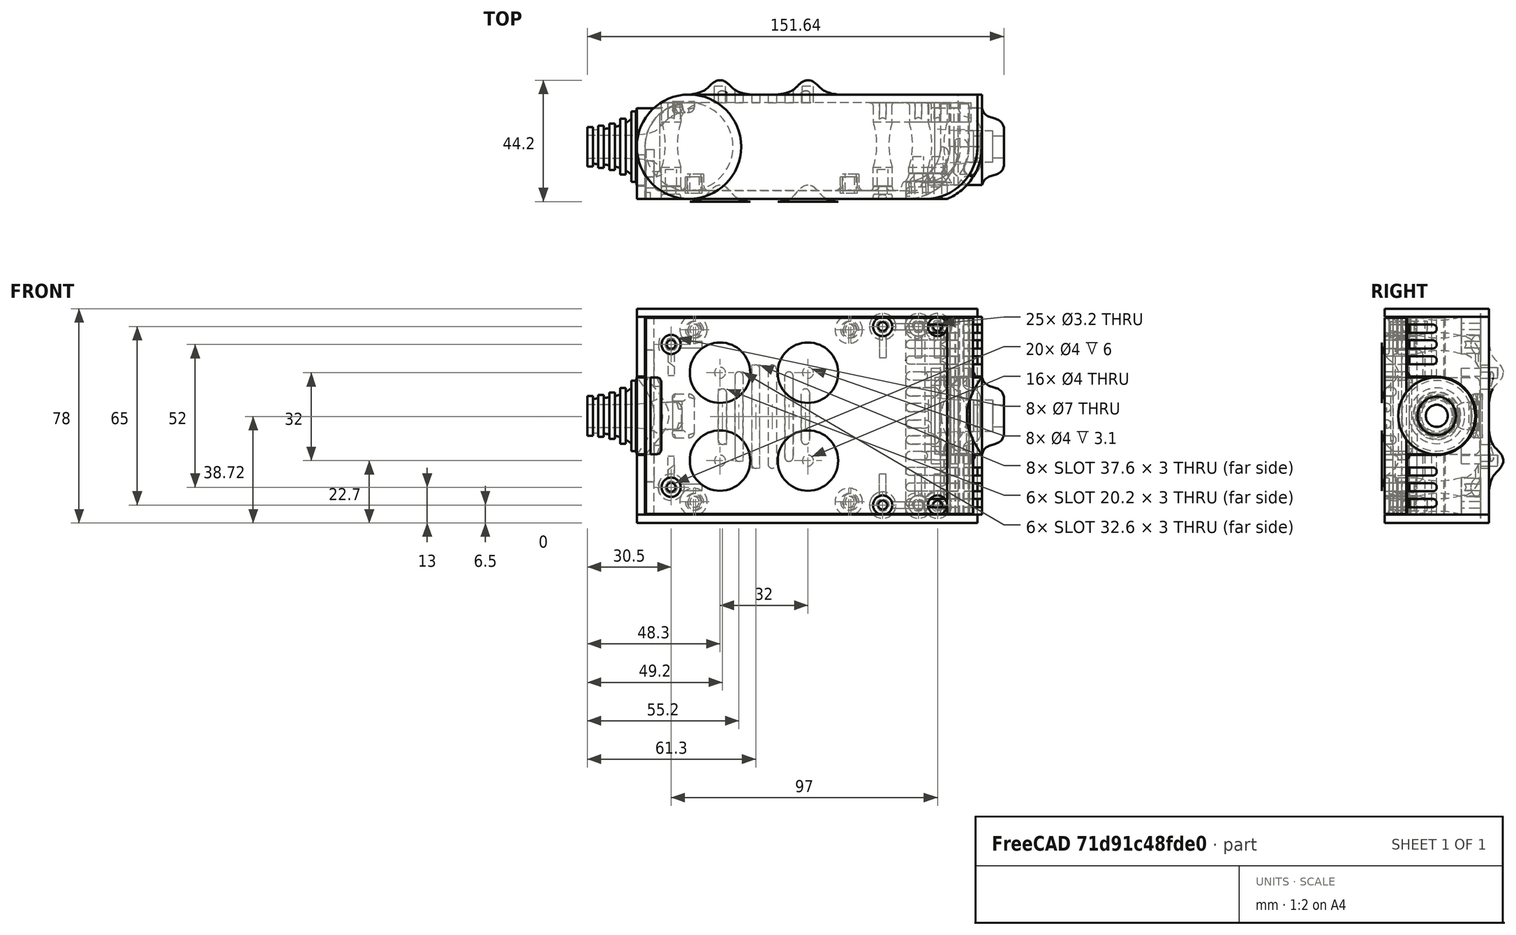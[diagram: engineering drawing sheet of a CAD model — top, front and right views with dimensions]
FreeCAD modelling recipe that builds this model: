
FCSTD DOCUMENT  (FreeCAD 0.19R0.19.2)
Label: enclosure_164
License: All rights reserved
LicenseURL: http://en.wikipedia.org/wiki/All_rights_reserved
objects: Part::Feature×140, Part::Revolution×140, Part::MultiFuse×123, Sketcher::SketchObject×69, Part::Extrusion×54, Part::Cut×53, Part::Cylinder×52, Part::Fillet×50, Part::Box×33, App::MeasureDistance×4
note: 714 computed .brp shape members not serialized (recipe doc carries the construction recipe); baked Part::Feature solids carry a one-line shape summary decoded from their .brp

FEATURE [Sketcher::SketchObject] Sketch  label="topSketch"
  FullyConstrained = true
  sketch-geometry (20):
    g0: LineSegment StartX=5.21097e-06 StartY=3 StartZ=0 EndX=5.21097e-06 EndY=19 EndZ=0
    g1: ArcOfCircle CenterX=19 CenterY=19 CenterZ=0 NormalX=0 NormalY=0 NormalZ=1 AngleXU=0 Radius=19 StartAngle=1.5708 EndAngle=3.14159
    g2: ArcOfCircle CenterX=19 CenterY=19 CenterZ=0 NormalX=0 NormalY=0 NormalZ=1 AngleXU=0 Radius=16 StartAngle=1.5708 EndAngle=3.14159
    g3: LineSegment StartX=114 StartY=35 StartZ=0 EndX=19 EndY=35 EndZ=0
    g4: LineSegment StartX=5.21097e-06 StartY=3 StartZ=0 EndX=5.21097e-06 EndY=0 EndZ=0
    g5: LineSegment StartX=3 StartY=0 StartZ=0 EndX=5.21097e-06 EndY=0 EndZ=0
    g6: LineSegment StartX=3 StartY=19 StartZ=0 EndX=3 EndY=0 EndZ=0
    g7: LineSegment StartX=19 StartY=38 StartZ=0 EndX=124 EndY=38 EndZ=0
    g8: Circle CenterX=119 CenterY=35 CenterZ=0 NormalX=0 NormalY=0 NormalZ=1 AngleXU=0 Radius=1
    g9: Circle CenterX=121 CenterY=35 CenterZ=0 NormalX=0 NormalY=0 NormalZ=1 AngleXU=0 Radius=1
    g10: Circle CenterX=121 CenterY=33 CenterZ=0 NormalX=0 NormalY=0 NormalZ=1 AngleXU=0 Radius=1
    g11: BSplineCurve PolesCount=3 KnotsCount=2 Degree=2 IsPeriodic=0
    g12: GeomPoint X=119 Y=35 Z=0
    g13: GeomPoint X=121 Y=33 Z=0
    g14: LineSegment StartX=119 StartY=35 StartZ=0 EndX=114 EndY=35 EndZ=0
    g15: ArcOfCircle CenterX=105 CenterY=19 CenterZ=0 NormalX=0 NormalY=0 NormalZ=1 AngleXU=0 Radius=19 StartAngle=5.7297 EndAngle=6.28319
    g16: ArcOfCircle CenterX=105 CenterY=19 CenterZ=0 NormalX=0 NormalY=0 NormalZ=1 AngleXU=0 Radius=16 StartAngle=5.60905 EndAngle=6.28319
    g17: LineSegment StartX=121 StartY=33 StartZ=0 EndX=121 EndY=19 EndZ=0
    g18: LineSegment StartX=124 StartY=38 StartZ=0 EndX=124 EndY=19 EndZ=0
    g19: LineSegment StartX=117.5 StartY=9.01251 StartZ=0 EndX=121.163 EndY=9.0125 EndZ=0
  constraints (46):
    c: Vertical(g0)
    c: Block(g0)
    c: Coincident(g1,g0)
    c: Block(g1)
    c: Coincident(g2,g1)
    c: Block(g2)
    c: Coincident(g3,g2)
    c: Horizontal(g3)
    c: Tangent(g3,g2)
    c: Coincident(g4,g0)
    c: Distance(g4) = 3
    c: Vertical(g4)
    c: Coincident(g5,g4)
    c: Horizontal(g5)
    c: Coincident(g6,g2)
    c: Coincident(g6,g5)
    c: Vertical(g6)
    c: Horizontal(g7)
    c: Distance(g7) = 105
    c: Coincident(g7,g1)
    c: Block(g3)
    c: Weight(g8) = 1
    c: Equal(g8,g9)
    c: Equal(g8,g10)
    c: InternalAlignment(g8,g11)
    c: InternalAlignment(g9,g11)
    c: InternalAlignment(g10,g11)
    c: InternalAlignment(g12,g11)
    c: InternalAlignment(g13,g11)
    c: Block(g11)
    c: Coincident(g14,g11)
    c: Coincident(g14,g3)
    c: Horizontal(g14)
    c: Block(g15)
    c: Coincident(g16,g15)
    c: Block(g16)
    c: Coincident(g17,g11)
    c: Coincident(g17,g16)
    c: Vertical(g17)
    c: Distance(g17) = 14
    c: Coincident(g18,g7)
    c: Coincident(g18,g15)
    c: Vertical(g18)
    c: Distance(g18) = 19
    c: Coincident(g19,g16)
    c: Coincident(g19,g15)
FEATURE [Sketcher::SketchObject] Sketch001  label="bottomSketch"
  FullyConstrained = true
  sketch-geometry (32):
    g0: LineSegment StartX=3.3 StartY=-6.03275e-07 StartZ=0 EndX=98 EndY=-6.03275e-07 EndZ=0
    g1: ArcOfCircle CenterX=98 CenterY=19 CenterZ=0 NormalX=0 NormalY=0 NormalZ=1 AngleXU=0 Radius=19 StartAngle=4.71239 EndAngle=5.71103
    g2: LineSegment StartX=6.3 StartY=8 StartZ=0 EndX=3.3 EndY=8 EndZ=0
    g3: LineSegment StartX=3.3 StartY=8 StartZ=0 EndX=3.3 EndY=-6.03275e-07 EndZ=0
    g4: ArcOfCircle CenterX=8.3 CenterY=5 CenterZ=0 NormalX=0 NormalY=0 NormalZ=1 AngleXU=0 Radius=2 StartAngle=3.14159 EndAngle=4.71239
    g5: LineSegment StartX=6.3 StartY=8 StartZ=0 EndX=6.3 EndY=5 EndZ=0
    g6: ArcOfCircle CenterX=98 CenterY=19 CenterZ=0 NormalX=0 NormalY=0 NormalZ=1 AngleXU=0 Radius=12.7 StartAngle=4.71239 EndAngle=6.28319
    g7: LineSegment StartX=94.7 StartY=3 StartZ=0 EndX=8.3 EndY=3 EndZ=0
    g8-g12: Circle x5 (B-spline internal-alignment scaffolding for g13; pole/knot coordinates omitted)
    g13: BSplineCurve PolesCount=5 KnotsCount=3 Degree=3 IsPeriodic=0
    g14: GeomPoint X=98 Y=6.3 Z=0
    g15: GeomPoint X=96.3938 Y=4.71946 Z=0
    g16: GeomPoint X=94.7 Y=3 Z=0
    g17-g23: Circle x7 (B-spline internal-alignment scaffolding for g24; pole/knot coordinates omitted)
    g24: BSplineCurve PolesCount=7 KnotsCount=5 Degree=3 IsPeriodic=0
    g25-g29: GeomPoint x5 (B-spline internal-alignment scaffolding for g24; pole/knot coordinates omitted)
    g30: ArcOfCircle CenterX=98 CenterY=19 CenterZ=0 NormalX=0 NormalY=0 NormalZ=1 AngleXU=0 Radius=15.7 StartAngle=5.81226 EndAngle=6.28319
    g31: LineSegment StartX=110.7 StartY=19 StartZ=0 EndX=113.7 EndY=19 EndZ=0
  constraints (41):
    c: Horizontal(g0)
    c: Coincident(g1,g0)
    c: Block(g1)
    c: Horizontal(g2)
    c: Distance(g2) = 3
    c: Coincident(g3,g2)
    c: Vertical(g3)
    c: Coincident(g3,g0)
    c: Block(g4)
    c: Block(g2)
    c: Coincident(g5,g2)
    c: Coincident(g5,g4)
    c: Vertical(g5)
    c: Coincident(g6,g1)
    c: Block(g6)
    c: Coincident(g7,g4)
    c: Horizontal(g7)
    c: Block(g0)
    c: Block(g7)
    c: Block(g3)
    c: Coincident(g13,g6)
    c: Weight(g8) = 1
    c: Equal(g8, g9-g12) x4
    c: Coincident(g13,g7)
    c: InternalAlignment(g8-g12 -> g13) x5
    c: InternalAlignment(g14,g13)
    c: InternalAlignment(g15,g13)
    c: InternalAlignment(g16,g13)
    c: Block(g13)
    c: Weight(g17) = 1
    c: Equal(g17, g18-g23) x6
    c: Coincident(g24,g1)
    c: InternalAlignment(g17-g23 -> g24) x7
    c: InternalAlignment(g25-g29 -> g24) x5
    c: Block(g24)
    c: Coincident(g30,g24)
    c: Coincident(g31,g6)
    c: Coincident(g31,g30)
    c: Horizontal(g31)
    c: Block(g31)
    c: Block(g30)
FEATURE [Part::Extrusion] Extrude  label="top"
  Base = -> Sketch
  Dir = (0,0,1)
  DirMode = 2
  FaceMakerClass = Part::FaceMakerBullseye
  LengthFwd = 72
  LengthRev = 0
  Solid = true
  Symmetric = false
FEATURE [Part::Extrusion] Extrude001  label="bottom"
  Base = -> Sketch001
  Dir = (0,0,1)
  DirMode = 2
  FaceMakerClass = Part::FaceMakerBullseye
  LengthFwd = 71.4
  LengthRev = 0
  Placement = pos=(0,0,0.3) rot=(0,0,1;0rad)
  Solid = true
  Symmetric = false
FEATURE [Sketcher::SketchObject] Sketch002  label="topSketch001"
  FullyConstrained = true
  sketch-geometry (6):
    g0: ArcOfCircle CenterX=19 CenterY=19 CenterZ=0 NormalX=0 NormalY=0 NormalZ=1 AngleXU=0 Radius=19 StartAngle=1.5708 EndAngle=3.14159
    g1: LineSegment StartX=5.22862e-06 StartY=19 StartZ=0 EndX=5.22862e-06 EndY=1.19904e-11 EndZ=0
    g2: LineSegment StartX=19 StartY=38 StartZ=0 EndX=124 EndY=38 EndZ=0
    g3: LineSegment StartX=5.22862e-06 StartY=1.19904e-11 StartZ=0 EndX=105 EndY=1.19904e-11 EndZ=0
    g4: ArcOfCircle CenterX=105 CenterY=19 CenterZ=0 NormalX=0 NormalY=0 NormalZ=1 AngleXU=0 Radius=19 StartAngle=4.71239 EndAngle=6.28319
    g5: LineSegment StartX=124 StartY=38 StartZ=0 EndX=124 EndY=19 EndZ=0
  constraints (16):
    c: Block(g0)
    c: Coincident(g1,g0)
    c: Vertical(g1)
    c: Horizontal(g2)
    c: Distance(g2) = 105
    c: Coincident(g2,g0)
    c: Distance(g1) = 19
    c: Coincident(g3,g1)
    c: Horizontal(g3)
    c: Distance(g3) = 105
    c: Block(g4)
    c: Coincident(g4,g3)
    c: Coincident(g5,g2)
    c: Coincident(g5,g4)
    c: Vertical(g5)
    c: Distance(g5) = 19
FEATURE [Part::Extrusion] Extrude002  label="sideA"
  Base = -> Sketch002
  Dir = (0,0,1)
  DirMode = 2
  FaceMakerClass = Part::FaceMakerBullseye
  LengthFwd = 3
  LengthRev = 0
  Placement = pos=(0,0,-3) rot=(0,0,1;0rad)
  Solid = true
  Symmetric = false
FEATURE [Sketcher::SketchObject] Sketch003  label="topSketch002"
  FullyConstrained = true
  sketch-geometry (6):
    g0: LineSegment StartX=19 StartY=38 StartZ=0 EndX=117 EndY=38 EndZ=0
    g1: ArcOfCircle CenterX=19 CenterY=19 CenterZ=0 NormalX=0 NormalY=0 NormalZ=1 AngleXU=0 Radius=19 StartAngle=1.5708 EndAngle=3.14159
    g2: LineSegment StartX=117 StartY=38 StartZ=0 EndX=117 EndY=19 EndZ=0
    g3: LineSegment StartX=98 StartY=1.0161e-12 StartZ=0 EndX=5.22862e-06 EndY=1.0161e-12 EndZ=0
    g4: LineSegment StartX=5.22862e-06 StartY=19 StartZ=0 EndX=5.22862e-06 EndY=1.0161e-12 EndZ=0
    g5: ArcOfCircle CenterX=98 CenterY=19 CenterZ=0 NormalX=0 NormalY=0 NormalZ=1 AngleXU=0 Radius=19 StartAngle=4.71239 EndAngle=6.28319
  constraints (16):
    c: Horizontal(g0)
    c: Distance(g0) = 98
    c: Coincident(g1,g0)
    c: Block(g1)
    c: Coincident(g2,g0)
    c: Vertical(g2)
    c: Distance(g2) = 19
    c: Horizontal(g3)
    c: Coincident(g4,g1)
    c: Vertical(g4)
    c: Coincident(g3,g4)
    c: Block(g3)
    c: Coincident(g5,g2)
    c: Coincident(g5,g3)
    c: Block(g0)
    c: Block(g5)
FEATURE [Sketcher::SketchObject] Sketch004
  FullyConstrained = true
  MapMode = 3
  Placement = pos=(0,0,0) rot=(1,0,0;1.5708rad)
  Support = -> [Extrude]
  sketch-geometry (8):
    g0: Circle CenterX=80.351 CenterY=-67.6202 CenterZ=0 NormalX=0 NormalY=0 NormalZ=1 AngleXU=0 Radius=2
    g1: Circle CenterX=80.351 CenterY=-67.6202 CenterZ=0 NormalX=0 NormalY=0 NormalZ=1 AngleXU=0 Radius=3
    g2: Circle CenterX=80.351 CenterY=-4.92017 CenterZ=0 NormalX=0 NormalY=0 NormalZ=1 AngleXU=0 Radius=2
    g3: Circle CenterX=80.351 CenterY=-4.92017 CenterZ=0 NormalX=0 NormalY=0 NormalZ=1 AngleXU=0 Radius=3
    g4: Circle CenterX=23.851 CenterY=-4.92017 CenterZ=0 NormalX=0 NormalY=0 NormalZ=1 AngleXU=0 Radius=2
    g5: Circle CenterX=23.851 CenterY=-4.92017 CenterZ=0 NormalX=0 NormalY=0 NormalZ=1 AngleXU=0 Radius=3
    g6: Circle CenterX=23.851 CenterY=-67.6202 CenterZ=0 NormalX=0 NormalY=0 NormalZ=1 AngleXU=0 Radius=2
    g7: Circle CenterX=23.851 CenterY=-67.6202 CenterZ=0 NormalX=0 NormalY=0 NormalZ=1 AngleXU=0 Radius=3
  constraints (8):
    c: Block(g3)
    c: Block(g2)
    c: Block(g1)
    c: Block(g0)
    c: Block(g6)
    c: Block(g7)
    c: Block(g4)
    c: Block(g5)
FEATURE [Part::Extrusion] Extrude004
  Base = -> Sketch004
  Dir = (0,-1,2e-16)
  DirMode = 2
  FaceMakerClass = Part::FaceMakerBullseye
  LengthFwd = 6
  LengthRev = 0
  Placement = pos=(0,9,0) rot=(0,0,1;0rad)
  Solid = true
  Symmetric = false
FEATURE [Sketcher::SketchObject] Sketch005
  FullyConstrained = true
  MapMode = 3
  Placement = pos=(0,0,0) rot=(1,0,0;1.5708rad)
  Support = -> [Extrude]
  sketch-geometry (8):
    g0: Circle CenterX=80.351 CenterY=-67.6202 CenterZ=0 NormalX=0 NormalY=0 NormalZ=1 AngleXU=0 Radius=3
    g1: Circle CenterX=80.351 CenterY=-4.92017 CenterZ=0 NormalX=0 NormalY=0 NormalZ=1 AngleXU=0 Radius=3
    g2: Circle CenterX=23.851 CenterY=-4.92017 CenterZ=0 NormalX=0 NormalY=0 NormalZ=1 AngleXU=0 Radius=3
    g3: Circle CenterX=23.851 CenterY=-67.6202 CenterZ=0 NormalX=0 NormalY=0 NormalZ=1 AngleXU=0 Radius=3
    g4: Circle CenterX=23.851 CenterY=-67.6202 CenterZ=0 NormalX=0 NormalY=0 NormalZ=1 AngleXU=0 Radius=5
    g5: Circle CenterX=80.351 CenterY=-67.6202 CenterZ=0 NormalX=0 NormalY=0 NormalZ=1 AngleXU=0 Radius=5
    g6: Circle CenterX=23.851 CenterY=-4.92017 CenterZ=0 NormalX=0 NormalY=0 NormalZ=1 AngleXU=0 Radius=5
    g7: Circle CenterX=80.351 CenterY=-4.92017 CenterZ=0 NormalX=0 NormalY=0 NormalZ=1 AngleXU=0 Radius=5
  constraints (8):
    c: Block(g1)
    c: Block(g0)
    c: Block(g3)
    c: Block(g2)
    c: Block(g5)
    c: Block(g4)
    c: Block(g6)
    c: Block(g7)
FEATURE [Part::Extrusion] Extrude005
  Base = -> Sketch005
  Dir = (0,-1,2e-16)
  DirMode = 2
  FaceMakerClass = Part::FaceMakerBullseye
  LengthFwd = 2
  LengthRev = 0
  Solid = true
  Symmetric = false
FEATURE [Sketcher::SketchObject] Sketch006
  FullyConstrained = true
  MapMode = 3
  Placement = pos=(0,0,0) rot=(1,0,0;1.5708rad)
  sketch-geometry (8):
    g0: Circle CenterX=80.351 CenterY=-67.6202 CenterZ=0 NormalX=0 NormalY=0 NormalZ=1 AngleXU=0 Radius=3
    g1: Circle CenterX=80.351 CenterY=-4.92017 CenterZ=0 NormalX=0 NormalY=0 NormalZ=1 AngleXU=0 Radius=3
    g2: Circle CenterX=23.851 CenterY=-4.92017 CenterZ=0 NormalX=0 NormalY=0 NormalZ=1 AngleXU=0 Radius=3
    g3: Circle CenterX=23.851 CenterY=-67.6202 CenterZ=0 NormalX=0 NormalY=0 NormalZ=1 AngleXU=0 Radius=3
    g4: Circle CenterX=23.851 CenterY=-67.6202 CenterZ=0 NormalX=0 NormalY=0 NormalZ=1 AngleXU=0 Radius=5
    g5: Circle CenterX=80.351 CenterY=-67.6202 CenterZ=0 NormalX=0 NormalY=0 NormalZ=1 AngleXU=0 Radius=5
    g6: Circle CenterX=23.851 CenterY=-4.92017 CenterZ=0 NormalX=0 NormalY=0 NormalZ=1 AngleXU=0 Radius=5
    g7: Circle CenterX=80.351 CenterY=-4.92017 CenterZ=0 NormalX=0 NormalY=0 NormalZ=1 AngleXU=0 Radius=5
  constraints (8):
    c: Block(g1)
    c: Block(g0)
    c: Block(g3)
    c: Block(g2)
    c: Block(g5)
    c: Block(g4)
    c: Block(g6)
    c: Block(g7)
FEATURE [Part::Extrusion] Extrude007
  Base = -> Sketch006
  Dir = (0,-1,2e-16)
  DirMode = 2
  FaceMakerClass = Part::FaceMakerBullseye
  LengthFwd = 2
  LengthRev = 0
  Solid = true
  Symmetric = false
FEATURE [Part::Fillet] Fillet
  Base = -> Extrude007
  Edges = 4 edges r=1.99: [Edge6,Edge12,Edge18,Edge24]
FEATURE [Part::Cut] Cut
  Base = -> Extrude005
  Placement = pos=(0,5,0) rot=(0,0,1;0rad)
  Tool = -> Fillet
FEATURE [Part::MultiFuse] Fusion  label="pCBScrews"
  Placement = pos=(-2.5,0,72.3) rot=(0,0,1;0rad)
  Shapes = -> [Extrude004,Cut]
FEATURE [App::MeasureDistance] Distance  label="Distance: 0.69 mm"
  Distance = 0.685967
  P1 = (24.0138,2.9647,0.3)
  P2 = (23.8901,3,-0.373787)
FEATURE [App::MeasureDistance] Distance001  label="Distance: 0.53 mm"
  Distance = 0.533607
  P1 = (80.2939,3,72.2334)
  P2 = (80.281,2.99661,71.7)
FEATURE [Part::Fillet] Fillet001
  Base = -> Extrude001
  Edges = 1 edges r=2.4: [Edge17]
FEATURE [Part::Fillet] Fillet002  label="bottom001"
  Base = -> Fillet001
  Edges = 1 edges r=2.4: [Edge36]
FEATURE [Part::Fillet] Fillet003  label="top001"
  Base = -> Extrude
  Edges = 1 edges r=2: [Edge1]
FEATURE [Sketcher::SketchObject] Sketch007
  FullyConstrained = true
  sketch-geometry (16):
    g0: LineSegment StartX=4 StartY=0 StartZ=0 EndX=4 EndY=2.4 EndZ=0
    g1: LineSegment StartX=4 StartY=2.4 StartZ=0 EndX=7 EndY=2.4 EndZ=0
    g2: LineSegment StartX=4 StartY=0 StartZ=0 EndX=5.7 EndY=0 EndZ=0
    g3: LineSegment StartX=5.7 StartY=0 StartZ=0 EndX=5.7 EndY=-5.6 EndZ=0
    g4-g8: Circle x5 (B-spline internal-alignment scaffolding for g9; pole/knot coordinates omitted)
    g9: BSplineCurve PolesCount=5 KnotsCount=3 Degree=3 IsPeriodic=0
    g10: GeomPoint X=7 Y=2.4 Z=0
    g11: GeomPoint X=10.4582 Y=-1.55472 Z=0
    g12: GeomPoint X=14 Y=-5.6 Z=0
    g13: LineSegment StartX=14 StartY=-5.6 StartZ=0 EndX=14 EndY=-14.1 EndZ=0
    g14: LineSegment StartX=14 StartY=-14.1 StartZ=0 EndX=6.5 EndY=-14.1 EndZ=0
    g15: LineSegment StartX=5.7 StartY=-5.6 StartZ=0 EndX=6.5 EndY=-14.1 EndZ=0
  constraints (28):
    c: Distance(g0) = 2.4
    c: Vertical(g0)
    c: Block(g0)
    c: Coincident(g1,g0)
    c: Horizontal(g1)
    c: Distance(g1) = 3
    c: Coincident(g2,g0)
    c: Horizontal(g2)
    c: Distance(g2) = 1.7
    c: Coincident(g3,g2)
    c: Vertical(g3)
    c: Distance(g3) = 5.6
    c: Coincident(g9,g1)
    c: Weight(g4) = 1
    c: Equal(g4, g5-g8) x4
    c: InternalAlignment(g4-g8 -> g9) x5
    c: InternalAlignment(g10,g9)
    c: InternalAlignment(g11,g9)
    c: InternalAlignment(g12,g9)
    c: Block(g9)
    c: Coincident(g13,g9)
    c: Vertical(g13)
    c: Distance(g13) = 8.5
    c: Coincident(g14,g13)
    c: Horizontal(g14)
    c: Distance(g14) = 7.5
    c: Coincident(g15,g3)
    c: Coincident(g15,g14)
FEATURE [Part::Feature] Face
  shape: bbox 10 x 16.5 x 2e-07 mm, 1 faces, 0 solids (baked)
FEATURE [Part::Revolution] Revolve  label="plugHousing"
  Angle = 360
  Axis = (0,1,0)
  Base = (0,0,0)
  FaceMakerClass = Part::FaceMakerBullseye
  Placement = pos=(0,0,36.15) rot=(0,0,1;0rad)
  Solid = false
  Source = -> Face
  Symmetric = false
FEATURE [Part::Feature] Face001
  shape: bbox 10 x 16.5 x 2e-07 mm, 1 faces, 0 solids (baked)
FEATURE [Part::Revolution] Revolve001  label="plugHousing001"
  Angle = 360
  Axis = (0,1,0)
  Base = (0,0,0)
  FaceMakerClass = Part::FaceMakerBullseye
  Placement = pos=(0,0,36.15) rot=(0,0,1;0rad)
  Solid = false
  Source = -> Face001
  Symmetric = false
FEATURE [Part::MultiFuse] Fusion001  label="plugHousing002"
  Placement = pos=(0,0,0) rot=(0,0,1;1.5708rad)
  Shapes = -> [Revolve001,Revolve]
FEATURE [Part::Feature] Face002
  shape: bbox 10 x 16.5 x 2e-07 mm, 1 faces, 0 solids (baked)
FEATURE [Part::Revolution] Revolve003  label="plugHousing005"
  Angle = 360
  Axis = (0,1,0)
  Base = (0,0,0)
  FaceMakerClass = Part::FaceMakerBullseye
  Placement = pos=(0,0,36.15) rot=(0,0,1;0rad)
  Solid = false
  Source = -> Face002
  Symmetric = false
FEATURE [Part::Feature] Face003
  shape: bbox 10 x 16.5 x 2e-07 mm, 1 faces, 0 solids (baked)
FEATURE [Part::Revolution] Revolve002  label="plugHousing003"
  Angle = 360
  Axis = (0,1,0)
  Base = (0,0,0)
  FaceMakerClass = Part::FaceMakerBullseye
  Placement = pos=(0,0,36.15) rot=(0,0,1;0rad)
  Solid = false
  Source = -> Face003
  Symmetric = false
FEATURE [Part::MultiFuse] Fusion002  label="plugHousing004"
  Placement = pos=(0,0,0) rot=(0,0,1;1.5708rad)
  Shapes = -> [Revolve002,Revolve003]
FEATURE [Part::MultiFuse] Fusion003  label="plugHousing006"
  Placement = pos=(0,19,0) rot=(0,0,1;3.14159rad)
  Shapes = -> [Fusion002,Fusion001]
FEATURE [Part::Feature] Face004
  shape: bbox 10 x 16.5 x 2e-07 mm, 1 faces, 0 solids (baked)
FEATURE [Part::Revolution] Revolve006  label="plugHousing010"
  Angle = 360
  Axis = (0,1,0)
  Base = (0,0,0)
  FaceMakerClass = Part::FaceMakerBullseye
  Placement = pos=(0,0,36.15) rot=(0,0,1;0rad)
  Solid = false
  Source = -> Face004
  Symmetric = false
FEATURE [Part::Feature] Face005
  shape: bbox 10 x 16.5 x 2e-07 mm, 1 faces, 0 solids (baked)
FEATURE [Part::Revolution] Revolve007  label="plugHousing011"
  Angle = 360
  Axis = (0,1,0)
  Base = (0,0,0)
  FaceMakerClass = Part::FaceMakerBullseye
  Placement = pos=(0,0,36.15) rot=(0,0,1;0rad)
  Solid = false
  Source = -> Face005
  Symmetric = false
FEATURE [Part::Feature] Face006
  shape: bbox 10 x 16.5 x 2e-07 mm, 1 faces, 0 solids (baked)
FEATURE [Part::Revolution] Revolve004  label="plugHousing007"
  Angle = 360
  Axis = (0,1,0)
  Base = (0,0,0)
  FaceMakerClass = Part::FaceMakerBullseye
  Placement = pos=(0,0,36.15) rot=(0,0,1;0rad)
  Solid = false
  Source = -> Face006
  Symmetric = false
FEATURE [Part::MultiFuse] Fusion004  label="plugHousing009"
  Placement = pos=(0,0,0) rot=(0,0,1;1.5708rad)
  Shapes = -> [Revolve004,Revolve007]
FEATURE [Part::Feature] Face007
  shape: bbox 10 x 16.5 x 2e-07 mm, 1 faces, 0 solids (baked)
FEATURE [Part::Revolution] Revolve005  label="plugHousing008"
  Angle = 360
  Axis = (0,1,0)
  Base = (0,0,0)
  FaceMakerClass = Part::FaceMakerBullseye
  Placement = pos=(0,0,36.15) rot=(0,0,1;0rad)
  Solid = false
  Source = -> Face007
  Symmetric = false
FEATURE [Part::MultiFuse] Fusion005  label="plugHousing012"
  Placement = pos=(0,0,0) rot=(0,0,1;1.5708rad)
  Shapes = -> [Revolve006,Revolve005]
FEATURE [Part::MultiFuse] Fusion006  label="plugHousing013"
  Placement = pos=(0,19,0) rot=(0,0,1;3.14159rad)
  Shapes = -> [Fusion005,Fusion004]
FEATURE [Part::MultiFuse] Fusion007  label="plugHousing014"
  Placement = pos=(122.621,0,-0.15) rot=(0,0,1;0rad)
  Shapes = -> [Fusion003,Fusion006]
FEATURE [Part::Cylinder] Cylinder002
  Angle = 360
  AttacherType = Attacher::AttachEngine3D
  Height = 20
  Placement = pos=(0,0,36.15) rot=(0,0,1;0rad)
  Radius = 4
FEATURE [Part::Cylinder] Cylinder003
  Angle = 360
  AttacherType = Attacher::AttachEngine3D
  Height = 10
  Placement = pos=(0,0,36.15) rot=(0,0,1;0rad)
  Radius = 4
FEATURE [Part::MultiFuse] Fusion009  label="removeToCreateHoleForPlugHousing"
  Placement = pos=(70,19,36.15) rot=(0,1,0;1.5708rad)
  Shapes = -> [Cylinder002,Cylinder003]
FEATURE [Part::Cylinder] Cylinder004
  Angle = 360
  AttacherType = Attacher::AttachEngine3D
  Height = 20
  Placement = pos=(0,0,36.15) rot=(0,0,1;0rad)
  Radius = 4
FEATURE [Part::Cylinder] Cylinder005
  Angle = 360
  AttacherType = Attacher::AttachEngine3D
  Height = 10
  Placement = pos=(0,0,36.15) rot=(0,0,1;0rad)
  Radius = 4
FEATURE [Part::MultiFuse] Fusion010  label="removeToCreateHoleForPlugHousing001"
  Placement = pos=(70,19,36.15) rot=(0,1,0;1.5708rad)
  Shapes = -> [Cylinder004,Cylinder005]
FEATURE [Part::Cut] Cut001
  Base = -> Fillet003
  Tool = -> Fusion010
FEATURE [Part::Cut] Cut002  label="Bottom"
  Base = -> Fillet002
  Tool = -> Fusion009
FEATURE [Part::Feature] Face008
  shape: bbox 10 x 16.5 x 2e-07 mm, 1 faces, 0 solids (baked)
FEATURE [Part::Revolution] Revolve011  label="plugHousing021"
  Angle = 360
  Axis = (0,1,0)
  Base = (0,0,0)
  FaceMakerClass = Part::FaceMakerBullseye
  Placement = pos=(0,0,36.15) rot=(0,0,1;0rad)
  Solid = false
  Source = -> Face008
  Symmetric = false
FEATURE [Part::Feature] Face009
  shape: bbox 10 x 16.5 x 2e-07 mm, 1 faces, 0 solids (baked)
FEATURE [Part::Revolution] Revolve012  label="plugHousing022"
  Angle = 360
  Axis = (0,1,0)
  Base = (0,0,0)
  FaceMakerClass = Part::FaceMakerBullseye
  Placement = pos=(0,0,36.15) rot=(0,0,1;0rad)
  Solid = false
  Source = -> Face009
  Symmetric = false
FEATURE [Part::Feature] Face010 .. Face013  x4 (patterned run collapsed; names and placements below)
  shape: bbox 10 x 16.5 x 2e-07 mm, 1 faces, 0 solids (baked)
FEATURE [Part::Revolution] Revolve015  label="plugHousing027"
  Angle = 360
  Axis = (0,1,0)
  Base = (0,0,0)
  FaceMakerClass = Part::FaceMakerBullseye
  Placement = pos=(0,0,36.15) rot=(0,0,1;0rad)
  Solid = false
  Source = -> Face013
  Symmetric = false
FEATURE [Part::Feature] Face014
  shape: bbox 10 x 16.5 x 2e-07 mm, 1 faces, 0 solids (baked)
FEATURE [Part::Feature] Face015
  shape: bbox 10 x 16.5 x 2e-07 mm, 1 faces, 0 solids (baked)
FEATURE [Part::Feature] Face016
  shape: bbox 10 x 16.5 x 2e-07 mm, 1 faces, 0 solids (baked)
FEATURE [Part::Revolution] Revolve019  label="plugHousing033"
  Angle = 360
  Axis = (0,1,0)
  Base = (0,0,0)
  FaceMakerClass = Part::FaceMakerBullseye
  Placement = pos=(0,0,36.15) rot=(0,0,1;0rad)
  Solid = false
  Source = -> Face016
  Symmetric = false
FEATURE [Part::Feature] Face017
  shape: bbox 10 x 16.5 x 2e-07 mm, 1 faces, 0 solids (baked)
FEATURE [Part::Revolution] Revolve020  label="plugHousing034"
  Angle = 360
  Axis = (0,1,0)
  Base = (0,0,0)
  FaceMakerClass = Part::FaceMakerBullseye
  Placement = pos=(0,0,36.15) rot=(0,0,1;0rad)
  Solid = false
  Source = -> Face017
  Symmetric = false
FEATURE [Part::Feature] Face018
  shape: bbox 10 x 16.5 x 2e-07 mm, 1 faces, 0 solids (baked)
FEATURE [Part::Revolution] Revolve016  label="plugHousing030"
  Angle = 360
  Axis = (0,1,0)
  Base = (0,0,0)
  FaceMakerClass = Part::FaceMakerBullseye
  Placement = pos=(0,0,36.15) rot=(0,0,1;0rad)
  Solid = false
  Source = -> Face018
  Symmetric = false
FEATURE [Part::MultiFuse] Fusion020  label="plugHousing038"
  Placement = pos=(0,0,0) rot=(0,0,1;1.5708rad)
  Shapes = -> [Revolve016,Revolve020]
FEATURE [Part::Feature] Face019
  shape: bbox 10 x 16.5 x 2e-07 mm, 1 faces, 0 solids (baked)
FEATURE [Part::Feature] Face020
  shape: bbox 10 x 16.5 x 2e-07 mm, 1 faces, 0 solids (baked)
FEATURE [Part::Revolution] Revolve017  label="plugHousing031"
  Angle = 360
  Axis = (0,1,0)
  Base = (0,0,0)
  FaceMakerClass = Part::FaceMakerBullseye
  Placement = pos=(0,0,36.15) rot=(0,0,1;0rad)
  Solid = false
  Source = -> Face020
  Symmetric = false
FEATURE [Part::MultiFuse] Fusion021  label="plugHousing039"
  Placement = pos=(0,0,0) rot=(0,0,1;1.5708rad)
  Shapes = -> [Revolve019,Revolve017]
FEATURE [Part::MultiFuse] Fusion023  label="plugHousing041"
  Placement = pos=(0,19,0) rot=(0,0,1;3.14159rad)
  Shapes = -> [Fusion021,Fusion020]
FEATURE [Part::Revolution] Revolve022  label="plugHousing043"
  Angle = 360
  Axis = (0,1,0)
  Base = (0,0,0)
  FaceMakerClass = Part::FaceMakerBullseye
  Placement = pos=(0,0,36.15) rot=(0,0,1;0rad)
  Solid = false
  Source = -> Face019
  Symmetric = false
FEATURE [Part::Feature] Face021
  shape: bbox 10 x 16.5 x 2e-07 mm, 1 faces, 0 solids (baked)
FEATURE [Part::Revolution] Revolve023  label="plugHousing044"
  Angle = 360
  Axis = (0,1,0)
  Base = (0,0,0)
  FaceMakerClass = Part::FaceMakerBullseye
  Placement = pos=(0,0,36.15) rot=(0,0,1;0rad)
  Solid = false
  Source = -> Face021
  Symmetric = false
FEATURE [Part::Feature] Face022
  shape: bbox 10 x 16.5 x 2e-07 mm, 1 faces, 0 solids (baked)
FEATURE [Part::Revolution] Revolve018  label="plugHousing032"
  Angle = 360
  Axis = (0,1,0)
  Base = (0,0,0)
  FaceMakerClass = Part::FaceMakerBullseye
  Placement = pos=(0,0,36.15) rot=(0,0,1;0rad)
  Solid = false
  Source = -> Face022
  Symmetric = false
FEATURE [Part::MultiFuse] Fusion022  label="plugHousing040"
  Placement = pos=(0,0,0) rot=(0,0,1;1.5708rad)
  Shapes = -> [Revolve018,Revolve023]
FEATURE [Part::Feature] Face023
  shape: bbox 10 x 16.5 x 2e-07 mm, 1 faces, 0 solids (baked)
FEATURE [Part::Revolution] Revolve021  label="plugHousing035"
  Angle = 360
  Axis = (0,1,0)
  Base = (0,0,0)
  FaceMakerClass = Part::FaceMakerBullseye
  Placement = pos=(0,0,36.15) rot=(0,0,1;0rad)
  Solid = false
  Source = -> Face023
  Symmetric = false
FEATURE [Part::MultiFuse] Fusion018  label="plugHousing036"
  Placement = pos=(0,0,0) rot=(0,0,1;1.5708rad)
  Shapes = -> [Revolve022,Revolve021]
FEATURE [Part::MultiFuse] Fusion019  label="plugHousing037"
  Placement = pos=(0,19,0) rot=(0,0,1;3.14159rad)
  Shapes = -> [Fusion018,Fusion022]
FEATURE [Part::MultiFuse] Fusion024  label="plugHousing042"
  Placement = pos=(122.621,0,-0.15) rot=(0,0,1;0rad)
  Shapes = -> [Fusion023,Fusion019]
FEATURE [Part::Cylinder] Cylinder006
  Angle = 360
  AttacherType = Attacher::AttachEngine3D
  Height = 20
  Placement = pos=(0,0,36.15) rot=(0,0,1;0rad)
  Radius = 14.3
FEATURE [Part::Cylinder] Cylinder007
  Angle = 360
  AttacherType = Attacher::AttachEngine3D
  Height = 10
  Placement = pos=(0,0,36.15) rot=(0,0,1;0rad)
  Radius = 4
FEATURE [Part::MultiFuse] Fusion026  label="removeToCreteHoleForPlugHousing"
  Placement = pos=(70,19,36) rot=(0,1,0;1.5708rad)
  Shapes = -> [Cylinder006,Cylinder007]
FEATURE [Part::Box] Box001  label="Cube001"
  AttacherType = Attacher::AttachEngine3D
  Height = 28
  Length = 3
  Placement = pos=(110.7,19,22) rot=(0,0,1;0rad)
  Width = 15.7
FEATURE [Part::Cut] Cut003  label="top002"
  Base = -> Cut001
  Tool = -> Fusion007
FEATURE [Part::Revolution] Revolve008  label="plugHousing015"
  Angle = 360
  Axis = (0,1,0)
  Base = (0,0,0)
  FaceMakerClass = Part::FaceMakerBullseye
  Placement = pos=(0,0,36.15) rot=(0,0,1;0rad)
  Solid = false
  Source = -> Face010
  Symmetric = false
FEATURE [Part::MultiFuse] Fusion013  label="plugHousing020"
  Placement = pos=(0,0,0) rot=(0,0,1;1.5708rad)
  Shapes = -> [Revolve008,Revolve012]
FEATURE [Part::Cut] Cut004  label="top003"
  Base = -> Cut003
  Placement = pos=(1,0,0) rot=(0,0,1;0rad)
  Tool = -> Fusion026
FEATURE [Part::Cylinder] Cylinder008
  Angle = 360
  AttacherType = Attacher::AttachEngine3D
  Height = 20
  Placement = pos=(0,0,36.15) rot=(0,0,1;0rad)
  Radius = 10.3
FEATURE [Part::Cylinder] Cylinder009
  Angle = 360
  AttacherType = Attacher::AttachEngine3D
  Height = 10
  Placement = pos=(0,0,36.15) rot=(0,0,1;0rad)
  Radius = 4
FEATURE [Part::MultiFuse] Fusion027  label="removeToCreteHoleForPlugHousing001"
  Placement = pos=(70,19,36) rot=(0,1,0;1.5708rad)
  Shapes = -> [Cylinder008,Cylinder009]
FEATURE [Part::Cut] Cut005  label="plugHousingTab"
  Base = -> Box001
  Tool = -> Fusion027
FEATURE [Part::MultiFuse] Fusion028  label="plugHousing045"
  Shapes = -> [Fusion024,Cut005]
FEATURE [Part::Box] Box002  label="Cube002"
  AttacherType = Attacher::AttachEngine3D
  Height = 28.8
  Length = 3
  Placement = pos=(107.3,28,21.6) rot=(0,0,1;0rad)
  Width = 7
FEATURE [Part::Box] Box003  label="Cube003"
  AttacherType = Attacher::AttachEngine3D
  Height = 3
  Length = 6.4
  Placement = pos=(107.3,28,18.6) rot=(0,0,1;0rad)
  Width = 7
FEATURE [Part::Box] Box004  label="Cube004"
  AttacherType = Attacher::AttachEngine3D
  Height = 3
  Length = 6.4
  Placement = pos=(107.3,28,50.4) rot=(0,0,1;0rad)
  Width = 7
FEATURE [Part::MultiFuse] Fusion029  label="plugHousingBracketHolder"
  Shapes = -> [Box004,Box002,Box003]
FEATURE [Part::Cylinder] Cylinder010
  Angle = 360
  AttacherType = Attacher::AttachEngine3D
  Height = 20
  Placement = pos=(0,0,36.15) rot=(0,0,1;0rad)
  Radius = 14.3
FEATURE [Part::Cylinder] Cylinder011
  Angle = 360
  AttacherType = Attacher::AttachEngine3D
  Height = 10
  Placement = pos=(0,0,36.15) rot=(0,0,1;0rad)
  Radius = 4
FEATURE [Part::MultiFuse] Fusion030  label="removeToCreteHoleForPlugHousing002"
  Placement = pos=(70,19,36) rot=(0,1,0;1.5708rad)
  Shapes = -> [Cylinder010,Cylinder011]
FEATURE [Part::Cut] Cut006  label="plugHousingBracketHolder001"
  Base = -> Fusion029
  Tool = -> Fusion030
FEATURE [Part::Cylinder] Cylinder012
  Angle = 360
  AttacherType = Attacher::AttachEngine3D
  Height = 20
  Placement = pos=(0,0,36.15) rot=(0,0,1;0rad)
  Radius = 7
FEATURE [Part::Cylinder] Cylinder013
  Angle = 360
  AttacherType = Attacher::AttachEngine3D
  Height = 10
  Placement = pos=(0,0,36.15) rot=(0,0,1;0rad)
  Radius = 4
FEATURE [Part::MultiFuse] Fusion032  label="removeToCreteHoleForPlugHousing003"
  Placement = pos=(70,19,36) rot=(0,1,0;1.5708rad)
  Shapes = -> [Cylinder012,Cylinder013]
FEATURE [Part::Cut] Cut007  label="bottom002"
  Base = -> Cut002
  Tool = -> Fusion032
FEATURE [Sketcher::SketchObject] Sketch008
  FullyConstrained = true
  sketch-geometry (54):
    g0: LineSegment StartX=-4.2 StartY=0 StartZ=0 EndX=-6.2 EndY=0 EndZ=0
    g1: LineSegment StartX=-14 StartY=-18 StartZ=0 EndX=-14 EndY=-26.5 EndZ=0
    g2: LineSegment StartX=-4.2 StartY=0 StartZ=0 EndX=-4.2 EndY=-13.4877 EndZ=0
    g3: Circle CenterX=-4.2 CenterY=-13.4877 CenterZ=0 NormalX=0 NormalY=0 NormalZ=1 AngleXU=0 Radius=1
    g4: Circle CenterX=-4.2 CenterY=-26.5 CenterZ=0 NormalX=0 NormalY=0 NormalZ=1 AngleXU=0 Radius=1
    g5: Circle CenterX=-8.2 CenterY=-26.5 CenterZ=0 NormalX=0 NormalY=0 NormalZ=1 AngleXU=0 Radius=1
    g6: BSplineCurve PolesCount=3 KnotsCount=2 Degree=2 IsPeriodic=0
    g7: GeomPoint X=-4.2 Y=-13.4877 Z=0
    g8: GeomPoint X=-8.2 Y=-26.5 Z=0
    g9: LineSegment StartX=-14 StartY=-26.5 StartZ=0 EndX=-8.2 EndY=-26.5 EndZ=0
    g10: LineSegment StartX=-10.15 StartY=-12 StartZ=0 EndX=-10.15 EndY=-14 EndZ=0
    g11: LineSegment StartX=-12.8401 StartY=-16 StartZ=0 EndX=-10.1571 EndY=-16 EndZ=0
    g12: LineSegment StartX=-10.15 StartY=-14 StartZ=0 EndX=-8.70761 EndY=-14 EndZ=0
    g13: LineSegment StartX=-12.8401 StartY=-16 StartZ=0 EndX=-12.8401 EndY=-17.6958 EndZ=0
    g14: LineSegment StartX=-10.15 StartY=-12 StartZ=0 EndX=-7.79258 EndY=-12 EndZ=0
    g15: Circle CenterX=-6.2215 CenterY=-2 CenterZ=0 NormalX=0 NormalY=0 NormalZ=1 AngleXU=0 Radius=1
    g16: Circle CenterX=-6.22762 CenterY=-2.58724 CenterZ=0 NormalX=0 NormalY=0 NormalZ=1 AngleXU=0 Radius=1
    g17: Circle CenterX=-6.32538 CenterY=-4 CenterZ=0 NormalX=0 NormalY=0 NormalZ=1 AngleXU=0 Radius=1
    g18: BSplineCurve PolesCount=3 KnotsCount=2 Degree=2 IsPeriodic=0
    g19: GeomPoint X=-6.2215 Y=-2 Z=0
    g20: GeomPoint X=-6.32538 Y=-4 Z=0
    g21: Circle CenterX=-6.48644 CenterY=-5.99526 CenterZ=0 NormalX=0 NormalY=0 NormalZ=1 AngleXU=0 Radius=1
    g22: Circle CenterX=-6.58486 CenterY=-6.99526 CenterZ=0 NormalX=0 NormalY=0 NormalZ=1 AngleXU=0 Radius=1
    g23: Circle CenterX=-6.77343 CenterY=-8 CenterZ=0 NormalX=0 NormalY=0 NormalZ=1 AngleXU=0 Radius=1
    g24: BSplineCurve PolesCount=3 KnotsCount=2 Degree=2 IsPeriodic=0
    g25: GeomPoint X=-6.48644 Y=-5.99526 Z=0
    g26: GeomPoint X=-6.77343 Y=-8 Z=0
    g27: Circle CenterX=-7.19003 CenterY=-10 CenterZ=0 NormalX=0 NormalY=0 NormalZ=1 AngleXU=0 Radius=1
    g28: Circle CenterX=-7.44407 CenterY=-11.0915 CenterZ=0 NormalX=0 NormalY=0 NormalZ=1 AngleXU=0 Radius=1
    g29: Circle CenterX=-7.79258 CenterY=-12 CenterZ=0 NormalX=0 NormalY=0 NormalZ=1 AngleXU=0 Radius=1
    g30: BSplineCurve PolesCount=3 KnotsCount=2 Degree=2 IsPeriodic=0
    g31: GeomPoint X=-7.19003 Y=-10 Z=0
    g32: GeomPoint X=-7.79258 Y=-12 Z=0
    g33: Circle CenterX=-8.70761 CenterY=-14 CenterZ=0 NormalX=0 NormalY=0 NormalZ=1 AngleXU=0 Radius=1
    g34: Circle CenterX=-9.33087 CenterY=-15.1837 CenterZ=0 NormalX=0 NormalY=0 NormalZ=1 AngleXU=0 Radius=1
    g35: Circle CenterX=-10.1571 CenterY=-16 CenterZ=0 NormalX=0 NormalY=0 NormalZ=1 AngleXU=0 Radius=1
    g36: BSplineCurve PolesCount=3 KnotsCount=2 Degree=2 IsPeriodic=0
    g37: GeomPoint X=-8.70761 Y=-14 Z=0
    g38: GeomPoint X=-10.1571 Y=-16 Z=0
    g39: Circle CenterX=-12.8401 CenterY=-17.6958 CenterZ=0 NormalX=0 NormalY=0 NormalZ=1 AngleXU=0 Radius=1
    g40: Circle CenterX=-13.3521 CenterY=-17.9027 CenterZ=0 NormalX=0 NormalY=0 NormalZ=1 AngleXU=0 Radius=1
    g41: Circle CenterX=-14 CenterY=-18 CenterZ=0 NormalX=0 NormalY=0 NormalZ=1 AngleXU=0 Radius=1
    g42: BSplineCurve PolesCount=3 KnotsCount=2 Degree=2 IsPeriodic=0
    g43: GeomPoint X=-12.8401 Y=-17.6958 Z=0
    g44: GeomPoint X=-14 Y=-18 Z=0
    g45: LineSegment StartX=-6.2 StartY=0 StartZ=0 EndX=-7.2 EndY=0 EndZ=0
    g46: LineSegment StartX=-7.2 StartY=0 StartZ=0 EndX=-7.2 EndY=-2 EndZ=0
    g47: LineSegment StartX=-7.2 StartY=-2 StartZ=0 EndX=-6.2215 EndY=-2 EndZ=0
    g48: LineSegment StartX=-6.32538 StartY=-4 StartZ=0 EndX=-7.65538 EndY=-4 EndZ=0
    g49: LineSegment StartX=-7.65538 StartY=-4 StartZ=0 EndX=-7.65538 EndY=-5.99526 EndZ=0
    g50: LineSegment StartX=-7.65538 StartY=-5.99526 StartZ=0 EndX=-6.48644 EndY=-5.99526 EndZ=0
    g51: LineSegment StartX=-6.77343 StartY=-8 StartZ=0 EndX=-8.43343 EndY=-8 EndZ=0
    g52: LineSegment StartX=-8.43343 StartY=-8 StartZ=0 EndX=-8.43343 EndY=-10 EndZ=0
    g53: LineSegment StartX=-8.43343 StartY=-10 StartZ=0 EndX=-7.19003 EndY=-10 EndZ=0
  constraints (112):
    c: Horizontal(g0)
    c: Distance(g0) = 2
    c: Block(g0)
    c: Vertical(g1)
    c: Coincident(g2,g0)
    c: Vertical(g2)
    c: Block(g2)
    c: Coincident(g6,g2)
    c: Weight(g3) = 1
    c: Equal(g3,g4)
    c: Equal(g3,g5)
    c: InternalAlignment(g3,g6)
    c: InternalAlignment(g4,g6)
    c: InternalAlignment(g5,g6)
    c: InternalAlignment(g7,g6)
    c: InternalAlignment(g8,g6)
    c: Block(g6)
    c: Coincident(g9,g1)
    c: Coincident(g9,g6)
    c: Horizontal(g9)
    c: Vertical(g10)
    c: Block(g10)
    c: Horizontal(g11)
    c: Block(g11)
    c: Coincident(g12,g10)
    c: Horizontal(g12)
    c: Block(g12)
    c: Coincident(g13,g11)
    c: Vertical(g13)
    c: Block(g13)
    c: Coincident(g14,g10)
    c: Horizontal(g14)
    c: Block(g14)
    c: Block(g9)
    c: Block(g1)
    c: Weight(g15) = 1
    c: Equal(g15,g16)
    c: Equal(g15,g17)
    c: InternalAlignment(g15,g18)
    c: InternalAlignment(g16,g18)
    c: InternalAlignment(g17,g18)
    c: InternalAlignment(g19,g18)
    c: InternalAlignment(g20,g18)
    c: Weight(g21) = 1
    c: Equal(g21,g22)
    c: Equal(g21,g23)
    c: InternalAlignment(g21,g24)
    c: InternalAlignment(g22,g24)
    c: InternalAlignment(g23,g24)
    c: InternalAlignment(g25,g24)
    c: InternalAlignment(g26,g24)
    c: Weight(g27) = 1
    c: Equal(g27,g28)
    c: Equal(g27,g29)
    c: Coincident(g30,g14)
    c: InternalAlignment(g27,g30)
    c: InternalAlignment(g28,g30)
    c: InternalAlignment(g29,g30)
    c: InternalAlignment(g31,g30)
    c: InternalAlignment(g32,g30)
    c: Coincident(g36,g12)
    c: Weight(g33) = 1
    c: Equal(g33,g34)
    c: Equal(g33,g35)
    c: Coincident(g36,g11)
    c: InternalAlignment(g33,g36)
    c: InternalAlignment(g34,g36)
    c: InternalAlignment(g35,g36)
    c: InternalAlignment(g37,g36)
    c: InternalAlignment(g38,g36)
    c: Coincident(g42,g13)
    c: Weight(g39) = 1
    c: Equal(g39,g40)
    c: Equal(g39,g41)
    c: Coincident(g42,g1)
    c: InternalAlignment(g39,g42)
    c: InternalAlignment(g40,g42)
    c: InternalAlignment(g41,g42)
    c: InternalAlignment(g43,g42)
    c: InternalAlignment(g44,g42)
    c: Block(g18)
    c: Block(g24)
    c: Block(g30)
    c: Block(g36)
    c: Block(g42)
    c: Horizontal(g45)
    c: Coincident(g45,g0)
    c: Vertical(g46)
    c: Coincident(g46,g45)
    c: Coincident(g47,g46)
    c: Coincident(g47,g18)
    c: Horizontal(g47)
    c: Block(g46)
    c: Coincident(g48,g18)
    c: Horizontal(g48)
    c: Distance(g48) = 1.33
    c: Vertical(g49)
    c: Coincident(g49,g48)
    c: Coincident(g50,g49)
    c: Coincident(g50,g24)
    c: Horizontal(g50)
    c: Tangent(g50,g22)
    c: Horizontal(g51)
    c: Coincident(g51,g24)
    c: Block(g51)
    c: Vertical(g52)
    c: Block(g52)
    c: Coincident(g52,g51)
    c: Coincident(g53,g52)
    c: Coincident(g53,g30)
    c: Horizontal(g53)
    c: Distance(g1) = 8.5
FEATURE [Part::Feature] Face024
  shape: bbox 9.8 x 26.5 x 2e-07 mm, 1 faces, 0 solids (baked)
FEATURE [Part::Revolution] Revolve024
  Angle = 360
  Axis = (0,1,0)
  Base = (0,0,0)
  FaceMakerClass = Part::FaceMakerBullseye
  Placement = pos=(0,0,0) rot=(0,0,1;1.5708rad)
  Solid = false
  Source = -> Face024
  Symmetric = false
FEATURE [Part::Feature] Face025
  shape: bbox 9.8 x 26.5 x 2e-07 mm, 1 faces, 0 solids (baked)
FEATURE [Part::Revolution] Revolve025
  Angle = 360
  Axis = (0,1,0)
  Base = (0,0,0)
  FaceMakerClass = Part::FaceMakerBullseye
  Placement = pos=(0,0,0) rot=(0,0,1;1.5708rad)
  Solid = false
  Source = -> Face025
  Symmetric = false
FEATURE [Part::MultiFuse] Fusion033
  Placement = pos=(-18,19,36) rot=(0,0,1;0rad)
  Shapes = -> [Revolve025,Revolve024]
FEATURE [Part::Cylinder] Cylinder014
  Angle = 360
  AttacherType = Attacher::AttachEngine3D
  Height = 20
  Placement = pos=(0,0,36.15) rot=(0,0,1;0rad)
  Radius = 14.3
FEATURE [Part::Cylinder] Cylinder015
  Angle = 360
  AttacherType = Attacher::AttachEngine3D
  Height = 10
  Placement = pos=(0,0,36.15) rot=(0,0,1;0rad)
  Radius = 4
FEATURE [Part::MultiFuse] Fusion034  label="removeToCreteHoleForPlugHousing004"
  Placement = pos=(-42,19,36) rot=(0,1,0;1.5708rad)
  Shapes = -> [Cylinder014,Cylinder015]
FEATURE [Part::Cut] Cut008  label="top004"
  Base = -> Cut004
  Placement = pos=(-1,0,0) rot=(0,0,1;0rad)
  Tool = -> Fusion034
FEATURE [Part::Box] Box005  label="Cube005"
  AttacherType = Attacher::AttachEngine3D
  Height = 28
  Length = 3
  Placement = pos=(110.7,19,22) rot=(0,0,1;0rad)
  Width = 15.7
FEATURE [Part::Cylinder] Cylinder016
  Angle = 360
  AttacherType = Attacher::AttachEngine3D
  Height = 10
  Placement = pos=(0,0,36.15) rot=(0,0,1;0rad)
  Radius = 4
FEATURE [Part::Cylinder] Cylinder017
  Angle = 360
  AttacherType = Attacher::AttachEngine3D
  Height = 20
  Placement = pos=(0,0,36.15) rot=(0,0,1;0rad)
  Radius = 10.3
FEATURE [Part::MultiFuse] Fusion035  label="removeToCreteHoleForPlugHousing005"
  Placement = pos=(70,19,36) rot=(0,1,0;1.5708rad)
  Shapes = -> [Cylinder017,Cylinder016]
FEATURE [Part::Cut] Cut009  label="plugHousingTab001"
  Base = -> Box005
  Placement = pos=(-107.4,-14,0) rot=(0,0,1;0rad)
  Tool = -> Fusion035
FEATURE [Part::Box] Box006  label="Cube006"
  AttacherType = Attacher::AttachEngine3D
  Height = 28
  Length = 3
  Placement = pos=(110.7,19,22) rot=(0,0,1;0rad)
  Width = 15.7
FEATURE [Part::Cylinder] Cylinder018
  Angle = 360
  AttacherType = Attacher::AttachEngine3D
  Height = 10
  Placement = pos=(0,0,36.15) rot=(0,0,1;0rad)
  Radius = 4
FEATURE [Part::Cylinder] Cylinder019
  Angle = 360
  AttacherType = Attacher::AttachEngine3D
  Height = 20
  Placement = pos=(0,0,36.15) rot=(0,0,1;0rad)
  Radius = 10.3
FEATURE [Part::MultiFuse] Fusion036  label="removeToCreteHoleForPlugHousing006"
  Placement = pos=(70,19,36) rot=(0,1,0;1.5708rad)
  Shapes = -> [Cylinder019,Cylinder018]
FEATURE [Part::Cut] Cut010  label="plugHousingTab002"
  Base = -> Box006
  Placement = pos=(-107.4,-14,0) rot=(0,0,1;0rad)
  Tool = -> Fusion036
FEATURE [Part::MultiFuse] Fusion037
  Placement = pos=(9.6,23,0) rot=(0,0,1;3.14159rad)
  Shapes = -> [Cut009,Cut010]
FEATURE [Part::Box] Box  label="Cube"
  AttacherType = Attacher::AttachEngine3D
  Height = 10
  Length = 3
  Placement = pos=(3.3,4,12) rot=(0,0,1;0rad)
  Width = 10
FEATURE [Part::Fillet] Fillet004
  Base = -> Fusion028
  Edges = 1 edges r=2: [Edge25]
FEATURE [Part::Fillet] Fillet005  label="plugHousing046"
  Base = -> Fillet004
  Edges = 1 edges r=2: [Edge8]
FEATURE [Part::Fillet] Fillet006
  Base = -> Box
  Edges = 1 edges r=2: [Edge11]
FEATURE [Part::Box] Box007  label="Cube007"
  AttacherType = Attacher::AttachEngine3D
  Height = 10
  Length = 3
  Placement = pos=(3.3,4,50) rot=(0,0,1;0rad)
  Width = 10
FEATURE [Part::Fillet] Fillet007
  Base = -> Box007
  Edges = 1 edges r=2: [Edge12]
FEATURE [Part::Box] Box008  label="Cube008"
  AttacherType = Attacher::AttachEngine3D
  Height = 28
  Length = 4
  Placement = pos=(5,0,22) rot=(0,0,1;0rad)
  Width = 10
FEATURE [Part::Fillet] Fillet008
  Base = -> Box008
  Edges = 1 edges r=1: [Edge7]
FEATURE [Part::Fillet] Fillet009
  Base = -> Fillet008
  Edges = 1 edges r=2: [Edge5]
FEATURE [Part::Fillet] Fillet010
  Base = -> Fillet009
  Edges = 1 edges r=2: [Edge2]
FEATURE [Sketcher::SketchObject] Sketch009  label="topSketch003"
  FullyConstrained = true
  sketch-geometry (4):
    g0: LineSegment StartX=16.8446 StartY=31.512 StartZ=0 EndX=16.3251 EndY=34.4666 EndZ=0
    g1: ArcOfCircle CenterX=19 CenterY=19.2524 CenterZ=0 NormalX=0 NormalY=0 NormalZ=1 AngleXU=0 Radius=15.4476 StartAngle=1.74483 EndAngle=2.72717
    g2: ArcOfCircle CenterX=19 CenterY=19.2524 CenterZ=0 NormalX=0 NormalY=0 NormalZ=1 AngleXU=0 Radius=12.4476 StartAngle=1.74483 EndAngle=2.73189
    g3: LineSegment StartX=4.86004 StartY=25.4725 StartZ=0 EndX=7.58253 EndY=24.2107 EndZ=0
  constraints (7):
    c: Block(g0)
    c: Coincident(g1,g0)
    c: Coincident(g2,g0)
    c: Coincident(g3,g1)
    c: Coincident(g3,g2)
    c: Block(g1)
    c: Block(g2)
FEATURE [Part::Extrusion] Extrude008
  Base = -> Sketch009
  Dir = (0,0,1)
  DirMode = 2
  FaceMakerClass = Part::FaceMakerBullseye
  LengthFwd = 10
  LengthRev = 0
  Placement = pos=(0,0,31) rot=(0,0,1;0rad)
  Solid = true
  Symmetric = false
FEATURE [Part::Cylinder] Cylinder020
  Angle = 360
  AttacherType = Attacher::AttachEngine3D
  Height = 20
  Placement = pos=(0,0,36.15) rot=(0,0,1;0rad)
  Radius = 8.2
FEATURE [Part::Cylinder] Cylinder021
  Angle = 360
  AttacherType = Attacher::AttachEngine3D
  Height = 10
  Placement = pos=(0,0,36.15) rot=(0,0,1;0rad)
  Radius = 4
FEATURE [Part::MultiFuse] Fusion038  label="removeToCreteHoleForPlugHousing007"
  Placement = pos=(-42,19,36) rot=(0,1,0;1.5708rad)
  Shapes = -> [Cylinder020,Cylinder021]
FEATURE [Part::Cut] Cut011
  Base = -> Extrude008
  Tool = -> Fusion038
FEATURE [Part::Fillet] Fillet011
  Base = -> Cut011
  Edges = 1 edges r=2: [Edge1]
FEATURE [Part::Fillet] Fillet012
  Base = -> Fillet011
  Edges = 1 edges r=2.5: [Edge1]
FEATURE [Part::Fillet] Fillet013
  Base = -> Fillet012
  Edges = 1 edges r=2.5: [Edge2]
FEATURE [Part::Box] Box010  label="Cube010"
  AttacherType = Attacher::AttachEngine3D
  Height = 16
  Length = 8
  Placement = pos=(12.7,31.52,28) rot=(0,0,1;0rad)
  Width = 4
FEATURE [Sketcher::SketchObject] Sketch010  label="topSketch004"
  FullyConstrained = true
  sketch-geometry (4):
    g0: LineSegment StartX=16.8446 StartY=31.512 StartZ=0 EndX=16.3251 EndY=34.4666 EndZ=0
    g1: ArcOfCircle CenterX=19 CenterY=19.2524 CenterZ=0 NormalX=0 NormalY=0 NormalZ=1 AngleXU=0 Radius=15.4476 StartAngle=1.74483 EndAngle=2.72717
    g2: ArcOfCircle CenterX=19 CenterY=19.2524 CenterZ=0 NormalX=0 NormalY=0 NormalZ=1 AngleXU=0 Radius=12.4476 StartAngle=1.74483 EndAngle=2.73189
    g3: LineSegment StartX=4.86004 StartY=25.4725 StartZ=0 EndX=7.58253 EndY=24.2107 EndZ=0
  constraints (7):
    c: Block(g0)
    c: Coincident(g1,g0)
    c: Coincident(g2,g0)
    c: Coincident(g3,g1)
    c: Coincident(g3,g2)
    c: Block(g1)
    c: Block(g2)
FEATURE [Part::Cylinder] Cylinder022
  Angle = 360
  AttacherType = Attacher::AttachEngine3D
  Height = 10
  Placement = pos=(0,0,36.15) rot=(0,0,1;0rad)
  Radius = 4
FEATURE [Sketcher::SketchObject] Sketch011  label="topSketch005"
  FullyConstrained = true
  sketch-geometry (4):
    g0: LineSegment StartX=16.8446 StartY=31.512 StartZ=0 EndX=16.3251 EndY=34.4666 EndZ=0
    g1: ArcOfCircle CenterX=19 CenterY=19.2524 CenterZ=0 NormalX=0 NormalY=0 NormalZ=1 AngleXU=0 Radius=15.4476 StartAngle=1.74483 EndAngle=2.72717
    g2: ArcOfCircle CenterX=19 CenterY=19.2524 CenterZ=0 NormalX=0 NormalY=0 NormalZ=1 AngleXU=0 Radius=12.4476 StartAngle=1.74483 EndAngle=2.73189
    g3: LineSegment StartX=4.86004 StartY=25.4725 StartZ=0 EndX=7.58253 EndY=24.2107 EndZ=0
  constraints (7):
    c: Block(g0)
    c: Coincident(g1,g0)
    c: Coincident(g2,g0)
    c: Coincident(g3,g1)
    c: Coincident(g3,g2)
    c: Block(g1)
    c: Block(g2)
FEATURE [Part::Extrusion] Extrude010
  Base = -> Sketch011
  Dir = (0,0,1)
  DirMode = 2
  FaceMakerClass = Part::FaceMakerBullseye
  LengthFwd = 10.6
  LengthRev = 0
  Placement = pos=(0,0,31) rot=(0,0,1;0rad)
  Solid = true
  Symmetric = false
FEATURE [Part::Cylinder] Cylinder023
  Angle = 360
  AttacherType = Attacher::AttachEngine3D
  Height = 20
  Placement = pos=(0,0,36.15) rot=(0,0,1;0rad)
  Radius = 8.2
FEATURE [Part::MultiFuse] Fusion039  label="removeToCreteHoleForPlugHousing008"
  Placement = pos=(-42,19,36) rot=(0,1,0;1.5708rad)
  Shapes = -> [Cylinder023,Cylinder022]
FEATURE [Part::Cut] Cut012
  Base = -> Extrude010
  Placement = pos=(0,0,-0.3) rot=(0,0,1;0rad)
  Tool = -> Fusion039
FEATURE [Part::Cut] Cut013
  Base = -> Box010
  Tool = -> Cut012
FEATURE [Part::Fillet] Fillet014
  Base = -> Cut013
  Edges = 1 edges r=0.7: [Edge13]
FEATURE [Part::Fillet] Fillet015
  Base = -> Fillet014
  Edges = 1 edges r=0.7: [Edge13]
FEATURE [Part::Fillet] Fillet016
  Base = -> Fillet015
  Edges = 1 edges r=0.7: [Edge16]
FEATURE [Part::Fillet] Fillet017
  Base = -> Fillet016
  Edges = 1 edges r=0.7: [Edge11]
FEATURE [Part::Fillet] Fillet018
  Base = -> Fillet017
  Edges = 1 edges r=0.7: [Edge10]
FEATURE [Part::Fillet] Fillet019
  Base = -> Fillet018
  Edges = 1 edges r=1.2: [Edge5]
FEATURE [Part::Fillet] Fillet020
  Base = -> Fillet019
  Edges = 1 edges r=1.2: [Edge12]
FEATURE [Part::Fillet] Fillet021
  Base = -> Fillet020
  Edges = 1 edges r=2: [Edge1]
  Placement = pos=(0.3,0,0) rot=(0,0,1;0rad)
FEATURE [Part::MultiFuse] Fusion040  label="top005"
  Shapes = -> [Cut008,Fillet021]
FEATURE [Part::MultiFuse] Fusion041  label="wireHolder"
  Shapes = -> [Fusion033,Fillet013]
FEATURE [Part::MultiFuse] Fusion042
  Shapes = -> [Fillet007,Fusion041]
FEATURE [Part::MultiFuse] Fusion043  label="wireHolder001"
  Shapes = -> [Fusion042,Fillet010]
FEATURE [Part::MultiFuse] Fusion044  label="wireHolder002"
  Shapes = -> [Fillet006,Fusion037,Fusion043]
FEATURE [Part::Feature] Face026
  shape: bbox 11 x 6 x 2e-07 mm, 1 faces, 0 solids (baked)
FEATURE [Part::Revolution] Revolve026
  Angle = 360
  Axis = (0,1,0)
  Base = (0,0,0)
  FaceMakerClass = Part::FaceMakerBullseye
  Placement = pos=(30.3,-1,19.7) rot=(0,0,1;0rad)
  Solid = false
  Source = -> Face026
  Symmetric = false
FEATURE [Sketcher::SketchObject] Sketch013  label="topSketch006"
  FullyConstrained = true
  sketch-geometry (13):
    g0: LineSegment StartX=117 StartY=19 StartZ=0 EndX=117 EndY=38 EndZ=0
    g1: ArcOfCircle CenterX=98 CenterY=19 CenterZ=0 NormalX=0 NormalY=0 NormalZ=1 AngleXU=0 Radius=19 StartAngle=5.7297 EndAngle=6.28319
    g2: LineSegment StartX=0 StartY=3 StartZ=0 EndX=0 EndY=19 EndZ=0
    g3: LineSegment StartX=19 StartY=38 StartZ=0 EndX=117 EndY=38 EndZ=0
    g4: ArcOfCircle CenterX=19 CenterY=19 CenterZ=0 NormalX=0 NormalY=0 NormalZ=1 AngleXU=0 Radius=19 StartAngle=1.5708 EndAngle=3.14159
    g5: ArcOfCircle CenterX=19 CenterY=19 CenterZ=0 NormalX=0 NormalY=0 NormalZ=1 AngleXU=0 Radius=16 StartAngle=1.5708 EndAngle=3.14159
    g6: ArcOfCircle CenterX=98 CenterY=19 CenterZ=0 NormalX=0 NormalY=0 NormalZ=1 AngleXU=0 Radius=16 StartAngle=5.60905 EndAngle=6.28319
    g7: LineSegment StartX=114 StartY=19 StartZ=0 EndX=114 EndY=35 EndZ=0
    g8: LineSegment StartX=110.5 StartY=9.01251 StartZ=0 EndX=114.163 EndY=9.01251 EndZ=0
    g9: LineSegment StartX=114 StartY=35 StartZ=0 EndX=19 EndY=35 EndZ=0
    g10: LineSegment StartX=0 StartY=3 StartZ=0 EndX=0 EndY=0 EndZ=0
    g11: LineSegment StartX=3 StartY=0 StartZ=0 EndX=0 EndY=0 EndZ=0
    g12: LineSegment StartX=3 StartY=19 StartZ=0 EndX=3 EndY=0 EndZ=0
  constraints (33):
    c: Vertical(g0)
    c: Distance(g0) = 19
    c: Block(g0)
    c: Coincident(g1,g0)
    c: Block(g1)
    c: Vertical(g2)
    c: Block(g2)
    c: Coincident(g3,g0)
    c: Horizontal(g3)
    c: Distance(g3) = 98
    c: Coincident(g4,g3)
    c: Coincident(g4,g2)
    c: Block(g4)
    c: Coincident(g5,g4)
    c: Coincident(g6,g1)
    c: Block(g6)
    c: Block(g5)
    c: Coincident(g7,g6)
    c: Vertical(g7)
    c: Coincident(g8,g6)
    c: Coincident(g8,g1)
    c: Coincident(g9,g7)
    c: Coincident(g9,g5)
    c: Horizontal(g9)
    c: Tangent(g9,g5)
    c: Coincident(g10,g2)
    c: Distance(g10) = 3
    c: Vertical(g10)
    c: Coincident(g11,g10)
    c: Horizontal(g11)
    c: Coincident(g12,g5)
    c: Coincident(g12,g11)
    c: Vertical(g12)
FEATURE [Part::Extrusion] Extrude011  label="top006"
  Base = -> Sketch013
  Dir = (0,0,1)
  DirMode = 2
  FaceMakerClass = Part::FaceMakerBullseye
  LengthFwd = 72
  LengthRev = 0
  Solid = true
  Symmetric = false
FEATURE [Sketcher::SketchObject] Sketch014
  FullyConstrained = true
  MapMode = 3
  Placement = pos=(0,0,0) rot=(1,0,0;1.5708rad)
  Support = -> [Extrude011]
  sketch-geometry (8):
    g0: Circle CenterX=80.351 CenterY=-67.6202 CenterZ=0 NormalX=0 NormalY=0 NormalZ=1 AngleXU=0 Radius=2
    g1: Circle CenterX=80.351 CenterY=-67.6202 CenterZ=0 NormalX=0 NormalY=0 NormalZ=1 AngleXU=0 Radius=3
    g2: Circle CenterX=80.351 CenterY=-4.92017 CenterZ=0 NormalX=0 NormalY=0 NormalZ=1 AngleXU=0 Radius=2
    g3: Circle CenterX=80.351 CenterY=-4.92017 CenterZ=0 NormalX=0 NormalY=0 NormalZ=1 AngleXU=0 Radius=3
    g4: Circle CenterX=23.851 CenterY=-4.92017 CenterZ=0 NormalX=0 NormalY=0 NormalZ=1 AngleXU=0 Radius=2
    g5: Circle CenterX=23.851 CenterY=-4.92017 CenterZ=0 NormalX=0 NormalY=0 NormalZ=1 AngleXU=0 Radius=3
    g6: Circle CenterX=23.851 CenterY=-67.6202 CenterZ=0 NormalX=0 NormalY=0 NormalZ=1 AngleXU=0 Radius=2
    g7: Circle CenterX=23.851 CenterY=-67.6202 CenterZ=0 NormalX=0 NormalY=0 NormalZ=1 AngleXU=0 Radius=3
  constraints (8):
    c: Block(g3)
    c: Block(g2)
    c: Block(g1)
    c: Block(g0)
    c: Block(g6)
    c: Block(g7)
    c: Block(g4)
    c: Block(g5)
FEATURE [Part::Feature] Face027
  shape: bbox 11 x 6 x 2e-07 mm, 1 faces, 0 solids (baked)
FEATURE [Part::Revolution] Revolve027
  Angle = 360
  Axis = (0,1,0)
  Base = (0,0,0)
  FaceMakerClass = Part::FaceMakerBullseye
  Placement = pos=(30.3,-1,51.7) rot=(0,0,1;0rad)
  Solid = false
  Source = -> Face027
  Symmetric = false
FEATURE [Part::Feature] Face028
  shape: bbox 11 x 6 x 2e-07 mm, 1 faces, 0 solids (baked)
FEATURE [Part::Revolution] Revolve028
  Angle = 360
  Axis = (0,1,0)
  Base = (0,0,0)
  FaceMakerClass = Part::FaceMakerBullseye
  Placement = pos=(62.3,-1,19.7) rot=(0,0,1;0rad)
  Solid = false
  Source = -> Face028
  Symmetric = false
FEATURE [Part::Feature] Face029
  shape: bbox 11 x 6 x 2e-07 mm, 1 faces, 0 solids (baked)
FEATURE [Part::Revolution] Revolve029
  Angle = 360
  Axis = (0,1,0)
  Base = (0,0,0)
  FaceMakerClass = Part::FaceMakerBullseye
  Placement = pos=(62.3,-1,51.7) rot=(0,0,1;0rad)
  Solid = false
  Source = -> Face029
  Symmetric = false
FEATURE [Part::Feature] Wire
  shape: bbox 11 x 5.2 x 2e-07 mm, 0 faces, 0 solids (baked)
FEATURE [Part::Revolution] Revolve030
  Angle = 360
  Axis = (0,1,0)
  Base = (0,0,0)
  FaceMakerClass = Part::FaceMakerBullseye
  Placement = pos=(30.3,38,19.7) rot=(0,0,1;0rad)
  Solid = true
  Source = -> Wire
  Symmetric = false
FEATURE [Part::Feature] Wire001
  shape: bbox 11 x 5.2 x 2e-07 mm, 0 faces, 0 solids (baked)
FEATURE [Part::Revolution] Revolve031
  Angle = 360
  Axis = (0,1,0)
  Base = (0,0,0)
  FaceMakerClass = Part::FaceMakerBullseye
  Placement = pos=(30.3,38,51.7) rot=(0,0,1;0rad)
  Solid = true
  Source = -> Wire001
  Symmetric = false
FEATURE [Part::Feature] Wire002
  shape: bbox 11 x 5.2 x 2e-07 mm, 0 faces, 0 solids (baked)
FEATURE [Part::Revolution] Revolve032
  Angle = 360
  Axis = (0,1,0)
  Base = (0,0,0)
  FaceMakerClass = Part::FaceMakerBullseye
  Placement = pos=(62.3,38,51.7) rot=(0,0,1;0rad)
  Solid = true
  Source = -> Wire002
  Symmetric = false
FEATURE [Part::Feature] Wire003
  shape: bbox 11 x 5.2 x 2e-07 mm, 0 faces, 0 solids (baked)
FEATURE [Part::Revolution] Revolve033
  Angle = 360
  Axis = (0,1,0)
  Base = (0,0,0)
  FaceMakerClass = Part::FaceMakerBullseye
  Placement = pos=(62.3,38,19.7) rot=(0,0,1;0rad)
  Solid = true
  Source = -> Wire003
  Symmetric = false
FEATURE [Part::MultiFuse] Fusion045  label="altRandScrewHousing"
  Shapes = -> [Revolve029,Revolve027,Revolve028,Revolve026]
FEATURE [Part::MultiFuse] Fusion046  label="fanScrewHousing"
  Shapes = -> [Revolve033,Revolve032,Revolve031,Revolve030]
FEATURE [Sketcher::SketchObject] Sketch015
  FullyConstrained = true
  sketch-geometry (17):
    g0: Circle CenterX=-3.5 CenterY=23.5 CenterZ=0 NormalX=0 NormalY=0 NormalZ=1 AngleXU=0 Radius=1
    g1: Circle CenterX=-1 CenterY=15.25 CenterZ=0 NormalX=0 NormalY=0 NormalZ=1 AngleXU=0 Radius=1
    g2: Circle CenterX=-3.5 CenterY=7 CenterZ=0 NormalX=0 NormalY=0 NormalZ=1 AngleXU=0 Radius=1
    g3: BSplineCurve PolesCount=3 KnotsCount=2 Degree=2 IsPeriodic=0
    g4: GeomPoint X=-3.5 Y=23.5 Z=0
    g5: GeomPoint X=-3.5 Y=7 Z=0
    g6: Circle CenterX=-4.8 CenterY=30.5 CenterZ=0 NormalX=0 NormalY=0 NormalZ=1 AngleXU=0 Radius=1
    g7: Circle CenterX=-3.5 CenterY=30.5 CenterZ=0 NormalX=0 NormalY=0 NormalZ=1 AngleXU=0 Radius=1
    g8: Circle CenterX=-3.5 CenterY=29.2 CenterZ=0 NormalX=0 NormalY=0 NormalZ=1 AngleXU=0 Radius=1
    g9: BSplineCurve PolesCount=3 KnotsCount=2 Degree=2 IsPeriodic=0
    g10: GeomPoint X=-4.8 Y=30.5 Z=0
    g11: GeomPoint X=-3.5 Y=29.2 Z=0
    g12: LineSegment StartX=-3.5 StartY=29.2 StartZ=0 EndX=-3.5 EndY=23.5 EndZ=0
    g13: LineSegment StartX=-4.8 StartY=30.5 StartZ=0 EndX=0 EndY=30.5 EndZ=0
    g14: LineSegment StartX=-3.5 StartY=0.3 StartZ=0 EndX=0 EndY=0.3 EndZ=0
    g15: LineSegment StartX=-3.5 StartY=0.3 StartZ=0 EndX=-3.5 EndY=7 EndZ=0
    g16: LineSegment StartX=0 StartY=0.3 StartZ=0 EndX=0 EndY=30.5 EndZ=0
  constraints (33):
    c: Weight(g0) = 1
    c: Equal(g0,g1)
    c: Equal(g0,g2)
    c: InternalAlignment(g0,g3)
    c: InternalAlignment(g1,g3)
    c: InternalAlignment(g2,g3)
    c: InternalAlignment(g4,g3)
    c: InternalAlignment(g5,g3)
    c: Block(g3)
    c: Weight(g6) = 1
    c: Equal(g6,g7)
    c: Equal(g6,g8)
    c: InternalAlignment(g6,g9)
    c: InternalAlignment(g7,g9)
    c: InternalAlignment(g8,g9)
    c: InternalAlignment(g10,g9)
    c: InternalAlignment(g11,g9)
    c: Block(g9)
    c: Coincident(g12,g9)
    c: Coincident(g12,g3)
    c: Vertical(g12)
    c: Coincident(g13,g9)
    c: Horizontal(g13)
    c: Distance(g13) = 4.8
    c: Horizontal(g14)
    c: Block(g14)
    c: Coincident(g15,g14)
    c: Coincident(g15,g3)
    c: Vertical(g15)
    c: Coincident(g16,g14)
    c: Coincident(g16,g13)
    c: Vertical(g16)
    c: Tangent(g16,g1)
FEATURE [Sketcher::SketchObject] Sketch016
  FullyConstrained = true
  sketch-geometry (16):
    g0: Circle CenterX=-3.5 CenterY=23.5 CenterZ=0 NormalX=0 NormalY=0 NormalZ=1 AngleXU=0 Radius=1
    g1: Circle CenterX=-1 CenterY=15.25 CenterZ=0 NormalX=0 NormalY=0 NormalZ=1 AngleXU=0 Radius=1
    g2: Circle CenterX=-3.5 CenterY=7 CenterZ=0 NormalX=0 NormalY=0 NormalZ=1 AngleXU=0 Radius=1
    g3: BSplineCurve PolesCount=3 KnotsCount=2 Degree=2 IsPeriodic=0
    g4: GeomPoint X=-3.5 Y=23.5 Z=0
    g5: GeomPoint X=-3.5 Y=7 Z=0
    g6: LineSegment StartX=-3.5 StartY=28.2 StartZ=0 EndX=-3.5 EndY=23.5 EndZ=0
    g7: LineSegment StartX=0 StartY=29.5 StartZ=0 EndX=0 EndY=30 EndZ=0
    g8: LineSegment StartX=-3.5 StartY=28.2 StartZ=0 EndX=-3.5 EndY=30 EndZ=0
    g9: LineSegment StartX=0 StartY=30 StartZ=0 EndX=0 EndY=30.5 EndZ=0
    g10: LineSegment StartX=0 StartY=30.5 StartZ=0 EndX=-3.5 EndY=30.5 EndZ=0
    g11: LineSegment StartX=-3.5 StartY=30.5 StartZ=0 EndX=-3.5 EndY=30 EndZ=0
    g12: LineSegment StartX=0 StartY=29.5 StartZ=0 EndX=0 EndY=5 EndZ=0
    g13: LineSegment StartX=-3.5 StartY=0.3 StartZ=0 EndX=-3.5 EndY=7 EndZ=0
    g14: LineSegment StartX=-3.5 StartY=0.3 StartZ=0 EndX=0 EndY=0.3 EndZ=0
    g15: LineSegment StartX=0 StartY=5 StartZ=0 EndX=0 EndY=0.3 EndZ=0
  constraints (39):
    c: Weight(g0) = 1
    c: Equal(g0,g1)
    c: Equal(g0,g2)
    c: InternalAlignment(g0,g3)
    c: InternalAlignment(g1,g3)
    c: InternalAlignment(g2,g3)
    c: InternalAlignment(g4,g3)
    c: InternalAlignment(g5,g3)
    c: Block(g3)
    c: Coincident(g6,g3)
    c: Vertical(g6)
    c: Vertical(g7)
    c: Distance(g7) = 0.5
    c: Coincident(g8,g6)
    c: Vertical(g8)
    c: Block(g6)
    c: Block(g7)
    c: Vertical(g9)
    c: Equal(g7,g9) = 0.5
    c: Block(g9)
    c: Coincident(g9,g7)
    c: Horizontal(g10)
    c: Coincident(g10,g9)
    c: Coincident(g11,g10)
    c: Coincident(g11,g8)
    c: Vertical(g11)
    c: Block(g11)
    c: Coincident(g12,g7)
    c: Vertical(g12)
    c: Coincident(g13,g3)
    c: Vertical(g13)
    c: Distance(g13) = 6.7
    c: Coincident(g14,g13)
    c: Horizontal(g14)
    c: Block(g14)
    c: Coincident(g15,g12)
    c: Coincident(g15,g14)
    c: Vertical(g15)
    c: Block(g15)
FEATURE [Sketcher::SketchObject] Sketch017
  FullyConstrained = true
  sketch-geometry (11):
    g0: LineSegment StartX=-3.5 StartY=1e-16 StartZ=0 EndX=-1.6 EndY=1e-16 EndZ=0
    g1: LineSegment StartX=-1.6 StartY=1e-16 StartZ=0 EndX=-1.6 EndY=1.5 EndZ=0
    g2: LineSegment StartX=-3.5 StartY=1.5 StartZ=0 EndX=-1.6 EndY=1.5 EndZ=0
    g3: LineSegment StartX=-3.5 StartY=1e-16 StartZ=0 EndX=-4.8 EndY=1e-16 EndZ=0
    g4: Circle CenterX=-3.5 CenterY=1.3 CenterZ=0 NormalX=0 NormalY=0 NormalZ=1 AngleXU=0 Radius=1
    g5: Circle CenterX=-3.5 CenterY=1e-16 CenterZ=0 NormalX=0 NormalY=0 NormalZ=1 AngleXU=0 Radius=1
    g6: Circle CenterX=-4.8 CenterY=1e-16 CenterZ=0 NormalX=0 NormalY=0 NormalZ=1 AngleXU=0 Radius=1
    g7: BSplineCurve PolesCount=3 KnotsCount=2 Degree=2 IsPeriodic=0
    g8: GeomPoint X=-3.5 Y=1.3 Z=0
    g9: GeomPoint X=-4.8 Y=1e-16 Z=0
    g10: LineSegment StartX=-3.5 StartY=1.3 StartZ=0 EndX=-3.5 EndY=1.5 EndZ=0
  constraints (24):
    c: Horizontal(g0)
    c: Distance(g0) = 1.9
    c: Block(g0)
    c: Coincident(g1,g0)
    c: Vertical(g1)
    c: Coincident(g2,g1)
    c: Horizontal(g2)
    c: Coincident(g3,g0)
    c: Horizontal(g3)
    c: Distance(g3) = 1.3
    c: Weight(g4) = 1
    c: Equal(g4,g5)
    c: Coincident(g5,g0)
    c: Equal(g4,g6)
    c: Coincident(g7,g3)
    c: InternalAlignment(g4,g7)
    c: InternalAlignment(g5,g7)
    c: InternalAlignment(g6,g7)
    c: InternalAlignment(g8,g7)
    c: InternalAlignment(g9,g7)
    c: Coincident(g10,g7)
    c: Coincident(g10,g2)
    c: Vertical(g10)
    c: Block(g10)
FEATURE [Part::Feature] Face035
  shape: bbox 3.2 x 1.5 x 2e-07 mm, 1 faces, 0 solids (baked)
FEATURE [Part::Revolution] Revolve039  label="backCaseScrewRetainer"
  Angle = 360
  Axis = (0,1,0)
  Base = (0,0,0)
  FaceMakerClass = Part::FaceMakerBullseye
  Placement = pos=(12.5,3,62) rot=(0,0,1;0rad)
  Solid = false
  Source = -> Face035
  Symmetric = false
FEATURE [Part::Feature] Face036
  shape: bbox 3.2 x 1.5 x 2e-07 mm, 1 faces, 0 solids (baked)
FEATURE [Part::Feature] Face039
  shape: bbox 4.8 x 30.2 x 2e-07 mm, 1 faces, 0 solids (baked)
FEATURE [Part::Revolution] Revolve043  label="frontCaseScrewPost002"
  Angle = 360
  Axis = (0,1,0)
  Base = (0,0,0)
  FaceMakerClass = Part::FaceMakerBullseye
  Placement = pos=(89.5,4.5,3.5) rot=(0,0,1;0rad)
  Solid = false
  Source = -> Face039
  Symmetric = false
FEATURE [Part::Feature] Face042
  shape: bbox 4.8 x 30.2 x 2e-07 mm, 1 faces, 0 solids (baked)
FEATURE [Part::Revolution] Revolve046  label="frontCaseScrewPost003"
  Angle = 360
  Axis = (0,1,0)
  Base = (0,0,0)
  FaceMakerClass = Part::FaceMakerBullseye
  Placement = pos=(89.5,4.5,68.5) rot=(0,0,1;0rad)
  Solid = false
  Source = -> Face042
  Symmetric = false
FEATURE [Part::Feature] Face043
  shape: bbox 3.2 x 1.5 x 2e-07 mm, 1 faces, 0 solids (baked)
FEATURE [Part::Revolution] Revolve047  label="frontCaseScrewRetainer002"
  Angle = 360
  Axis = (0,1,0)
  Base = (0,0,0)
  FaceMakerClass = Part::FaceMakerBullseye
  Placement = pos=(89.5,3,68.5) rot=(0,0,1;0rad)
  Solid = false
  Source = -> Face043
  Symmetric = false
FEATURE [Part::Feature] Face044
  shape: bbox 3.2 x 1.5 x 2e-07 mm, 1 faces, 0 solids (baked)
FEATURE [Part::Revolution] Revolve048  label="frontCaseScrewRetainer003"
  Angle = 360
  Axis = (0,1,0)
  Base = (0,0,0)
  FaceMakerClass = Part::FaceMakerBullseye
  Placement = pos=(89.5,3,3.5) rot=(0,0,1;0rad)
  Solid = false
  Source = -> Face044
  Symmetric = false
FEATURE [App::MeasureDistance] Distance002  label="Distance: 1.67 mm"
  Distance = 1.66921
  P1 = (99.2361,4.7524,71.7)
  P2 = (99.2347,6.42161,71.7)
FEATURE [Sketcher::SketchObject] Sketch018
  FullyConstrained = true
  sketch-geometry (7):
    g0: LineSegment StartX=0 StartY=0 StartZ=0 EndX=0 EndY=6 EndZ=0
    g1: Circle CenterX=0 CenterY=0 CenterZ=0 NormalX=0 NormalY=0 NormalZ=1 AngleXU=0 Radius=1
    g2: Circle CenterX=8 CenterY=6 CenterZ=0 NormalX=0 NormalY=0 NormalZ=1 AngleXU=0 Radius=1
    g3: BSplineCurve PolesCount=3 KnotsCount=2 Degree=2 IsPeriodic=0
    g4: GeomPoint X=0 Y=0 Z=0
    g5: GeomPoint X=8 Y=6 Z=0
    g6: LineSegment StartX=0 StartY=6 StartZ=0 EndX=8 EndY=6 EndZ=0
  constraints (14):
    c: Coincident(g0,g-1)
    c: Distance(g0) = 6
    c: Vertical(g0)
    c: Coincident(g3,g0)
    c: Weight(g1) = 1
    c: Equal(g1,g2)
    c: InternalAlignment(g1,g3)
    c: InternalAlignment(g2,g3)
    c: InternalAlignment(g4,g3)
    c: InternalAlignment(g5,g3)
    c: Block(g3)
    c: Coincident(g6,g0)
    c: Coincident(g6,g3)
    c: Horizontal(g6)
FEATURE [Part::Extrusion] Extrude012  label="caseScrewPillarBracket"
  Base = -> Sketch018
  Dir = (0,0,1)
  DirMode = 2
  FaceMakerClass = Part::FaceMakerBullseye
  LengthFwd = 2.4
  LengthRev = 0
  Placement = pos=(15.76,29,8.8) rot=(0,1,0;0rad)
  Solid = true
  Symmetric = false
FEATURE [Sketcher::SketchObject] Sketch019
  FullyConstrained = true
  sketch-geometry (7):
    g0: LineSegment StartX=0 StartY=0 StartZ=0 EndX=0 EndY=6 EndZ=0
    g1: Circle CenterX=0 CenterY=0 CenterZ=0 NormalX=0 NormalY=0 NormalZ=1 AngleXU=0 Radius=1
    g2: Circle CenterX=8 CenterY=6 CenterZ=0 NormalX=0 NormalY=0 NormalZ=1 AngleXU=0 Radius=1
    g3: BSplineCurve PolesCount=3 KnotsCount=2 Degree=2 IsPeriodic=0
    g4: GeomPoint X=0 Y=0 Z=0
    g5: GeomPoint X=8 Y=6 Z=0
    g6: LineSegment StartX=0 StartY=6 StartZ=0 EndX=8 EndY=6 EndZ=0
  constraints (14):
    c: Coincident(g0,g-1)
    c: Distance(g0) = 6
    c: Vertical(g0)
    c: Coincident(g3,g0)
    c: Weight(g1) = 1
    c: Equal(g1,g2)
    c: InternalAlignment(g1,g3)
    c: InternalAlignment(g2,g3)
    c: InternalAlignment(g4,g3)
    c: InternalAlignment(g5,g3)
    c: Block(g3)
    c: Coincident(g6,g0)
    c: Coincident(g6,g3)
    c: Horizontal(g6)
FEATURE [Part::Extrusion] Extrude013  label="caseScrewPillarBracket001"
  Base = -> Sketch019
  Dir = (0,0,1)
  DirMode = 2
  FaceMakerClass = Part::FaceMakerBullseye
  LengthFwd = 2.4
  LengthRev = 0
  Placement = pos=(15.76,29,60.8) rot=(0,0,1;0rad)
  Solid = true
  Symmetric = false
FEATURE [Sketcher::SketchObject] Sketch020
  FullyConstrained = true
  sketch-geometry (7):
    g0: LineSegment StartX=0 StartY=0 StartZ=0 EndX=0 EndY=6 EndZ=0
    g1: Circle CenterX=0 CenterY=0 CenterZ=0 NormalX=0 NormalY=0 NormalZ=1 AngleXU=0 Radius=1
    g2: Circle CenterX=8 CenterY=6 CenterZ=0 NormalX=0 NormalY=0 NormalZ=1 AngleXU=0 Radius=1
    g3: BSplineCurve PolesCount=3 KnotsCount=2 Degree=2 IsPeriodic=0
    g4: GeomPoint X=0 Y=0 Z=0
    g5: GeomPoint X=8 Y=6 Z=0
    g6: LineSegment StartX=0 StartY=6 StartZ=0 EndX=8 EndY=6 EndZ=0
  constraints (14):
    c: Coincident(g0,g-1)
    c: Distance(g0) = 6
    c: Vertical(g0)
    c: Coincident(g3,g0)
    c: Weight(g1) = 1
    c: Equal(g1,g2)
    c: InternalAlignment(g1,g3)
    c: InternalAlignment(g2,g3)
    c: InternalAlignment(g4,g3)
    c: InternalAlignment(g5,g3)
    c: Block(g3)
    c: Coincident(g6,g0)
    c: Coincident(g6,g3)
    c: Horizontal(g6)
FEATURE [Part::Extrusion] Extrude014  label="caseScrewPillarBracket002"
  Base = -> Sketch020
  Dir = (0,0,1)
  DirMode = 2
  FaceMakerClass = Part::FaceMakerBullseye
  LengthFwd = 2.4
  LengthRev = 0
  Placement = pos=(13.7,29,13.26) rot=(0,-1,0;1.5708rad)
  Solid = true
  Symmetric = false
FEATURE [Sketcher::SketchObject] Sketch021
  FullyConstrained = true
  sketch-geometry (7):
    g0: LineSegment StartX=0 StartY=0 StartZ=0 EndX=0 EndY=6 EndZ=0
    g1: Circle CenterX=0 CenterY=0 CenterZ=0 NormalX=0 NormalY=0 NormalZ=1 AngleXU=0 Radius=1
    g2: Circle CenterX=8 CenterY=6 CenterZ=0 NormalX=0 NormalY=0 NormalZ=1 AngleXU=0 Radius=1
    g3: BSplineCurve PolesCount=3 KnotsCount=2 Degree=2 IsPeriodic=0
    g4: GeomPoint X=0 Y=0 Z=0
    g5: GeomPoint X=8 Y=6 Z=0
    g6: LineSegment StartX=0 StartY=6 StartZ=0 EndX=8 EndY=6 EndZ=0
  constraints (14):
    c: Coincident(g0,g-1)
    c: Distance(g0) = 6
    c: Vertical(g0)
    c: Coincident(g3,g0)
    c: Weight(g1) = 1
    c: Equal(g1,g2)
    c: InternalAlignment(g1,g3)
    c: InternalAlignment(g2,g3)
    c: InternalAlignment(g4,g3)
    c: InternalAlignment(g5,g3)
    c: Block(g3)
    c: Coincident(g6,g0)
    c: Coincident(g6,g3)
    c: Horizontal(g6)
FEATURE [Part::Extrusion] Extrude015  label="caseScrewPillarBracket003"
  Base = -> Sketch021
  Dir = (0,0,1)
  DirMode = 2
  FaceMakerClass = Part::FaceMakerBullseye
  LengthFwd = 2.4
  LengthRev = 0
  Placement = pos=(11.3,29,58.74) rot=(0,1,0;1.5708rad)
  Solid = true
  Symmetric = false
FEATURE [Sketcher::SketchObject] Sketch022
  FullyConstrained = true
  sketch-geometry (7):
    g0: LineSegment StartX=0 StartY=0 StartZ=0 EndX=0 EndY=6 EndZ=0
    g1: Circle CenterX=0 CenterY=0 CenterZ=0 NormalX=0 NormalY=0 NormalZ=1 AngleXU=0 Radius=1
    g2: Circle CenterX=8 CenterY=6 CenterZ=0 NormalX=0 NormalY=0 NormalZ=1 AngleXU=0 Radius=1
    g3: BSplineCurve PolesCount=3 KnotsCount=2 Degree=2 IsPeriodic=0
    g4: GeomPoint X=0 Y=0 Z=0
    g5: GeomPoint X=8 Y=6 Z=0
    g6: LineSegment StartX=0 StartY=6 StartZ=0 EndX=8 EndY=6 EndZ=0
  constraints (14):
    c: Coincident(g0,g-1)
    c: Distance(g0) = 6
    c: Vertical(g0)
    c: Coincident(g3,g0)
    c: Weight(g1) = 1
    c: Equal(g1,g2)
    c: InternalAlignment(g1,g3)
    c: InternalAlignment(g2,g3)
    c: InternalAlignment(g4,g3)
    c: InternalAlignment(g5,g3)
    c: Block(g3)
    c: Coincident(g6,g0)
    c: Coincident(g6,g3)
    c: Horizontal(g6)
FEATURE [Part::Extrusion] Extrude016  label="caseScrewPillarBracket004"
  Base = -> Sketch022
  Dir = (0,0,1)
  DirMode = 2
  FaceMakerClass = Part::FaceMakerBullseye
  LengthFwd = 2.4
  LengthRev = 0
  Placement = pos=(88.3,29,65.23) rot=(0,1,0;1.5708rad)
  Solid = true
  Symmetric = false
FEATURE [Sketcher::SketchObject] Sketch023
  FullyConstrained = true
  sketch-geometry (7):
    g0: LineSegment StartX=0 StartY=0 StartZ=0 EndX=0 EndY=6 EndZ=0
    g1: Circle CenterX=0 CenterY=0 CenterZ=0 NormalX=0 NormalY=0 NormalZ=1 AngleXU=0 Radius=1
    g2: Circle CenterX=8 CenterY=6 CenterZ=0 NormalX=0 NormalY=0 NormalZ=1 AngleXU=0 Radius=1
    g3: BSplineCurve PolesCount=3 KnotsCount=2 Degree=2 IsPeriodic=0
    g4: GeomPoint X=0 Y=0 Z=0
    g5: GeomPoint X=8 Y=6 Z=0
    g6: LineSegment StartX=0 StartY=6 StartZ=0 EndX=8 EndY=6 EndZ=0
  constraints (14):
    c: Coincident(g0,g-1)
    c: Distance(g0) = 6
    c: Vertical(g0)
    c: Coincident(g3,g0)
    c: Weight(g1) = 1
    c: Equal(g1,g2)
    c: InternalAlignment(g1,g3)
    c: InternalAlignment(g2,g3)
    c: InternalAlignment(g4,g3)
    c: InternalAlignment(g5,g3)
    c: Block(g3)
    c: Coincident(g6,g0)
    c: Coincident(g6,g3)
    c: Horizontal(g6)
FEATURE [Part::Extrusion] Extrude017  label="caseScrewPillarBracket005"
  Base = -> Sketch023
  Dir = (0,0,1)
  DirMode = 2
  FaceMakerClass = Part::FaceMakerBullseye
  LengthFwd = 2.4
  LengthRev = 0
  Placement = pos=(90.7,29,6.77) rot=(0,-1,0;1.5708rad)
  Solid = true
  Symmetric = false
FEATURE [Sketcher::SketchObject] Sketch024
  FullyConstrained = true
  sketch-geometry (7):
    g0: LineSegment StartX=0 StartY=0 StartZ=0 EndX=0 EndY=6 EndZ=0
    g1: Circle CenterX=0 CenterY=0 CenterZ=0 NormalX=0 NormalY=0 NormalZ=1 AngleXU=0 Radius=1
    g2: Circle CenterX=8 CenterY=6 CenterZ=0 NormalX=0 NormalY=0 NormalZ=1 AngleXU=0 Radius=1
    g3: BSplineCurve PolesCount=3 KnotsCount=2 Degree=2 IsPeriodic=0
    g4: GeomPoint X=0 Y=0 Z=0
    g5: GeomPoint X=8 Y=6 Z=0
    g6: LineSegment StartX=0 StartY=6 StartZ=0 EndX=8 EndY=6 EndZ=0
  constraints (14):
    c: Coincident(g0,g-1)
    c: Distance(g0) = 6
    c: Vertical(g0)
    c: Coincident(g3,g0)
    c: Weight(g1) = 1
    c: Equal(g1,g2)
    c: InternalAlignment(g1,g3)
    c: InternalAlignment(g2,g3)
    c: InternalAlignment(g4,g3)
    c: InternalAlignment(g5,g3)
    c: Block(g3)
    c: Coincident(g6,g0)
    c: Coincident(g6,g3)
    c: Horizontal(g6)
FEATURE [Part::Extrusion] Extrude018  label="caseScrewPillarBracket006"
  Base = -> Sketch024
  Dir = (0,0,1)
  DirMode = 2
  FaceMakerClass = Part::FaceMakerBullseye
  LengthFwd = 2.4
  LengthRev = 0
  Placement = pos=(103.7,29,6.77) rot=(0,-1,0;1.5708rad)
  Solid = true
  Symmetric = false
FEATURE [Sketcher::SketchObject] Sketch025
  FullyConstrained = true
  sketch-geometry (7):
    g0: LineSegment StartX=0 StartY=0 StartZ=0 EndX=0 EndY=6 EndZ=0
    g1: Circle CenterX=0 CenterY=0 CenterZ=0 NormalX=0 NormalY=0 NormalZ=1 AngleXU=0 Radius=1
    g2: Circle CenterX=8 CenterY=6 CenterZ=0 NormalX=0 NormalY=0 NormalZ=1 AngleXU=0 Radius=1
    g3: BSplineCurve PolesCount=3 KnotsCount=2 Degree=2 IsPeriodic=0
    g4: GeomPoint X=0 Y=0 Z=0
    g5: GeomPoint X=8 Y=6 Z=0
    g6: LineSegment StartX=0 StartY=6 StartZ=0 EndX=8 EndY=6 EndZ=0
  constraints (14):
    c: Coincident(g0,g-1)
    c: Distance(g0) = 6
    c: Vertical(g0)
    c: Coincident(g3,g0)
    c: Weight(g1) = 1
    c: Equal(g1,g2)
    c: InternalAlignment(g1,g3)
    c: InternalAlignment(g2,g3)
    c: InternalAlignment(g4,g3)
    c: InternalAlignment(g5,g3)
    c: Block(g3)
    c: Coincident(g6,g0)
    c: Coincident(g6,g3)
    c: Horizontal(g6)
FEATURE [Part::Extrusion] Extrude019  label="caseScrewPillarBracket007"
  Base = -> Sketch025
  Dir = (0,0,1)
  DirMode = 2
  FaceMakerClass = Part::FaceMakerBullseye
  LengthFwd = 2.4
  LengthRev = 0
  Placement = pos=(101.3,29,65.23) rot=(0,1,0;1.5708rad)
  Solid = true
  Symmetric = false
FEATURE [Part::Box] Box011  label="frontCaseScrewPillarBracket"
  AttacherType = Attacher::AttachEngine3D
  Height = 2.4
  Length = 16
  Placement = pos=(87,28,2.3) rot=(0,0,1;0rad)
  Width = 7
FEATURE [Part::Box] Box012  label="frontCaseScrewPillarBracket001"
  AttacherType = Attacher::AttachEngine3D
  Height = 2.4
  Length = 16
  Placement = pos=(87,28,67.3) rot=(0,0,1;0rad)
  Width = 7
FEATURE [Sketcher::SketchObject] Sketch026
  FullyConstrained = true
  sketch-geometry (17):
    g0: Circle CenterX=-3.5 CenterY=23.5 CenterZ=0 NormalX=0 NormalY=0 NormalZ=1 AngleXU=0 Radius=1
    g1: Circle CenterX=-1 CenterY=15.25 CenterZ=0 NormalX=0 NormalY=0 NormalZ=1 AngleXU=0 Radius=1
    g2: Circle CenterX=-3.5 CenterY=7 CenterZ=0 NormalX=0 NormalY=0 NormalZ=1 AngleXU=0 Radius=1
    g3: BSplineCurve PolesCount=3 KnotsCount=2 Degree=2 IsPeriodic=0
    g4: GeomPoint X=-3.5 Y=23.5 Z=0
    g5: GeomPoint X=-3.5 Y=7 Z=0
    g6: Circle CenterX=-4.8 CenterY=30.5 CenterZ=0 NormalX=0 NormalY=0 NormalZ=1 AngleXU=0 Radius=1
    g7: Circle CenterX=-3.5 CenterY=30.5 CenterZ=0 NormalX=0 NormalY=0 NormalZ=1 AngleXU=0 Radius=1
    g8: Circle CenterX=-3.5 CenterY=29.2 CenterZ=0 NormalX=0 NormalY=0 NormalZ=1 AngleXU=0 Radius=1
    g9: BSplineCurve PolesCount=3 KnotsCount=2 Degree=2 IsPeriodic=0
    g10: GeomPoint X=-4.8 Y=30.5 Z=0
    g11: GeomPoint X=-3.5 Y=29.2 Z=0
    g12: LineSegment StartX=-3.5 StartY=29.2 StartZ=0 EndX=-3.5 EndY=23.5 EndZ=0
    g13: LineSegment StartX=-4.8 StartY=30.5 StartZ=0 EndX=0 EndY=30.5 EndZ=0
    g14: LineSegment StartX=-3.5 StartY=5 StartZ=0 EndX=-3.5 EndY=7 EndZ=0
    g15: LineSegment StartX=0 StartY=5 StartZ=0 EndX=0 EndY=30.5 EndZ=0
    g16: LineSegment StartX=-3.5 StartY=5 StartZ=0 EndX=0 EndY=5 EndZ=0
  constraints (33):
    c: Weight(g0) = 1
    c: Equal(g0,g1)
    c: Equal(g0,g2)
    c: InternalAlignment(g0,g3)
    c: InternalAlignment(g1,g3)
    c: InternalAlignment(g2,g3)
    c: InternalAlignment(g4,g3)
    c: InternalAlignment(g5,g3)
    c: Block(g3)
    c: Weight(g6) = 1
    c: Equal(g6,g7)
    c: Equal(g6,g8)
    c: InternalAlignment(g6,g9)
    c: InternalAlignment(g7,g9)
    c: InternalAlignment(g8,g9)
    c: InternalAlignment(g10,g9)
    c: InternalAlignment(g11,g9)
    c: Block(g9)
    c: Coincident(g12,g9)
    c: Coincident(g12,g3)
    c: Vertical(g12)
    c: Coincident(g13,g9)
    c: Horizontal(g13)
    c: Distance(g13) = 4.8
    c: Coincident(g14,g3)
    c: Vertical(g14)
    c: Coincident(g15,g13)
    c: Vertical(g15)
    c: Tangent(g15,g1)
    c: Distance(g14) = 2
    c: Coincident(g16,g14)
    c: Horizontal(g16)
    c: Coincident(g15,g16)
FEATURE [Part::Feature] Face050
  shape: bbox 4.8 x 25.5 x 2e-07 mm, 1 faces, 0 solids (baked)
FEATURE [Part::Revolution] Revolve054  label="moreFrontCaseScrewPost001"
  Angle = 360
  Axis = (0,1,0)
  Base = (0,0,0)
  FaceMakerClass = Part::FaceMakerBullseye
  Placement = pos=(102.5,4.5,3.5) rot=(0,0,1;0rad)
  Solid = false
  Source = -> Face050
  Symmetric = false
FEATURE [Part::Feature] Face051
  shape: bbox 4.8 x 25.5 x 2e-07 mm, 1 faces, 0 solids (baked)
FEATURE [Part::Revolution] Revolve055  label="moreFrontCaseScrewPost002"
  Angle = 360
  Axis = (0,1,0)
  Base = (0,0,0)
  FaceMakerClass = Part::FaceMakerBullseye
  Placement = pos=(102.5,4.5,68.5) rot=(0,0,1;0rad)
  Solid = false
  Source = -> Face051
  Symmetric = false
FEATURE [Sketcher::SketchObject] Sketch027
  FullyConstrained = true
  sketch-geometry (10):
    g0: LineSegment StartX=-1.6 StartY=4.7 StartZ=0 EndX=-1.6 EndY=1.7 EndZ=0
    g1: LineSegment StartX=-3.5 StartY=4.7 StartZ=0 EndX=-1.6 EndY=4.7 EndZ=0
    g2: LineSegment StartX=-1.6 StartY=1.7 StartZ=0 EndX=-1.6 EndY=1.5 EndZ=0
    g3: LineSegment StartX=-1.6 StartY=1.5 StartZ=0 EndX=-5.2 EndY=1.5 EndZ=0
    g4: Circle CenterX=-3.5 CenterY=4.7 CenterZ=0 NormalX=0 NormalY=0 NormalZ=1 AngleXU=0 Radius=1
    g5: Circle CenterX=-3.59627 CenterY=2.99743 CenterZ=0 NormalX=0 NormalY=0 NormalZ=1 AngleXU=0 Radius=1
    g6: Circle CenterX=-5.2 CenterY=1.5 CenterZ=0 NormalX=0 NormalY=0 NormalZ=1 AngleXU=0 Radius=1
    g7: BSplineCurve PolesCount=3 KnotsCount=2 Degree=2 IsPeriodic=0
    g8: GeomPoint X=-3.5 Y=4.7 Z=0
    g9: GeomPoint X=-5.2 Y=1.5 Z=0
  constraints (23):
    c: Vertical(g0)
    c: Distance(g0) = 3
    c: Coincident(g1,g0)
    c: Horizontal(g1)
    c: Block(g0)
    c: Block(g1)
    c: Coincident(g2,g0)
    c: Vertical(g2)
    c: Distance(g2) = 0.2
    c: Coincident(g3,g2)
    c: Horizontal(g3)
    c: Block(g3)
    c: Coincident(g7,g1)
    c: Weight(g4) = 1
    c: Equal(g4,g5)
    c: Equal(g4,g6)
    c: Coincident(g7,g3)
    c: InternalAlignment(g4,g7)
    c: InternalAlignment(g5,g7)
    c: InternalAlignment(g6,g7)
    c: InternalAlignment(g8,g7)
    c: InternalAlignment(g9,g7)
    c: Block(g7)
FEATURE [Sketcher::SketchObject] Sketch028
  FullyConstrained = true
  sketch-geometry (18):
    g0: LineSegment StartX=0 StartY=3e-16 StartZ=0 EndX=0 EndY=1.7 EndZ=0
    g1: LineSegment StartX=-3.5 StartY=0 StartZ=0 EndX=-3.5 EndY=0.9 EndZ=0
    g2: Circle CenterX=-2.7 CenterY=1.7 CenterZ=0 NormalX=0 NormalY=0 NormalZ=1 AngleXU=0 Radius=1
    g3: Circle CenterX=-3.5 CenterY=1.7 CenterZ=0 NormalX=0 NormalY=0 NormalZ=1 AngleXU=0 Radius=1
    g4: Circle CenterX=-3.5 CenterY=0.9 CenterZ=0 NormalX=0 NormalY=0 NormalZ=1 AngleXU=0 Radius=1
    g5: BSplineCurve PolesCount=3 KnotsCount=2 Degree=2 IsPeriodic=0
    g6: GeomPoint X=-2.7 Y=1.7 Z=0
    g7: GeomPoint X=-3.5 Y=0.9 Z=0
    g8: LineSegment StartX=-3.5 StartY=0 StartZ=0 EndX=-3.5 EndY=-7 EndZ=0
    g9: LineSegment StartX=0 StartY=3e-16 StartZ=0 EndX=0 EndY=-7 EndZ=0
    g10: LineSegment StartX=-3.5 StartY=-7 StartZ=0 EndX=0 EndY=-7 EndZ=0
    g11: LineSegment StartX=-2.7 StartY=1.7 StartZ=0 EndX=-1.6 EndY=1.7 EndZ=0
    g12: LineSegment StartX=0 StartY=1.7 StartZ=0 EndX=0 EndY=4.5 EndZ=0
    g13: LineSegment StartX=0 StartY=4.5 StartZ=0 EndX=0 EndY=10.8 EndZ=0
    g14: LineSegment StartX=0 StartY=10.8 StartZ=0 EndX=-2 EndY=10.8 EndZ=0
    g15: LineSegment StartX=-1.6 StartY=4.7 StartZ=0 EndX=-1.6 EndY=1.7 EndZ=0
    g16: LineSegment StartX=-1.6 StartY=4.7 StartZ=0 EndX=-2 EndY=4.7 EndZ=0
    g17: LineSegment StartX=-2 StartY=4.7 StartZ=0 EndX=-2 EndY=10.8 EndZ=0
  constraints (44):
    c: Vertical(g0)
    c: Vertical(g1)
    c: Distance(g1) = 0.9
    c: Block(g0)
    c: Distance(g0) = 1.7
    c: Weight(g2) = 1
    c: Equal(g2,g3)
    c: Equal(g2,g4)
    c: Coincident(g5,g1)
    c: InternalAlignment(g2,g5)
    c: InternalAlignment(g3,g5)
    c: InternalAlignment(g4,g5)
    c: InternalAlignment(g6,g5)
    c: InternalAlignment(g7,g5)
    c: Block(g5)
    c: Coincident(g8,g1)
    c: Vertical(g8)
    c: Distance(g8) = 7
    c: Vertical(g9)
    c: Equal(g8,g9) = 7
    c: Coincident(g9,g0)
    c: Coincident(g10,g8)
    c: Coincident(g10,g9)
    c: Horizontal(g10)
    c: Coincident(g11,g5)
    c: Horizontal(g11)
    c: Coincident(g12,g0)
    c: Vertical(g12)
    c: Distance(g12) = 2.8
    c: Coincident(g13,g12)
    c: Vertical(g13)
    c: Distance(g13) = 6.3
    c: Coincident(g14,g13)
    c: Horizontal(g14)
    c: Distance(g14) = 2
    c: Vertical(g15)
    c: Distance(g15) = 3
    c: Block(g11)
    c: Coincident(g15,g11)
    c: Coincident(g16,g15)
    c: Horizontal(g16)
    c: Coincident(g17,g16)
    c: Coincident(g17,g14)
    c: Vertical(g17)
FEATURE [Part::Revolution] Revolve040  label="backCaseScrewRetainer001"
  Angle = 360
  Axis = (0,1,0)
  Base = (0,0,0)
  FaceMakerClass = Part::FaceMakerBullseye
  Placement = pos=(12.5,3,10) rot=(0,0,1;0rad)
  Solid = false
  Source = -> Face036
  Symmetric = false
FEATURE [Part::Feature] Face055
  shape: bbox 3.5 x 30.2 x 2e-07 mm, 1 faces, 0 solids (baked)
FEATURE [Part::Revolution] Revolve059  label="backCaseScrewPost"
  Angle = 360
  Axis = (0,1,0)
  Base = (0,0,0)
  FaceMakerClass = Part::FaceMakerBullseye
  Placement = pos=(12.5,4.5,10) rot=(0,0,1;0rad)
  Solid = false
  Source = -> Face055
  Symmetric = false
FEATURE [Part::Feature] Face056
  shape: bbox 3.5 x 30.2 x 2e-07 mm, 1 faces, 0 solids (baked)
FEATURE [Part::Revolution] Revolve060  label="backCaseScrewPost001"
  Angle = 360
  Axis = (0,1,0)
  Base = (0,0,0)
  FaceMakerClass = Part::FaceMakerBullseye
  Placement = pos=(12.5,4.5,62) rot=(0,0,1;0rad)
  Solid = false
  Source = -> Face056
  Symmetric = false
FEATURE [Part::Feature] Face057
  shape: bbox 3.5 x 17.8 x 2e-07 mm, 1 faces, 0 solids (baked)
FEATURE [Part::Revolution] Revolve061  label="removeToCreateScrewAndThreadedInsertHole"
  Angle = 360
  Axis = (0,1,0)
  Base = (0,0,0)
  FaceMakerClass = Part::FaceMakerBullseye
  Placement = pos=(12.5,0,10) rot=(0,0,1;0rad)
  Solid = false
  Source = -> Face057
  Symmetric = false
FEATURE [Part::Feature] Face058
  shape: bbox 3.5 x 17.8 x 2e-07 mm, 1 faces, 0 solids (baked)
FEATURE [Part::Revolution] Revolve062  label="removeToCreateScrewAndThreadedInsertHole001"
  Angle = 360
  Axis = (0,1,0)
  Base = (0,0,0)
  FaceMakerClass = Part::FaceMakerBullseye
  Placement = pos=(12.5,0,62) rot=(0,0,1;0rad)
  Solid = false
  Source = -> Face058
  Symmetric = false
FEATURE [Part::Feature] Face059
  shape: bbox 3.5 x 17.8 x 2e-07 mm, 1 faces, 0 solids (baked)
FEATURE [Part::Revolution] Revolve063  label="removeToCreateScrewAndThreadedInsertHole002"
  Angle = 360
  Axis = (0,1,0)
  Base = (0,0,0)
  FaceMakerClass = Part::FaceMakerBullseye
  Placement = pos=(89.5,0,68.5) rot=(0,0,1;0rad)
  Solid = false
  Source = -> Face059
  Symmetric = false
FEATURE [Part::Feature] Face060
  shape: bbox 3.5 x 17.8 x 2e-07 mm, 1 faces, 0 solids (baked)
FEATURE [Part::Revolution] Revolve064  label="removeToCreateScrewAndThreadedInsertHole003"
  Angle = 360
  Axis = (0,1,0)
  Base = (0,0,0)
  FaceMakerClass = Part::FaceMakerBullseye
  Placement = pos=(89.5,0,3.5) rot=(0,0,1;0rad)
  Solid = false
  Source = -> Face060
  Symmetric = false
FEATURE [Part::Feature] Face061
  shape: bbox 3.5 x 17.8 x 2e-07 mm, 1 faces, 0 solids (baked)
FEATURE [Part::Revolution] Revolve065  label="removeToCreateScrewAndThreadedInsertHole004"
  Angle = 360
  Axis = (0,1,0)
  Base = (0,0,0)
  FaceMakerClass = Part::FaceMakerBullseye
  Placement = pos=(102.5,4.7,3.5) rot=(0,0,1;0rad)
  Solid = false
  Source = -> Face061
  Symmetric = false
FEATURE [Part::Feature] Face062
  shape: bbox 3.5 x 17.8 x 2e-07 mm, 1 faces, 0 solids (baked)
FEATURE [Part::Revolution] Revolve066  label="removeToCreateScrewAndThreadedInsertHole005"
  Angle = 360
  Axis = (0,1,0)
  Base = (0,0,0)
  FaceMakerClass = Part::FaceMakerBullseye
  Placement = pos=(102.5,4.7,68.5) rot=(0,0,1;0rad)
  Solid = false
  Source = -> Face062
  Symmetric = false
FEATURE [Part::MultiFuse] Fusion047  label="makeHoles"
  Shapes = -> [Revolve066,Revolve065,Revolve064,Revolve063,Revolve062,Revolve061]
FEATURE [Part::Feature] Face063
  shape: bbox 3.6 x 3.2 x 2e-07 mm, 1 faces, 0 solids (baked)
FEATURE [Part::Revolution] Revolve067  label="moreFrontCaseScrewRetainer002"
  Angle = 360
  Axis = (0,1,0)
  Base = (0,0,0)
  FaceMakerClass = Part::FaceMakerBullseye
  Placement = pos=(102.5,4.5,68.5) rot=(0,0,1;0rad)
  Solid = false
  Source = -> Face063
  Symmetric = false
FEATURE [Part::Feature] Face064
  shape: bbox 3.6 x 3.2 x 2e-07 mm, 1 faces, 0 solids (baked)
FEATURE [Part::Revolution] Revolve068  label="moreFrontCaseScrewRetainer003"
  Angle = 360
  Axis = (0,1,0)
  Base = (0,0,0)
  FaceMakerClass = Part::FaceMakerBullseye
  Placement = pos=(102.5,4.5,3.5) rot=(0,0,1;0rad)
  Solid = false
  Source = -> Face064
  Symmetric = false
FEATURE [Part::Feature] Face065
  shape: bbox 3.5 x 17.8 x 2e-07 mm, 1 faces, 0 solids (baked)
FEATURE [Part::Revolution] Revolve069  label="removeToCreateScrewAndThreadedInsertHole006"
  Angle = 360
  Axis = (0,1,0)
  Base = (0,0,0)
  FaceMakerClass = Part::FaceMakerBullseye
  Placement = pos=(12.5,0,10) rot=(0,0,1;0rad)
  Solid = false
  Source = -> Face065
  Symmetric = false
FEATURE [Part::Feature] Face066
  shape: bbox 3.5 x 17.8 x 2e-07 mm, 1 faces, 0 solids (baked)
FEATURE [Part::Revolution] Revolve070  label="removeToCreateScrewAndThreadedInsertHole007"
  Angle = 360
  Axis = (0,1,0)
  Base = (0,0,0)
  FaceMakerClass = Part::FaceMakerBullseye
  Placement = pos=(12.5,0,62) rot=(0,0,1;0rad)
  Solid = false
  Source = -> Face066
  Symmetric = false
FEATURE [Part::Feature] Face067
  shape: bbox 3.5 x 17.8 x 2e-07 mm, 1 faces, 0 solids (baked)
FEATURE [Part::Revolution] Revolve071  label="removeToCreateScrewAndThreadedInsertHole008"
  Angle = 360
  Axis = (0,1,0)
  Base = (0,0,0)
  FaceMakerClass = Part::FaceMakerBullseye
  Placement = pos=(89.5,0,68.5) rot=(0,0,1;0rad)
  Solid = false
  Source = -> Face067
  Symmetric = false
FEATURE [Part::Feature] Face068
  shape: bbox 3.5 x 17.8 x 2e-07 mm, 1 faces, 0 solids (baked)
FEATURE [Part::Revolution] Revolve072  label="removeToCreateScrewAndThreadedInsertHole009"
  Angle = 360
  Axis = (0,1,0)
  Base = (0,0,0)
  FaceMakerClass = Part::FaceMakerBullseye
  Placement = pos=(89.5,0,3.5) rot=(0,0,1;0rad)
  Solid = false
  Source = -> Face068
  Symmetric = false
FEATURE [Part::Feature] Face069
  shape: bbox 3.5 x 17.8 x 2e-07 mm, 1 faces, 0 solids (baked)
FEATURE [Part::Feature] Face070
  shape: bbox 3.5 x 17.8 x 2e-07 mm, 1 faces, 0 solids (baked)
FEATURE [Part::Revolution] Revolve073  label="removeToCreateScrewAndThreadedInsertHole010"
  Angle = 360
  Axis = (0,1,0)
  Base = (0,0,0)
  FaceMakerClass = Part::FaceMakerBullseye
  Placement = pos=(102.5,4.7,3.5) rot=(0,0,1;0rad)
  Solid = false
  Source = -> Face069
  Symmetric = false
FEATURE [Part::Revolution] Revolve074  label="removeToCreateScrewAndThreadedInsertHole011"
  Angle = 360
  Axis = (0,1,0)
  Base = (0,0,0)
  FaceMakerClass = Part::FaceMakerBullseye
  Placement = pos=(102.5,4.7,68.5) rot=(0,0,1;0rad)
  Solid = false
  Source = -> Face070
  Symmetric = false
FEATURE [Part::MultiFuse] Fusion048  label="makeHoles001"
  Shapes = -> [Revolve074,Revolve073,Revolve072,Revolve071,Revolve070,Revolve069]
FEATURE [Part::MultiFuse] Fusion049  label="caseScrewRetainers"
  Shapes = -> [Revolve067,Revolve068,Revolve048,Revolve047,Revolve039,Revolve040]
FEATURE [Part::Cut] Cut015  label="caseScrewRetainers001"
  Base = -> Fusion049
  Tool = -> Fusion048
FEATURE [Part::MultiFuse] Fusion050  label="casePillars"
  Shapes = -> [Revolve055,Revolve054,Revolve043,Revolve046,Revolve059,Revolve060]
FEATURE [Part::Feature] Face071 .. Face076  x6 (patterned run collapsed; names and placements below)
  shape: bbox 3.5 x 17.8 x 2e-07 mm, 1 faces, 0 solids (baked)
FEATURE [Part::Revolution] Revolve075  label="removeToCreateScrewAndThreadedInsertHole012"
  Angle = 360
  Axis = (0,1,0)
  Base = (0,0,0)
  FaceMakerClass = Part::FaceMakerBullseye
  Placement = pos=(12.5,0,10) rot=(0,0,1;0rad)
  Solid = false
  Source = -> Face071
  Symmetric = false
FEATURE [Part::Revolution] Revolve076  label="removeToCreateScrewAndThreadedInsertHole013"
  Angle = 360
  Axis = (0,1,0)
  Base = (0,0,0)
  FaceMakerClass = Part::FaceMakerBullseye
  Placement = pos=(12.5,0,62) rot=(0,0,1;0rad)
  Solid = false
  Source = -> Face072
  Symmetric = false
FEATURE [Part::Revolution] Revolve077  label="removeToCreateScrewAndThreadedInsertHole014"
  Angle = 360
  Axis = (0,1,0)
  Base = (0,0,0)
  FaceMakerClass = Part::FaceMakerBullseye
  Placement = pos=(89.5,0,68.5) rot=(0,0,1;0rad)
  Solid = false
  Source = -> Face073
  Symmetric = false
FEATURE [Part::Revolution] Revolve078  label="removeToCreateScrewAndThreadedInsertHole015"
  Angle = 360
  Axis = (0,1,0)
  Base = (0,0,0)
  FaceMakerClass = Part::FaceMakerBullseye
  Placement = pos=(89.5,0,3.5) rot=(0,0,1;0rad)
  Solid = false
  Source = -> Face074
  Symmetric = false
FEATURE [Part::Revolution] Revolve079  label="removeToCreateScrewAndThreadedInsertHole016"
  Angle = 360
  Axis = (0,1,0)
  Base = (0,0,0)
  FaceMakerClass = Part::FaceMakerBullseye
  Placement = pos=(102.5,4.7,3.5) rot=(0,0,1;0rad)
  Solid = false
  Source = -> Face075
  Symmetric = false
FEATURE [Part::Revolution] Revolve080  label="removeToCreateScrewAndThreadedInsertHole017"
  Angle = 360
  Axis = (0,1,0)
  Base = (0,0,0)
  FaceMakerClass = Part::FaceMakerBullseye
  Placement = pos=(102.5,4.7,68.5) rot=(0,0,1;0rad)
  Solid = false
  Source = -> Face076
  Symmetric = false
FEATURE [Part::MultiFuse] Fusion051  label="makeHoles002"
  Shapes = -> [Revolve080,Revolve079,Revolve078,Revolve077,Revolve076,Revolve075]
FEATURE [Part::Cut] Cut016  label="caesPillars"
  Base = -> Fusion050
  Tool = -> Fusion051
FEATURE [Part::Revolution] Revolve009  label="plugHousing016"
  Angle = 360
  Axis = (0,1,0)
  Base = (0,0,0)
  FaceMakerClass = Part::FaceMakerBullseye
  Placement = pos=(0,0,36.15) rot=(0,0,1;0rad)
  Solid = false
  Source = -> Face012
  Symmetric = false
FEATURE [Part::MultiFuse] Fusion014  label="plugHousing023"
  Placement = pos=(0,0,0) rot=(0,0,1;1.5708rad)
  Shapes = -> [Revolve011,Revolve009]
FEATURE [Part::Revolution] Revolve010  label="plugHousing017"
  Angle = 360
  Axis = (0,1,0)
  Base = (0,0,0)
  FaceMakerClass = Part::FaceMakerBullseye
  Placement = pos=(0,0,36.15) rot=(0,0,1;0rad)
  Solid = false
  Source = -> Face014
  Symmetric = false
FEATURE [Part::MultiFuse] Fusion015  label="plugHousing024"
  Placement = pos=(0,0,0) rot=(0,0,1;1.5708rad)
  Shapes = -> [Revolve010,Revolve015]
FEATURE [Part::Revolution] Revolve014  label="plugHousing026"
  Angle = 360
  Axis = (0,1,0)
  Base = (0,0,0)
  FaceMakerClass = Part::FaceMakerBullseye
  Placement = pos=(0,0,36.15) rot=(0,0,1;0rad)
  Solid = false
  Source = -> Face011
  Symmetric = false
FEATURE [Part::Revolution] Revolve013  label="plugHousing025"
  Angle = 360
  Axis = (0,1,0)
  Base = (0,0,0)
  FaceMakerClass = Part::FaceMakerBullseye
  Placement = pos=(0,0,36.15) rot=(0,0,1;0rad)
  Solid = false
  Source = -> Face015
  Symmetric = false
FEATURE [Part::MultiFuse] Fusion016  label="plugHousing028"
  Placement = pos=(0,19,0) rot=(0,0,1;3.14159rad)
  Shapes = -> [Fusion014,Fusion013]
FEATURE [Part::MultiFuse] Fusion011  label="plugHousing018"
  Placement = pos=(0,0,0) rot=(0,0,1;1.5708rad)
  Shapes = -> [Revolve014,Revolve013]
FEATURE [Part::MultiFuse] Fusion012  label="plugHousing019"
  Placement = pos=(0,19,0) rot=(0,0,1;3.14159rad)
  Shapes = -> [Fusion011,Fusion015]
FEATURE [Part::MultiFuse] Fusion017  label="plugHousing029"
  Placement = pos=(122.621,0,-0.15) rot=(0,0,1;0rad)
  Shapes = -> [Fusion016,Fusion012]
FEATURE [Part::MultiFuse] Fusion052  label="casePillarRetainers"
  Shapes = -> [Extrude012,Extrude013,Extrude014,Extrude015,Extrude016,Extrude017,Extrude018,Extrude019,Box011,Box012]
FEATURE [Part::Feature] Face077
  shape: bbox 3.5 x 17.8 x 2e-07 mm, 1 faces, 0 solids (baked)
FEATURE [Part::Revolution] Revolve081  label="removeToCreateScrewAndThreadedInsertHole018"
  Angle = 360
  Axis = (0,1,0)
  Base = (0,0,0)
  FaceMakerClass = Part::FaceMakerBullseye
  Placement = pos=(62.3,30.3,19.7) rot=(0,0,1;0rad)
  Solid = false
  Source = -> Face077
  Symmetric = false
FEATURE [Part::Feature] Face078
  shape: bbox 3.5 x 17.8 x 2e-07 mm, 1 faces, 0 solids (baked)
FEATURE [Part::Revolution] Revolve082  label="removeToCreateScrewAndThreadedInsertHole019"
  Angle = 360
  Axis = (0,1,0)
  Base = (0,0,0)
  FaceMakerClass = Part::FaceMakerBullseye
  Placement = pos=(62.3,30.3,51.7) rot=(0,0,1;0rad)
  Solid = false
  Source = -> Face078
  Symmetric = false
FEATURE [Part::Feature] Face079
  shape: bbox 3.5 x 17.8 x 2e-07 mm, 1 faces, 0 solids (baked)
FEATURE [Part::Revolution] Revolve083  label="removeToCreateScrewAndThreadedInsertHole020"
  Angle = 360
  Axis = (0,1,0)
  Base = (0,0,0)
  FaceMakerClass = Part::FaceMakerBullseye
  Placement = pos=(30.3,30.3,19.7) rot=(0,0,1;0rad)
  Solid = false
  Source = -> Face079
  Symmetric = false
FEATURE [Part::Feature] Face080
  shape: bbox 3.5 x 17.8 x 2e-07 mm, 1 faces, 0 solids (baked)
FEATURE [Part::Revolution] Revolve084  label="removeToCreateScrewAndThreadedInsertHole021"
  Angle = 360
  Axis = (0,1,0)
  Base = (0,0,0)
  FaceMakerClass = Part::FaceMakerBullseye
  Placement = pos=(30.3,30.3,51.7) rot=(0,0,1;0rad)
  Solid = false
  Source = -> Face080
  Symmetric = false
FEATURE [Part::MultiFuse] Fusion053  label="createThreadedInsertHolesForFan"
  Shapes = -> [Revolve081,Revolve082,Revolve083,Revolve084]
FEATURE [Part::Cut] Cut017  label="fanScrewHousing001"
  Base = -> Fusion046
  Tool = -> Fusion053
FEATURE [Part::Feature] Face081
  shape: bbox 3.5 x 17.8 x 2e-07 mm, 1 faces, 0 solids (baked)
FEATURE [Part::Revolution] Revolve085  label="removeToCreateScrewAndThreadedInsertHole022"
  Angle = 360
  Axis = (0,1,0)
  Base = (0,0,0)
  FaceMakerClass = Part::FaceMakerBullseye
  Placement = pos=(62.3,30.3,19.7) rot=(0,0,1;0rad)
  Solid = false
  Source = -> Face081
  Symmetric = false
FEATURE [Part::Feature] Face082
  shape: bbox 3.5 x 17.8 x 2e-07 mm, 1 faces, 0 solids (baked)
FEATURE [Part::Revolution] Revolve086  label="removeToCreateScrewAndThreadedInsertHole023"
  Angle = 360
  Axis = (0,1,0)
  Base = (0,0,0)
  FaceMakerClass = Part::FaceMakerBullseye
  Placement = pos=(62.3,30.3,51.7) rot=(0,0,1;0rad)
  Solid = false
  Source = -> Face082
  Symmetric = false
FEATURE [Part::Feature] Face083
  shape: bbox 3.5 x 17.8 x 2e-07 mm, 1 faces, 0 solids (baked)
FEATURE [Part::Revolution] Revolve087  label="removeToCreateScrewAndThreadedInsertHole024"
  Angle = 360
  Axis = (0,1,0)
  Base = (0,0,0)
  FaceMakerClass = Part::FaceMakerBullseye
  Placement = pos=(30.3,30.3,19.7) rot=(0,0,1;0rad)
  Solid = false
  Source = -> Face083
  Symmetric = false
FEATURE [Part::Feature] Face084
  shape: bbox 3.5 x 17.8 x 2e-07 mm, 1 faces, 0 solids (baked)
FEATURE [Part::Revolution] Revolve088  label="removeToCreateScrewAndThreadedInsertHole025"
  Angle = 360
  Axis = (0,1,0)
  Base = (0,0,0)
  FaceMakerClass = Part::FaceMakerBullseye
  Placement = pos=(30.3,30.3,51.7) rot=(0,0,1;0rad)
  Solid = false
  Source = -> Face084
  Symmetric = false
FEATURE [Part::MultiFuse] Fusion054  label="createThreadedInsertHolesForFan001"
  Shapes = -> [Revolve085,Revolve086,Revolve087,Revolve088]
FEATURE [Part::Cut] Cut018  label="top007"
  Base = -> Fusion040
  Tool = -> Fusion054
FEATURE [Sketcher::SketchObject] Sketch029
  FullyConstrained = false
  Placement = pos=(0,0,0) rot=(1,0,0;1.5708rad)
  sketch-geometry (24):
    g0: ArcOfCircle CenterX=-4 CenterY=-10.5 CenterZ=0 NormalX=0 NormalY=0 NormalZ=1 AngleXU=0 Radius=1.5 StartAngle=6e-16 EndAngle=3.14159
    g1: ArcOfCircle CenterX=-34.2 CenterY=-10.5 CenterZ=0 NormalX=0 NormalY=0 NormalZ=1 AngleXU=0 Radius=1.5 StartAngle=0 EndAngle=3.14159
    g2: ArcOfCircle CenterX=-34.2 CenterY=-27.7 CenterZ=0 NormalX=0 NormalY=0 NormalZ=1 AngleXU=0 Radius=1.5 StartAngle=3.14159 EndAngle=6.28319
    g3: ArcOfCircle CenterX=-4 CenterY=-27.7 CenterZ=0 NormalX=0 NormalY=0 NormalZ=1 AngleXU=0 Radius=1.5 StartAngle=3.1416 EndAngle=6.28319
    g4: ArcOfCircle CenterX=-10 CenterY=-4.3 CenterZ=0 NormalX=0 NormalY=0 NormalZ=1 AngleXU=0 Radius=1.5 StartAngle=2e-16 EndAngle=3.14159
    g5: ArcOfCircle CenterX=-16.1 CenterY=-1.8 CenterZ=0 NormalX=0 NormalY=0 NormalZ=1 AngleXU=0 Radius=1.5 StartAngle=5e-16 EndAngle=3.14159
    g6: ArcOfCircle CenterX=-22.1 CenterY=-1.8 CenterZ=0 NormalX=0 NormalY=0 NormalZ=1 AngleXU=0 Radius=1.5 StartAngle=5e-16 EndAngle=3.14159
    g7: ArcOfCircle CenterX=-28.2 CenterY=-4.3 CenterZ=0 NormalX=0 NormalY=0 NormalZ=1 AngleXU=0 Radius=1.5 StartAngle=2e-16 EndAngle=3.14159
    g8: ArcOfCircle CenterX=-10 CenterY=-33.9 CenterZ=0 NormalX=0 NormalY=0 NormalZ=1 AngleXU=0 Radius=1.5 StartAngle=3.14159 EndAngle=6.28319
    g9: ArcOfCircle CenterX=-16.1 CenterY=-36.4 CenterZ=0 NormalX=0 NormalY=0 NormalZ=1 AngleXU=0 Radius=1.5 StartAngle=3.14159 EndAngle=6.28319
    g10: ArcOfCircle CenterX=-22.1 CenterY=-36.4 CenterZ=0 NormalX=0 NormalY=0 NormalZ=1 AngleXU=0 Radius=1.5 StartAngle=3.14159 EndAngle=6.28319
    g11: ArcOfCircle CenterX=-28.2 CenterY=-33.9 CenterZ=0 NormalX=0 NormalY=0 NormalZ=1 AngleXU=0 Radius=1.5 StartAngle=3.14159 EndAngle=6.28319
    g12: LineSegment StartX=-35.7 StartY=-10.5 StartZ=0 EndX=-35.7 EndY=-27.7 EndZ=0
    g13: LineSegment StartX=-32.7 StartY=-10.5 StartZ=0 EndX=-32.7 EndY=-27.7 EndZ=0
    g14: LineSegment StartX=-29.7 StartY=-33.9 StartZ=0 EndX=-29.7 EndY=-4.3 EndZ=0
    g15: LineSegment StartX=-26.7 StartY=-33.9 StartZ=0 EndX=-26.7 EndY=-4.3 EndZ=0
    g16: LineSegment StartX=-2.5 StartY=-10.5 StartZ=0 EndX=-2.5 EndY=-27.7 EndZ=0
    g17: LineSegment StartX=-8.5 StartY=-4.3 StartZ=0 EndX=-8.5 EndY=-33.9 EndZ=0
    g18: LineSegment StartX=-5.5 StartY=-10.5 StartZ=0 EndX=-5.5 EndY=-27.7 EndZ=0
    g19: LineSegment StartX=-11.5 StartY=-4.3 StartZ=0 EndX=-11.5 EndY=-33.9 EndZ=0
    g20: LineSegment StartX=-14.6 StartY=-1.8 StartZ=0 EndX=-14.6 EndY=-36.4 EndZ=0
    g21: LineSegment StartX=-17.6 StartY=-1.8 StartZ=0 EndX=-17.6 EndY=-36.4 EndZ=0
    g22: LineSegment StartX=-20.6 StartY=-36.4 StartZ=0 EndX=-20.6 EndY=-1.8 EndZ=0
    g23: LineSegment StartX=-23.6 StartY=-1.8 StartZ=0 EndX=-23.6 EndY=-36.4 EndZ=0
  constraints (48):
    c: Block(g0)
    c: Block(g1)
    c: Block(g2)
    c: Block(g3)
    c: Block(g4)
    c: Block(g5)
    c: Block(g6)
    c: Block(g7)
    c: Block(g8)
    c: Block(g9)
    c: Block(g10)
    c: Block(g11)
    c: Coincident(g12,g1)
    c: Coincident(g12,g2)
    c: Vertical(g12)
    c: Coincident(g13,g1)
    c: Coincident(g13,g2)
    c: Vertical(g13)
    c: Coincident(g14,g11)
    c: Coincident(g14,g7)
    c: Vertical(g14)
    c: Coincident(g15,g11)
    c: Coincident(g15,g7)
    c: Vertical(g15)
    c: Coincident(g16,g0)
    c: Coincident(g16,g3)
    c: Vertical(g16)
    c: Coincident(g17,g4)
    c: Coincident(g17,g8)
    c: Vertical(g17)
    c: Coincident(g18,g0)
    c: Coincident(g18,g3)
    c: Vertical(g18)
    c: Coincident(g19,g4)
    c: Coincident(g19,g8)
    c: Vertical(g19)
    c: Coincident(g20,g5)
    c: Coincident(g20,g9)
    c: Vertical(g20)
    c: Coincident(g21,g5)
    c: Coincident(g21,g9)
    c: Vertical(g21)
    c: Coincident(g22,g10)
    c: Coincident(g22,g6)
    c: Vertical(g22)
    c: Coincident(g23,g6)
    c: Coincident(g23,g10)
    c: Vertical(g23)
FEATURE [Part::Extrusion] Extrude020  label="removeToCreateFanGrillHoles"
  Base = -> Sketch029
  Dir = (0,-1,6e-16)
  DirMode = 2
  FaceMakerClass = Part::FaceMakerBullseye
  LengthFwd = 10
  LengthRev = 0
  Placement = pos=(65.4,44,54.82) rot=(0,0,1;0rad)
  Solid = true
  Symmetric = false
FEATURE [Part::MultiFuse] Fusion055  label="top008"
  Shapes = -> [Cut017,Cut018]
FEATURE [Part::Cut] Cut019  label="top009"
  Base = -> Fusion055
  Tool = -> Extrude020
FEATURE [App::MeasureDistance] Distance003  label="Distance: 71.95 mm"
  Distance = 71.9513
  P1 = (117,38,72)
  P2 = (117,38,0.0487319)
FEATURE [Sketcher::SketchObject] Sketch030
  FullyConstrained = true
  Placement = pos=(117,19,0) rot=(0.57735,0.57735,0.57735;2.0944rad)
  sketch-geometry (48):
    g0: LineSegment StartX=-49.19 StartY=69.25 StartZ=0 EndX=-49.19 EndY=66.25 EndZ=0
    g1: LineSegment StartX=-49.19 StartY=63.5 StartZ=0 EndX=-49.19 EndY=60.5 EndZ=0
    g2: LineSegment StartX=-49.19 StartY=57.75 StartZ=0 EndX=-49.19 EndY=54.75 EndZ=0
    g3: LineSegment StartX=-49.19 StartY=52 StartZ=0 EndX=-49.19 EndY=49 EndZ=0
    g4: LineSegment StartX=-49.19 StartY=46.25 StartZ=0 EndX=-49.19 EndY=43.25 EndZ=0
    g5: LineSegment StartX=-49.19 StartY=40.5 StartZ=0 EndX=-49.19 EndY=37.5 EndZ=0
    g6: LineSegment StartX=-49.19 StartY=34.5 StartZ=0 EndX=-49.19 EndY=31.5 EndZ=0
    g7: LineSegment StartX=-49.19 StartY=28.75 StartZ=0 EndX=-49.19 EndY=25.75 EndZ=0
    g8: LineSegment StartX=-49.19 StartY=23 StartZ=0 EndX=-49.19 EndY=20 EndZ=0
    g9: LineSegment StartX=-49.19 StartY=17.25 StartZ=0 EndX=-49.19 EndY=14.25 EndZ=0
    g10: LineSegment StartX=-49.19 StartY=11.5 StartZ=0 EndX=-49.19 EndY=8.5 EndZ=0
    g11: LineSegment StartX=-49.19 StartY=5.75 StartZ=0 EndX=-49.19 EndY=2.75 EndZ=0
    g12: ArcOfCircle CenterX=-1.5 CenterY=67.75 CenterZ=0 NormalX=0 NormalY=0 NormalZ=1 AngleXU=0 Radius=1.5 StartAngle=4.71239 EndAngle=7.85398
    g13: ArcOfCircle CenterX=-1.5 CenterY=62 CenterZ=0 NormalX=0 NormalY=0 NormalZ=1 AngleXU=0 Radius=1.5 StartAngle=4.71239 EndAngle=7.85398
    g14: ArcOfCircle CenterX=-1.5 CenterY=56.25 CenterZ=0 NormalX=0 NormalY=0 NormalZ=1 AngleXU=0 Radius=1.5 StartAngle=4.71239 EndAngle=7.85398
    g15: ArcOfCircle CenterX=-11.49 CenterY=50.5 CenterZ=0 NormalX=0 NormalY=0 NormalZ=1 AngleXU=0 Radius=1.5 StartAngle=4.71239 EndAngle=7.85398
    g16: ArcOfCircle CenterX=-16.28 CenterY=44.75 CenterZ=0 NormalX=0 NormalY=0 NormalZ=1 AngleXU=0 Radius=1.5 StartAngle=4.71239 EndAngle=7.85398
    g17: ArcOfCircle CenterX=-18.2337 CenterY=39 CenterZ=0 NormalX=0 NormalY=0 NormalZ=1 AngleXU=0 Radius=1.5 StartAngle=4.71485 EndAngle=7.85398
    g18: ArcOfCircle CenterX=-16.2837 CenterY=27.25 CenterZ=0 NormalX=0 NormalY=0 NormalZ=1 AngleXU=0 Radius=1.5 StartAngle=4.71485 EndAngle=7.85398
    g19: ArcOfCircle CenterX=-18.2337 CenterY=33 CenterZ=0 NormalX=0 NormalY=0 NormalZ=1 AngleXU=0 Radius=1.5 StartAngle=4.71485 EndAngle=7.85398
    g20: ArcOfCircle CenterX=-11.49 CenterY=21.5 CenterZ=0 NormalX=0 NormalY=0 NormalZ=1 AngleXU=0 Radius=1.5 StartAngle=4.71239 EndAngle=7.85398
    g21: ArcOfCircle CenterX=-1.5 CenterY=4.25 CenterZ=0 NormalX=0 NormalY=0 NormalZ=1 AngleXU=0 Radius=1.5 StartAngle=4.71239 EndAngle=7.85398
    g22: ArcOfCircle CenterX=-1.5 CenterY=10 CenterZ=0 NormalX=0 NormalY=0 NormalZ=1 AngleXU=0 Radius=1.5 StartAngle=4.71239 EndAngle=7.85398
    g23: ArcOfCircle CenterX=-1.5 CenterY=15.75 CenterZ=0 NormalX=0 NormalY=0 NormalZ=1 AngleXU=0 Radius=1.5 StartAngle=4.71239 EndAngle=7.85398
    g24: LineSegment StartX=-49.19 StartY=69.25 StartZ=0 EndX=-1.5 EndY=69.25 EndZ=0
    g25: LineSegment StartX=-49.19 StartY=66.25 StartZ=0 EndX=-1.5 EndY=66.25 EndZ=0
    g26: LineSegment StartX=-49.19 StartY=63.5 StartZ=0 EndX=-1.5 EndY=63.5 EndZ=0
    g27: LineSegment StartX=-49.19 StartY=60.5 StartZ=0 EndX=-1.5 EndY=60.5 EndZ=0
    g28: LineSegment StartX=-49.19 StartY=57.75 StartZ=0 EndX=-1.5 EndY=57.75 EndZ=0
    g29: LineSegment StartX=-49.19 StartY=54.75 StartZ=0 EndX=-1.5 EndY=54.75 EndZ=0
    g30: LineSegment StartX=-49.19 StartY=52 StartZ=0 EndX=-11.49 EndY=52 EndZ=0
    g31: LineSegment StartX=-49.19 StartY=49 StartZ=0 EndX=-11.49 EndY=49 EndZ=0
    g32: LineSegment StartX=-49.19 StartY=46.25 StartZ=0 EndX=-16.28 EndY=46.25 EndZ=0
    g33: LineSegment StartX=-49.19 StartY=43.25 StartZ=0 EndX=-16.28 EndY=43.25 EndZ=0
    g34: LineSegment StartX=-49.19 StartY=40.5 StartZ=0 EndX=-18.2337 EndY=40.5 EndZ=0
    g35: LineSegment StartX=-49.19 StartY=37.5 StartZ=0 EndX=-18.23 EndY=37.5 EndZ=0
    g36: LineSegment StartX=-49.19 StartY=34.5 StartZ=0 EndX=-18.2337 EndY=34.5 EndZ=0
    g37: LineSegment StartX=-49.19 StartY=31.5 StartZ=0 EndX=-18.23 EndY=31.5 EndZ=0
    g38: LineSegment StartX=-49.19 StartY=28.75 StartZ=0 EndX=-16.2837 EndY=28.75 EndZ=0
    g39: LineSegment StartX=-49.19 StartY=25.75 StartZ=0 EndX=-16.28 EndY=25.75 EndZ=0
    g40: LineSegment StartX=-49.19 StartY=23 StartZ=0 EndX=-11.49 EndY=23 EndZ=0
    g41: LineSegment StartX=-49.19 StartY=20 StartZ=0 EndX=-11.49 EndY=20 EndZ=0
    g42: LineSegment StartX=-49.19 StartY=17.25 StartZ=0 EndX=-1.5 EndY=17.25 EndZ=0
    g43: LineSegment StartX=-49.19 StartY=14.25 StartZ=0 EndX=-1.5 EndY=14.25 EndZ=0
    g44: LineSegment StartX=-49.19 StartY=11.5 StartZ=0 EndX=-1.5 EndY=11.5 EndZ=0
    g45: LineSegment StartX=-49.19 StartY=8.5 StartZ=0 EndX=-1.5 EndY=8.5 EndZ=0
    g46: LineSegment StartX=-49.19 StartY=5.75 StartZ=0 EndX=-1.5 EndY=5.75 EndZ=0
    g47: LineSegment StartX=-49.19 StartY=2.75 StartZ=0 EndX=-1.5 EndY=2.75 EndZ=0
  constraints (120):
    c: Vertical(g0)
    c: Distance(g0) = 3
    c: Block(g0)
    c: Vertical(g1)
    c: Distance(g1) = 3
    c: Vertical(g2)
    c: Equal(g0,g2) = 3
    c: Block(g2)
    c: Vertical(g3)
    c: Equal(g1,g3) = 3
    c: Vertical(g4)
    c: Equal(g0,g4) = 3
    c: Block(g4)
    c: Vertical(g5)
    c: Equal(g1,g5) = 3
    c: Vertical(g6)
    c: Equal(g0,g6) = 3
    c: Block(g6)
    c: Vertical(g7)
    c: Equal(g1,g7) = 3
    c: Vertical(g8)
    c: Equal(g0,g8) = 3
    c: Block(g8)
    c: Vertical(g9)
    c: Equal(g1,g9) = 3
    c: Vertical(g10)
    c: Equal(g0,g10) = 3
    c: Block(g10)
    c: Vertical(g11)
    c: Equal(g1,g11) = 3
    c: Block(g12)
    c: Block(g13)
    c: Block(g14)
    c: Block(g15)
    c: Block(g16)
    c: Block(g17)
    c: Block(g18)
    c: Block(g19)
    c: Block(g20)
    c: Block(g21)
    c: Block(g22)
    c: Block(g23)
    c: Block(g11)
    c: Block(g9)
    c: Block(g7)
    c: Block(g5)
    c: Block(g3)
    c: Block(g1)
    c: Coincident(g24,g0)
    c: Coincident(g24,g12)
    c: Horizontal(g24)
    c: Coincident(g25,g0)
    c: Coincident(g25,g12)
    c: Horizontal(g25)
    c: Coincident(g26,g1)
    c: Coincident(g26,g13)
    c: Horizontal(g26)
    c: Coincident(g27,g1)
    c: Coincident(g27,g13)
    c: Horizontal(g27)
    c: Coincident(g28,g2)
    c: Coincident(g28,g14)
    c: Horizontal(g28)
    c: Coincident(g29,g2)
    c: Coincident(g29,g14)
    c: Horizontal(g29)
    c: Coincident(g30,g3)
    c: Coincident(g30,g15)
    c: Horizontal(g30)
    c: Coincident(g31,g3)
    c: Coincident(g31,g15)
    c: Horizontal(g31)
    c: Coincident(g32,g4)
    c: Coincident(g32,g16)
    c: Horizontal(g32)
    c: Coincident(g33,g4)
    c: Coincident(g33,g16)
    c: Horizontal(g33)
    c: Coincident(g34,g5)
    c: Coincident(g34,g17)
    c: Horizontal(g34)
    c: Coincident(g35,g5)
    c: Coincident(g35,g17)
    c: Horizontal(g35)
    c: Coincident(g36,g6)
    c: Coincident(g36,g19)
    c: Horizontal(g36)
    c: Coincident(g37,g6)
    c: Coincident(g37,g19)
    c: Horizontal(g37)
    c: Coincident(g38,g7)
    c: Coincident(g38,g18)
    c: Horizontal(g38)
    c: Coincident(g39,g7)
    c: Coincident(g39,g18)
    c: Horizontal(g39)
    c: Coincident(g40,g8)
    c: Coincident(g40,g20)
    c: Horizontal(g40)
    c: Coincident(g41,g8)
    c: Coincident(g41,g20)
    c: Horizontal(g41)
    c: Coincident(g42,g9)
    c: Coincident(g42,g23)
    c: Horizontal(g42)
    c: Coincident(g43,g9)
    c: Coincident(g43,g23)
    c: Horizontal(g43)
    c: Coincident(g44,g10)
    c: Coincident(g44,g22)
    c: Horizontal(g44)
    c: Coincident(g45,g10)
    c: Coincident(g45,g22)
    c: Horizontal(g45)
    c: Coincident(g46,g11)
    c: Coincident(g46,g21)
    c: Horizontal(g46)
    c: Coincident(g47,g11)
    c: Coincident(g47,g21)
    c: Horizontal(g47)
FEATURE [Sketcher::SketchObject] Sketch031
  FullyConstrained = true
  Placement = pos=(117,19,0) rot=(0.57735,0.57735,0.57735;2.0944rad)
  sketch-geometry (24):
    g0: ArcOfCircle CenterX=-49.19 CenterY=67.75 CenterZ=0 NormalX=0 NormalY=0 NormalZ=1 AngleXU=0 Radius=1.5 StartAngle=1.5708 EndAngle=4.71239
    g1: ArcOfCircle CenterX=-49.19 CenterY=62 CenterZ=0 NormalX=0 NormalY=0 NormalZ=1 AngleXU=0 Radius=1.5 StartAngle=1.5708 EndAngle=4.71239
    g2: ArcOfCircle CenterX=-49.19 CenterY=56.25 CenterZ=0 NormalX=0 NormalY=0 NormalZ=1 AngleXU=0 Radius=1.5 StartAngle=1.5708 EndAngle=4.71239
    g3: ArcOfCircle CenterX=-49.19 CenterY=50.5 CenterZ=0 NormalX=0 NormalY=0 NormalZ=1 AngleXU=0 Radius=1.5 StartAngle=1.5708 EndAngle=4.71239
    g4: ArcOfCircle CenterX=-49.19 CenterY=44.75 CenterZ=0 NormalX=0 NormalY=0 NormalZ=1 AngleXU=0 Radius=1.5 StartAngle=1.5708 EndAngle=4.71239
    g5: ArcOfCircle CenterX=-49.19 CenterY=39 CenterZ=0 NormalX=0 NormalY=0 NormalZ=1 AngleXU=0 Radius=1.5 StartAngle=1.5708 EndAngle=4.71239
    g6: ArcOfCircle CenterX=-49.19 CenterY=33 CenterZ=0 NormalX=0 NormalY=0 NormalZ=1 AngleXU=0 Radius=1.5 StartAngle=1.5708 EndAngle=4.71239
    g7: ArcOfCircle CenterX=-49.19 CenterY=27.25 CenterZ=0 NormalX=0 NormalY=0 NormalZ=1 AngleXU=0 Radius=1.5 StartAngle=1.5708 EndAngle=4.71239
    g8: ArcOfCircle CenterX=-49.19 CenterY=21.5 CenterZ=0 NormalX=0 NormalY=0 NormalZ=1 AngleXU=0 Radius=1.5 StartAngle=1.5708 EndAngle=4.71239
    g9: ArcOfCircle CenterX=-49.19 CenterY=15.75 CenterZ=0 NormalX=0 NormalY=0 NormalZ=1 AngleXU=0 Radius=1.5 StartAngle=1.5708 EndAngle=4.71239
    g10: ArcOfCircle CenterX=-49.19 CenterY=10 CenterZ=0 NormalX=0 NormalY=0 NormalZ=1 AngleXU=0 Radius=1.5 StartAngle=1.5708 EndAngle=4.71239
    g11: ArcOfCircle CenterX=-49.19 CenterY=4.25 CenterZ=0 NormalX=0 NormalY=0 NormalZ=1 AngleXU=0 Radius=1.5 StartAngle=1.5708 EndAngle=4.71239
    g12: LineSegment StartX=-49.19 StartY=69.25 StartZ=0 EndX=-49.19 EndY=66.25 EndZ=0
    g13: LineSegment StartX=-49.19 StartY=63.5 StartZ=0 EndX=-49.19 EndY=60.5 EndZ=0
    g14: LineSegment StartX=-49.19 StartY=57.75 StartZ=0 EndX=-49.19 EndY=54.75 EndZ=0
    g15: LineSegment StartX=-49.19 StartY=52 StartZ=0 EndX=-49.19 EndY=49 EndZ=0
    g16: LineSegment StartX=-49.19 StartY=46.25 StartZ=0 EndX=-49.19 EndY=43.25 EndZ=0
    g17: LineSegment StartX=-49.19 StartY=40.5 StartZ=0 EndX=-49.19 EndY=37.5 EndZ=0
    g18: LineSegment StartX=-49.19 StartY=34.5 StartZ=0 EndX=-49.19 EndY=31.5 EndZ=0
    g19: LineSegment StartX=-49.19 StartY=28.75 StartZ=0 EndX=-49.19 EndY=25.75 EndZ=0
    g20: LineSegment StartX=-49.19 StartY=23 StartZ=0 EndX=-49.19 EndY=20 EndZ=0
    g21: LineSegment StartX=-49.19 StartY=17.25 StartZ=0 EndX=-49.19 EndY=14.25 EndZ=0
    g22: LineSegment StartX=-49.19 StartY=11.5 StartZ=0 EndX=-49.19 EndY=8.5 EndZ=0
    g23: LineSegment StartX=-49.19 StartY=5.75 StartZ=0 EndX=-49.19 EndY=2.75 EndZ=0
  constraints (48):
    c: Block(g0)
    c: Block(g1)
    c: Block(g2)
    c: Block(g3)
    c: Block(g4)
    c: Block(g5)
    c: Block(g6)
    c: Block(g7)
    c: Block(g8)
    c: Block(g9)
    c: Block(g10)
    c: Block(g11)
    c: Coincident(g12,g0)
    c: Coincident(g12,g0)
    c: Vertical(g12)
    c: Vertical(g13)
    c: Coincident(g13,g1)
    c: Vertical(g14)
    c: Coincident(g14,g2)
    c: Vertical(g15)
    c: Coincident(g15,g3)
    c: Vertical(g16)
    c: Coincident(g16,g4)
    c: Vertical(g17)
    c: Coincident(g17,g5)
    c: Vertical(g18)
    c: Coincident(g18,g6)
    c: Vertical(g19)
    c: Coincident(g19,g7)
    c: Vertical(g20)
    c: Coincident(g20,g8)
    c: Vertical(g21)
    c: Coincident(g21,g9)
    c: Vertical(g22)
    c: Coincident(g22,g10)
    c: Vertical(g23)
    c: Coincident(g23,g11)
    c: Block(g23)
    c: Block(g22)
    c: Block(g21)
    c: Block(g20)
    c: Block(g13)
    c: Block(g14)
    c: Block(g15)
    c: Block(g16)
    c: Block(g17)
    c: Block(g18)
    c: Block(g19)
FEATURE [Part::Extrusion] Extrude022
  Base = -> Sketch030
  Dir = (1,-2e-16,2e-16)
  DirMode = 2
  FaceMakerClass = Part::FaceMakerBullseye
  LengthFwd = 19
  LengthRev = 0
  Placement = pos=(-19,0,0) rot=(0,0,1;0rad)
  Solid = true
  Symmetric = false
FEATURE [Part::Fillet] Fillet022
  Base = -> Extrude022
  Edges = 24 edges r=1.49: [Edge6,Edge11,Edge18,Edge23,Edge30,Edge35,Edge42,Edge47,Edge54,Edge59,Edge66,Edge71,Edge78,Edge83,Edge90,Edge95,Edge102,Edge107,Edge114,Edge119,Edge126,Edge131,Edge138,Edge143]
FEATURE [Part::Cut] Cut020  label="top010"
  Base = -> Cut019
  Tool = -> Fillet022
FEATURE [Sketcher::SketchObject] Sketch032
  FullyConstrained = true
  Placement = pos=(117,19,0) rot=(0.57735,0.57735,0.57735;2.0944rad)
  sketch-geometry (48):
    g0: LineSegment StartX=-49.19 StartY=69.25 StartZ=0 EndX=-49.19 EndY=66.25 EndZ=0
    g1: LineSegment StartX=-49.19 StartY=63.5 StartZ=0 EndX=-49.19 EndY=60.5 EndZ=0
    g2: LineSegment StartX=-49.19 StartY=57.75 StartZ=0 EndX=-49.19 EndY=54.75 EndZ=0
    g3: LineSegment StartX=-49.19 StartY=52 StartZ=0 EndX=-49.19 EndY=49 EndZ=0
    g4: LineSegment StartX=-49.19 StartY=46.25 StartZ=0 EndX=-49.19 EndY=43.25 EndZ=0
    g5: LineSegment StartX=-49.19 StartY=40.5 StartZ=0 EndX=-49.19 EndY=37.5 EndZ=0
    g6: LineSegment StartX=-49.19 StartY=34.5 StartZ=0 EndX=-49.19 EndY=31.5 EndZ=0
    g7: LineSegment StartX=-49.19 StartY=28.75 StartZ=0 EndX=-49.19 EndY=25.75 EndZ=0
    g8: LineSegment StartX=-49.19 StartY=23 StartZ=0 EndX=-49.19 EndY=20 EndZ=0
    g9: LineSegment StartX=-49.19 StartY=17.25 StartZ=0 EndX=-49.19 EndY=14.25 EndZ=0
    g10: LineSegment StartX=-49.19 StartY=11.5 StartZ=0 EndX=-49.19 EndY=8.5 EndZ=0
    g11: LineSegment StartX=-49.19 StartY=5.75 StartZ=0 EndX=-49.19 EndY=2.75 EndZ=0
    g12: ArcOfCircle CenterX=-1.5 CenterY=67.75 CenterZ=0 NormalX=0 NormalY=0 NormalZ=1 AngleXU=0 Radius=1.5 StartAngle=4.71239 EndAngle=7.85398
    g13: ArcOfCircle CenterX=-1.5 CenterY=62 CenterZ=0 NormalX=0 NormalY=0 NormalZ=1 AngleXU=0 Radius=1.5 StartAngle=4.71239 EndAngle=7.85398
    g14: ArcOfCircle CenterX=-1.5 CenterY=56.25 CenterZ=0 NormalX=0 NormalY=0 NormalZ=1 AngleXU=0 Radius=1.5 StartAngle=4.71239 EndAngle=7.85398
    g15: ArcOfCircle CenterX=-11.49 CenterY=50.5 CenterZ=0 NormalX=0 NormalY=0 NormalZ=1 AngleXU=0 Radius=1.5 StartAngle=4.71239 EndAngle=7.85398
    g16: ArcOfCircle CenterX=-16.28 CenterY=44.75 CenterZ=0 NormalX=0 NormalY=0 NormalZ=1 AngleXU=0 Radius=1.5 StartAngle=4.71239 EndAngle=7.85398
    g17: ArcOfCircle CenterX=-18.2337 CenterY=39 CenterZ=0 NormalX=0 NormalY=0 NormalZ=1 AngleXU=0 Radius=1.5 StartAngle=4.71485 EndAngle=7.85398
    g18: ArcOfCircle CenterX=-16.2837 CenterY=27.25 CenterZ=0 NormalX=0 NormalY=0 NormalZ=1 AngleXU=0 Radius=1.5 StartAngle=4.71485 EndAngle=7.85398
    g19: ArcOfCircle CenterX=-18.2337 CenterY=33 CenterZ=0 NormalX=0 NormalY=0 NormalZ=1 AngleXU=0 Radius=1.5 StartAngle=4.71485 EndAngle=7.85398
    g20: ArcOfCircle CenterX=-11.49 CenterY=21.5 CenterZ=0 NormalX=0 NormalY=0 NormalZ=1 AngleXU=0 Radius=1.5 StartAngle=4.71239 EndAngle=7.85398
    g21: ArcOfCircle CenterX=-1.5 CenterY=4.25 CenterZ=0 NormalX=0 NormalY=0 NormalZ=1 AngleXU=0 Radius=1.5 StartAngle=4.71239 EndAngle=7.85398
    g22: ArcOfCircle CenterX=-1.5 CenterY=10 CenterZ=0 NormalX=0 NormalY=0 NormalZ=1 AngleXU=0 Radius=1.5 StartAngle=4.71239 EndAngle=7.85398
    g23: ArcOfCircle CenterX=-1.5 CenterY=15.75 CenterZ=0 NormalX=0 NormalY=0 NormalZ=1 AngleXU=0 Radius=1.5 StartAngle=4.71239 EndAngle=7.85398
    g24: LineSegment StartX=-49.19 StartY=69.25 StartZ=0 EndX=-1.5 EndY=69.25 EndZ=0
    g25: LineSegment StartX=-49.19 StartY=66.25 StartZ=0 EndX=-1.5 EndY=66.25 EndZ=0
    g26: LineSegment StartX=-49.19 StartY=63.5 StartZ=0 EndX=-1.5 EndY=63.5 EndZ=0
    g27: LineSegment StartX=-49.19 StartY=60.5 StartZ=0 EndX=-1.5 EndY=60.5 EndZ=0
    g28: LineSegment StartX=-49.19 StartY=57.75 StartZ=0 EndX=-1.5 EndY=57.75 EndZ=0
    g29: LineSegment StartX=-49.19 StartY=54.75 StartZ=0 EndX=-1.5 EndY=54.75 EndZ=0
    g30: LineSegment StartX=-49.19 StartY=52 StartZ=0 EndX=-11.49 EndY=52 EndZ=0
    g31: LineSegment StartX=-49.19 StartY=49 StartZ=0 EndX=-11.49 EndY=49 EndZ=0
    g32: LineSegment StartX=-49.19 StartY=46.25 StartZ=0 EndX=-16.28 EndY=46.25 EndZ=0
    g33: LineSegment StartX=-49.19 StartY=43.25 StartZ=0 EndX=-16.28 EndY=43.25 EndZ=0
    g34: LineSegment StartX=-49.19 StartY=40.5 StartZ=0 EndX=-18.2337 EndY=40.5 EndZ=0
    g35: LineSegment StartX=-49.19 StartY=37.5 StartZ=0 EndX=-18.23 EndY=37.5 EndZ=0
    g36: LineSegment StartX=-49.19 StartY=34.5 StartZ=0 EndX=-18.2337 EndY=34.5 EndZ=0
    g37: LineSegment StartX=-49.19 StartY=31.5 StartZ=0 EndX=-18.23 EndY=31.5 EndZ=0
    g38: LineSegment StartX=-49.19 StartY=28.75 StartZ=0 EndX=-16.2837 EndY=28.75 EndZ=0
    g39: LineSegment StartX=-49.19 StartY=25.75 StartZ=0 EndX=-16.28 EndY=25.75 EndZ=0
    g40: LineSegment StartX=-49.19 StartY=23 StartZ=0 EndX=-11.49 EndY=23 EndZ=0
    g41: LineSegment StartX=-49.19 StartY=20 StartZ=0 EndX=-11.49 EndY=20 EndZ=0
    g42: LineSegment StartX=-49.19 StartY=17.25 StartZ=0 EndX=-1.5 EndY=17.25 EndZ=0
    g43: LineSegment StartX=-49.19 StartY=14.25 StartZ=0 EndX=-1.5 EndY=14.25 EndZ=0
    g44: LineSegment StartX=-49.19 StartY=11.5 StartZ=0 EndX=-1.5 EndY=11.5 EndZ=0
    g45: LineSegment StartX=-49.19 StartY=8.5 StartZ=0 EndX=-1.5 EndY=8.5 EndZ=0
    g46: LineSegment StartX=-49.19 StartY=5.75 StartZ=0 EndX=-1.5 EndY=5.75 EndZ=0
    g47: LineSegment StartX=-49.19 StartY=2.75 StartZ=0 EndX=-1.5 EndY=2.75 EndZ=0
  constraints (120):
    c: Vertical(g0)
    c: Distance(g0) = 3
    c: Block(g0)
    c: Vertical(g1)
    c: Distance(g1) = 3
    c: Vertical(g2)
    c: Equal(g0,g2) = 3
    c: Block(g2)
    c: Vertical(g3)
    c: Equal(g1,g3) = 3
    c: Vertical(g4)
    c: Equal(g0,g4) = 3
    c: Block(g4)
    c: Vertical(g5)
    c: Equal(g1,g5) = 3
    c: Vertical(g6)
    c: Equal(g0,g6) = 3
    c: Block(g6)
    c: Vertical(g7)
    c: Equal(g1,g7) = 3
    c: Vertical(g8)
    c: Equal(g0,g8) = 3
    c: Block(g8)
    c: Vertical(g9)
    c: Equal(g1,g9) = 3
    c: Vertical(g10)
    c: Equal(g0,g10) = 3
    c: Block(g10)
    c: Vertical(g11)
    c: Equal(g1,g11) = 3
    c: Block(g12)
    c: Block(g13)
    c: Block(g14)
    c: Block(g15)
    c: Block(g16)
    c: Block(g17)
    c: Block(g18)
    c: Block(g19)
    c: Block(g20)
    c: Block(g21)
    c: Block(g22)
    c: Block(g23)
    c: Block(g11)
    c: Block(g9)
    c: Block(g7)
    c: Block(g5)
    c: Block(g3)
    c: Block(g1)
    c: Coincident(g24,g0)
    c: Coincident(g24,g12)
    c: Horizontal(g24)
    c: Coincident(g25,g0)
    c: Coincident(g25,g12)
    c: Horizontal(g25)
    c: Coincident(g26,g1)
    c: Coincident(g26,g13)
    c: Horizontal(g26)
    c: Coincident(g27,g1)
    c: Coincident(g27,g13)
    c: Horizontal(g27)
    c: Coincident(g28,g2)
    c: Coincident(g28,g14)
    c: Horizontal(g28)
    c: Coincident(g29,g2)
    c: Coincident(g29,g14)
    c: Horizontal(g29)
    c: Coincident(g30,g3)
    c: Coincident(g30,g15)
    c: Horizontal(g30)
    c: Coincident(g31,g3)
    c: Coincident(g31,g15)
    c: Horizontal(g31)
    c: Coincident(g32,g4)
    c: Coincident(g32,g16)
    c: Horizontal(g32)
    c: Coincident(g33,g4)
    c: Coincident(g33,g16)
    c: Horizontal(g33)
    c: Coincident(g34,g5)
    c: Coincident(g34,g17)
    c: Horizontal(g34)
    c: Coincident(g35,g5)
    c: Coincident(g35,g17)
    c: Horizontal(g35)
    c: Coincident(g36,g6)
    c: Coincident(g36,g19)
    c: Horizontal(g36)
    c: Coincident(g37,g6)
    c: Coincident(g37,g19)
    c: Horizontal(g37)
    c: Coincident(g38,g7)
    c: Coincident(g38,g18)
    c: Horizontal(g38)
    c: Coincident(g39,g7)
    c: Coincident(g39,g18)
    c: Horizontal(g39)
    c: Coincident(g40,g8)
    c: Coincident(g40,g20)
    c: Horizontal(g40)
    c: Coincident(g41,g8)
    c: Coincident(g41,g20)
    c: Horizontal(g41)
    c: Coincident(g42,g9)
    c: Coincident(g42,g23)
    c: Horizontal(g42)
    c: Coincident(g43,g9)
    c: Coincident(g43,g23)
    c: Horizontal(g43)
    c: Coincident(g44,g10)
    c: Coincident(g44,g22)
    c: Horizontal(g44)
    c: Coincident(g45,g10)
    c: Coincident(g45,g22)
    c: Horizontal(g45)
    c: Coincident(g46,g11)
    c: Coincident(g46,g21)
    c: Horizontal(g46)
    c: Coincident(g47,g11)
    c: Coincident(g47,g21)
    c: Horizontal(g47)
FEATURE [Part::Extrusion] Extrude023
  Base = -> Sketch032
  Dir = (1,-2e-16,2e-16)
  DirMode = 2
  FaceMakerClass = Part::FaceMakerBullseye
  LengthFwd = 19
  LengthRev = 0
  Placement = pos=(-19,0,0) rot=(0,0,1;0rad)
  Solid = true
  Symmetric = false
FEATURE [Part::Fillet] Fillet023
  Base = -> Extrude023
  Edges = <same value as first occurrence — deduplicated (x4 in doc)>
  Placement = pos=(0,0.05,0) rot=(0,0,1;0rad)
FEATURE [Part::Cut] Cut014  label="bottom003"
  Base = -> Cut007
  Tool = -> Fusion047
FEATURE [Part::Cut] Cut021  label="bottom004"
  Base = -> Cut014
  Tool = -> Fillet023
FEATURE [Sketcher::SketchObject] Sketch033
  FullyConstrained = true
  Placement = pos=(117,19,0) rot=(0.57735,0.57735,0.57735;2.0944rad)
  sketch-geometry (8):
    g0: LineSegment StartX=-49.19 StartY=69.25 StartZ=0 EndX=-49.19 EndY=66.25 EndZ=0
    g1: LineSegment StartX=-49.19 StartY=5.75 StartZ=0 EndX=-49.19 EndY=2.75 EndZ=0
    g2: ArcOfCircle CenterX=-1.5 CenterY=67.75 CenterZ=0 NormalX=0 NormalY=0 NormalZ=1 AngleXU=0 Radius=1.5 StartAngle=4.71239 EndAngle=7.85398
    g3: ArcOfCircle CenterX=-1.5 CenterY=4.25 CenterZ=0 NormalX=0 NormalY=0 NormalZ=1 AngleXU=0 Radius=1.5 StartAngle=4.71239 EndAngle=7.85398
    g4: LineSegment StartX=-49.19 StartY=69.25 StartZ=0 EndX=-1.5 EndY=69.25 EndZ=0
    g5: LineSegment StartX=-49.19 StartY=66.25 StartZ=0 EndX=-1.5 EndY=66.25 EndZ=0
    g6: LineSegment StartX=-49.19 StartY=5.75 StartZ=0 EndX=-1.5 EndY=5.75 EndZ=0
    g7: LineSegment StartX=-49.19 StartY=2.75 StartZ=0 EndX=-1.5 EndY=2.75 EndZ=0
  constraints (19):
    c: Vertical(g0)
    c: Distance(g0) = 3
    c: Block(g0)
    c: Vertical(g1)
    c: Block(g2)
    c: Block(g3)
    c: Block(g1)
    c: Coincident(g4,g0)
    c: Coincident(g4,g2)
    c: Horizontal(g4)
    c: Coincident(g5,g0)
    c: Coincident(g5,g2)
    c: Horizontal(g5)
    c: Coincident(g6,g1)
    c: Coincident(g6,g3)
    c: Horizontal(g6)
    c: Coincident(g7,g1)
    c: Coincident(g7,g3)
    c: Horizontal(g7)
FEATURE [Sketcher::SketchObject] Sketch034
  FullyConstrained = true
  Placement = pos=(117,19,0) rot=(0.57735,0.57735,0.57735;2.0944rad)
  sketch-geometry (8):
    g0: LineSegment StartX=-49.19 StartY=63.5 StartZ=0 EndX=-49.19 EndY=60.5 EndZ=0
    g1: LineSegment StartX=-49.19 StartY=11.5 StartZ=0 EndX=-49.19 EndY=8.5 EndZ=0
    g2: ArcOfCircle CenterX=-1.5 CenterY=62 CenterZ=0 NormalX=0 NormalY=0 NormalZ=1 AngleXU=0 Radius=1.5 StartAngle=4.71239 EndAngle=7.85398
    g3: ArcOfCircle CenterX=-1.5 CenterY=10 CenterZ=0 NormalX=0 NormalY=0 NormalZ=1 AngleXU=0 Radius=1.5 StartAngle=4.71239 EndAngle=7.85398
    g4: LineSegment StartX=-49.19 StartY=63.5 StartZ=0 EndX=-1.5 EndY=63.5 EndZ=0
    g5: LineSegment StartX=-49.19 StartY=60.5 StartZ=0 EndX=-1.5 EndY=60.5 EndZ=0
    g6: LineSegment StartX=-49.19 StartY=11.5 StartZ=0 EndX=-1.5 EndY=11.5 EndZ=0
    g7: LineSegment StartX=-49.19 StartY=8.5 StartZ=0 EndX=-1.5 EndY=8.5 EndZ=0
  constraints (19):
    c: Vertical(g0)
    c: Distance(g0) = 3
    c: Vertical(g1)
    c: Block(g1)
    c: Block(g2)
    c: Block(g3)
    c: Block(g0)
    c: Coincident(g4,g0)
    c: Coincident(g4,g2)
    c: Horizontal(g4)
    c: Coincident(g5,g0)
    c: Coincident(g5,g2)
    c: Horizontal(g5)
    c: Coincident(g6,g1)
    c: Coincident(g6,g3)
    c: Horizontal(g6)
    c: Coincident(g7,g1)
    c: Coincident(g7,g3)
    c: Horizontal(g7)
FEATURE [Part::Extrusion] Extrude024
  Base = -> Sketch033
  Dir = (1,0,0)
  DirMode = 2
  FaceMakerClass = Part::FaceMakerBullseye
  LengthFwd = 10
  LengthRev = 0
  Solid = true
  Symmetric = false
FEATURE [Part::Extrusion] Extrude025
  Base = -> Sketch034
  Dir = (1,0,0)
  DirMode = 2
  FaceMakerClass = Part::FaceMakerBullseye
  LengthFwd = 10
  LengthRev = 0
  Solid = true
  Symmetric = false
FEATURE [Part::Fillet] Fillet024  label="removeFromtMoreFrontCaseScrewRetainers"
  Base = -> Extrude024
  Edges = 4 edges r=1.49: [Edge6,Edge11,Edge18,Edge23]
  Placement = pos=(-11,0,0) rot=(0,0,1;0rad)
FEATURE [Part::Fillet] Fillet025  label="removeFromtMoreFrontCaseScrewRetainers001"
  Base = -> Extrude025
  Edges = 4 edges r=1.49: [Edge6,Edge11,Edge18,Edge23]
  Placement = pos=(-19,0,0) rot=(0,0,1;0rad)
FEATURE [Part::Cut] Cut022
  Base = -> Cut015
  Tool = -> Fillet025
FEATURE [Part::Cut] Cut023  label="screwRetainers"
  Base = -> Cut022
  Tool = -> Fillet024
FEATURE [Part::MultiFuse] Fusion056  label="bottom005"
  Shapes = -> [Fusion044,Cut021]
FEATURE [Part::MultiFuse] Fusion057  label="casePillars001"
  Shapes = -> [Cut016,Fusion052]
FEATURE [Part::MultiFuse] Fusion058  label="bottom006"
  Shapes = -> [Fusion056,Cut023]
FEATURE [Part::MultiFuse] Fusion059  label="bottom007"
  Shapes = -> [Fusion058,Fillet005]
FEATURE [Part::MultiFuse] Fusion060  label="bottom008"
  Shapes = -> [Fusion059,Fusion]
FEATURE [Part::MultiFuse] Fusion061  label="top011"
  Shapes = -> [Cut006,Cut020]
FEATURE [Part::MultiFuse] Fusion062  label="top012"
  Shapes = -> [Fusion057,Fusion061]
FEATURE [Sketcher::SketchObject] Sketch035  label="topSketch007"
  FullyConstrained = true
  sketch-geometry (6):
    g0: LineSegment StartX=19 StartY=38 StartZ=0 EndX=117 EndY=38 EndZ=0
    g1: ArcOfCircle CenterX=19 CenterY=19 CenterZ=0 NormalX=0 NormalY=0 NormalZ=1 AngleXU=0 Radius=19 StartAngle=1.5708 EndAngle=3.14159
    g2: LineSegment StartX=117 StartY=38 StartZ=0 EndX=117 EndY=19 EndZ=0
    g3: LineSegment StartX=98 StartY=1.0161e-12 StartZ=0 EndX=5.22862e-06 EndY=1.0161e-12 EndZ=0
    g4: LineSegment StartX=5.22862e-06 StartY=19 StartZ=0 EndX=5.22862e-06 EndY=1.0161e-12 EndZ=0
    g5: ArcOfCircle CenterX=98 CenterY=19 CenterZ=0 NormalX=0 NormalY=0 NormalZ=1 AngleXU=0 Radius=19 StartAngle=4.71239 EndAngle=6.28319
  constraints (16):
    c: Horizontal(g0)
    c: Distance(g0) = 98
    c: Coincident(g1,g0)
    c: Block(g1)
    c: Coincident(g2,g0)
    c: Vertical(g2)
    c: Distance(g2) = 19
    c: Horizontal(g3)
    c: Coincident(g4,g1)
    c: Vertical(g4)
    c: Coincident(g3,g4)
    c: Block(g3)
    c: Coincident(g5,g2)
    c: Coincident(g5,g3)
    c: Block(g0)
    c: Block(g5)
FEATURE [Part::Extrusion] Extrude026  label="sideA001"
  Base = -> Sketch035
  Dir = (0,0,1)
  DirMode = 2
  FaceMakerClass = Part::FaceMakerBullseye
  LengthFwd = 3
  LengthRev = 0
  Placement = pos=(0,0,-2.7) rot=(0,0,1;0rad)
  Solid = true
  Symmetric = false
FEATURE [Sketcher::SketchObject] Sketch036  label="topSketch008"
  FullyConstrained = true
  sketch-geometry (6):
    g0: LineSegment StartX=19 StartY=38 StartZ=0 EndX=117 EndY=38 EndZ=0
    g1: ArcOfCircle CenterX=19 CenterY=19 CenterZ=0 NormalX=0 NormalY=0 NormalZ=1 AngleXU=0 Radius=19 StartAngle=1.5708 EndAngle=3.14159
    g2: LineSegment StartX=117 StartY=38 StartZ=0 EndX=117 EndY=19 EndZ=0
    g3: LineSegment StartX=98 StartY=1.0161e-12 StartZ=0 EndX=5.22862e-06 EndY=1.0161e-12 EndZ=0
    g4: LineSegment StartX=5.22862e-06 StartY=19 StartZ=0 EndX=5.22862e-06 EndY=1.0161e-12 EndZ=0
    g5: ArcOfCircle CenterX=98 CenterY=19 CenterZ=0 NormalX=0 NormalY=0 NormalZ=1 AngleXU=0 Radius=19 StartAngle=4.71239 EndAngle=6.28319
  constraints (16):
    c: Horizontal(g0)
    c: Distance(g0) = 98
    c: Coincident(g1,g0)
    c: Block(g1)
    c: Coincident(g2,g0)
    c: Vertical(g2)
    c: Distance(g2) = 19
    c: Horizontal(g3)
    c: Coincident(g4,g1)
    c: Vertical(g4)
    c: Coincident(g3,g4)
    c: Block(g3)
    c: Coincident(g5,g2)
    c: Coincident(g5,g3)
    c: Block(g0)
    c: Block(g5)
FEATURE [Part::Extrusion] Extrude027  label="sideB001"
  Base = -> Sketch036
  Dir = (0,0,1)
  DirMode = 2
  FaceMakerClass = Part::FaceMakerBullseye
  LengthFwd = 3
  LengthRev = 0
  Placement = pos=(0,0,71.7) rot=(0,0,1;0rad)
  Solid = true
  Symmetric = false
FEATURE [Part::MultiFuse] Fusion064  label="removeFromBottom"
  Shapes = -> [Extrude026,Extrude027]
FEATURE [Part::Cut] Cut024  label="bottom009"
  Base = -> Fusion060
  Tool = -> Fusion064
FEATURE [Sketcher::SketchObject] Sketch037  label="topSketch009"
  FullyConstrained = true
  sketch-geometry (6):
    g0: ArcOfCircle CenterX=19 CenterY=19 CenterZ=0 NormalX=0 NormalY=0 NormalZ=1 AngleXU=0 Radius=19 StartAngle=1.5708 EndAngle=3.14159
    g1: LineSegment StartX=5.22862e-06 StartY=19 StartZ=0 EndX=5.22862e-06 EndY=1.19904e-11 EndZ=0
    g2: LineSegment StartX=19 StartY=38 StartZ=0 EndX=124 EndY=38 EndZ=0
    g3: LineSegment StartX=5.22862e-06 StartY=1.19904e-11 StartZ=0 EndX=105 EndY=1.19904e-11 EndZ=0
    g4: ArcOfCircle CenterX=105 CenterY=19 CenterZ=0 NormalX=0 NormalY=0 NormalZ=1 AngleXU=0 Radius=19 StartAngle=4.71239 EndAngle=6.28319
    g5: LineSegment StartX=124 StartY=38 StartZ=0 EndX=124 EndY=19 EndZ=0
  constraints (16):
    c: Block(g0)
    c: Coincident(g1,g0)
    c: Vertical(g1)
    c: Horizontal(g2)
    c: Distance(g2) = 105
    c: Coincident(g2,g0)
    c: Distance(g1) = 19
    c: Coincident(g3,g1)
    c: Horizontal(g3)
    c: Distance(g3) = 105
    c: Block(g4)
    c: Coincident(g4,g3)
    c: Coincident(g5,g2)
    c: Coincident(g5,g4)
    c: Vertical(g5)
    c: Distance(g5) = 19
FEATURE [Part::Extrusion] Extrude028  label="sideB"
  Base = -> Sketch037
  Dir = (0,0,1)
  DirMode = 2
  FaceMakerClass = Part::FaceMakerBullseye
  LengthFwd = 3
  LengthRev = 0
  Placement = pos=(0,0,72) rot=(0,0,1;0rad)
  Solid = true
  Symmetric = false
FEATURE [Sketcher::SketchObject] Sketch038  label="topSketch010"
  FullyConstrained = true
  sketch-geometry (22):
    g0: LineSegment StartX=5.21097e-06 StartY=3 StartZ=0 EndX=5.21097e-06 EndY=19 EndZ=0
    g1: ArcOfCircle CenterX=19 CenterY=19 CenterZ=0 NormalX=0 NormalY=0 NormalZ=1 AngleXU=0 Radius=19 StartAngle=1.5708 EndAngle=3.14159
    g2: ArcOfCircle CenterX=19 CenterY=19 CenterZ=0 NormalX=0 NormalY=0 NormalZ=1 AngleXU=0 Radius=16 StartAngle=1.5708 EndAngle=3.14159
    g3: LineSegment StartX=114 StartY=35 StartZ=0 EndX=19 EndY=35 EndZ=0
    g4: LineSegment StartX=5.21097e-06 StartY=3 StartZ=0 EndX=5.21097e-06 EndY=0 EndZ=0
    g5: LineSegment StartX=3 StartY=0 StartZ=0 EndX=5.21097e-06 EndY=0 EndZ=0
    g6: LineSegment StartX=3 StartY=19 StartZ=0 EndX=3 EndY=0 EndZ=0
    g7: LineSegment StartX=19 StartY=38 StartZ=0 EndX=124 EndY=38 EndZ=0
    g8: Circle CenterX=119 CenterY=35 CenterZ=0 NormalX=0 NormalY=0 NormalZ=1 AngleXU=0 Radius=1
    g9: Circle CenterX=121 CenterY=35 CenterZ=0 NormalX=0 NormalY=0 NormalZ=1 AngleXU=0 Radius=1
    g10: Circle CenterX=121 CenterY=33 CenterZ=0 NormalX=0 NormalY=0 NormalZ=1 AngleXU=0 Radius=1
    g11: BSplineCurve PolesCount=3 KnotsCount=2 Degree=2 IsPeriodic=0
    g12: GeomPoint X=119 Y=35 Z=0
    g13: GeomPoint X=121 Y=33 Z=0
    g14: LineSegment StartX=119 StartY=35 StartZ=0 EndX=114 EndY=35 EndZ=0
    g15: ArcOfCircle CenterX=105 CenterY=19 CenterZ=0 NormalX=0 NormalY=0 NormalZ=1 AngleXU=0 Radius=16 StartAngle=5.60905 EndAngle=6.28319
    g16: LineSegment StartX=121 StartY=33 StartZ=0 EndX=121 EndY=19 EndZ=0
    g17: LineSegment StartX=117.5 StartY=9.01251 StartZ=0 EndX=121.163 EndY=9.0125 EndZ=0
    g18: ArcOfCircle CenterX=105 CenterY=19 CenterZ=0 NormalX=0 NormalY=0 NormalZ=1 AngleXU=0 Radius=20.6155 StartAngle=5.7297 EndAngle=6.28319
    g19: LineSegment StartX=121.163 StartY=9.0125 StartZ=0 EndX=122.538 EndY=8.16329 EndZ=0
    g20: LineSegment StartX=124 StartY=38 StartZ=0 EndX=125.616 EndY=38 EndZ=0
    g21: LineSegment StartX=125.616 StartY=19 StartZ=0 EndX=125.616 EndY=38 EndZ=0
  constraints (49):
    c: Vertical(g0)
    c: Block(g0)
    c: Coincident(g1,g0)
    c: Block(g1)
    c: Coincident(g2,g1)
    c: Block(g2)
    c: Coincident(g3,g2)
    c: Horizontal(g3)
    c: Tangent(g3,g2)
    c: Coincident(g4,g0)
    c: Distance(g4) = 3
    c: Vertical(g4)
    c: Coincident(g5,g4)
    c: Horizontal(g5)
    c: Coincident(g6,g2)
    c: Coincident(g6,g5)
    c: Vertical(g6)
    c: Horizontal(g7)
    c: Distance(g7) = 105
    c: Coincident(g7,g1)
    c: Block(g3)
    c: Weight(g8) = 1
    c: Equal(g8,g9)
    c: Equal(g8,g10)
    c: InternalAlignment(g8,g11)
    c: InternalAlignment(g9,g11)
    c: InternalAlignment(g10,g11)
    c: InternalAlignment(g12,g11)
    c: InternalAlignment(g13,g11)
    c: Block(g11)
    c: Coincident(g14,g11)
    c: Coincident(g14,g3)
    c: Horizontal(g14)
    c: Block(g15)
    c: Coincident(g16,g11)
    c: Coincident(g16,g15)
    c: Vertical(g16)
    c: Distance(g16) = 14
    c: Coincident(g17,g15)
    c: Block(g18)
    c: Coincident(g19,g18)
    c: Coincident(g20,g7)
    c: Horizontal(g20)
    c: Vertical(g21)
    c: Coincident(g20,g21)
    c: Block(g20)
    c: Block(g21)
    c: Block(g19)
    c: Block(g17)
FEATURE [Part::Extrusion] Extrude029
  Base = -> Sketch038
  Dir = (0,0,1)
  DirMode = 2
  FaceMakerClass = Part::FaceMakerBullseye
  LengthFwd = 72
  LengthRev = 0
  Solid = true
  Symmetric = false
FEATURE [Part::Feature] Face085
  shape: bbox 4.8 x 25.5 x 2e-07 mm, 1 faces, 0 solids (baked)
FEATURE [Part::Revolution] Revolve089  label="moreFrontCaseScrewPost003"
  Angle = 360
  Axis = (0,1,0)
  Base = (0,0,0)
  FaceMakerClass = Part::FaceMakerBullseye
  Placement = pos=(109.5,4.5,3.5) rot=(0,0,1;0rad)
  Solid = false
  Source = -> Face085
  Symmetric = false
FEATURE [Part::Feature] Face086
  shape: bbox 4.8 x 25.5 x 2e-07 mm, 1 faces, 0 solids (baked)
FEATURE [Part::Revolution] Revolve090  label="moreFrontCaseScrewPost004"
  Angle = 360
  Axis = (0,1,0)
  Base = (0,0,0)
  FaceMakerClass = Part::FaceMakerBullseye
  Placement = pos=(109.5,4.5,68.5) rot=(0,0,1;0rad)
  Solid = false
  Source = -> Face086
  Symmetric = false
FEATURE [Part::Fillet] Fillet026  label="top013"
  Base = -> Extrude029
  Edges = 1 edges r=2: [Edge35]
FEATURE [Sketcher::SketchObject] Sketch039
  FullyConstrained = true
  sketch-geometry (7):
    g0: LineSegment StartX=0 StartY=0 StartZ=0 EndX=0 EndY=6 EndZ=0
    g1: Circle CenterX=0 CenterY=0 CenterZ=0 NormalX=0 NormalY=0 NormalZ=1 AngleXU=0 Radius=1
    g2: Circle CenterX=8 CenterY=6 CenterZ=0 NormalX=0 NormalY=0 NormalZ=1 AngleXU=0 Radius=1
    g3: BSplineCurve PolesCount=3 KnotsCount=2 Degree=2 IsPeriodic=0
    g4: GeomPoint X=0 Y=0 Z=0
    g5: GeomPoint X=8 Y=6 Z=0
    g6: LineSegment StartX=0 StartY=6 StartZ=0 EndX=8 EndY=6 EndZ=0
  constraints (14):
    c: Coincident(g0,g-1)
    c: Distance(g0) = 6
    c: Vertical(g0)
    c: Coincident(g3,g0)
    c: Weight(g1) = 1
    c: Equal(g1,g2)
    c: InternalAlignment(g1,g3)
    c: InternalAlignment(g2,g3)
    c: InternalAlignment(g4,g3)
    c: InternalAlignment(g5,g3)
    c: Block(g3)
    c: Coincident(g6,g0)
    c: Coincident(g6,g3)
    c: Horizontal(g6)
FEATURE [Sketcher::SketchObject] Sketch040
  FullyConstrained = true
  sketch-geometry (7):
    g0: LineSegment StartX=0 StartY=0 StartZ=0 EndX=0 EndY=6 EndZ=0
    g1: Circle CenterX=0 CenterY=0 CenterZ=0 NormalX=0 NormalY=0 NormalZ=1 AngleXU=0 Radius=1
    g2: Circle CenterX=8 CenterY=6 CenterZ=0 NormalX=0 NormalY=0 NormalZ=1 AngleXU=0 Radius=1
    g3: BSplineCurve PolesCount=3 KnotsCount=2 Degree=2 IsPeriodic=0
    g4: GeomPoint X=0 Y=0 Z=0
    g5: GeomPoint X=8 Y=6 Z=0
    g6: LineSegment StartX=0 StartY=6 StartZ=0 EndX=8 EndY=6 EndZ=0
  constraints (14):
    c: Coincident(g0,g-1)
    c: Distance(g0) = 6
    c: Vertical(g0)
    c: Coincident(g3,g0)
    c: Weight(g1) = 1
    c: Equal(g1,g2)
    c: InternalAlignment(g1,g3)
    c: InternalAlignment(g2,g3)
    c: InternalAlignment(g4,g3)
    c: InternalAlignment(g5,g3)
    c: Block(g3)
    c: Coincident(g6,g0)
    c: Coincident(g6,g3)
    c: Horizontal(g6)
FEATURE [Sketcher::SketchObject] Sketch041
  FullyConstrained = true
  sketch-geometry (7):
    g0: LineSegment StartX=0 StartY=0 StartZ=0 EndX=0 EndY=6 EndZ=0
    g1: Circle CenterX=0 CenterY=0 CenterZ=0 NormalX=0 NormalY=0 NormalZ=1 AngleXU=0 Radius=1
    g2: Circle CenterX=8 CenterY=6 CenterZ=0 NormalX=0 NormalY=0 NormalZ=1 AngleXU=0 Radius=1
    g3: BSplineCurve PolesCount=3 KnotsCount=2 Degree=2 IsPeriodic=0
    g4: GeomPoint X=0 Y=0 Z=0
    g5: GeomPoint X=8 Y=6 Z=0
    g6: LineSegment StartX=0 StartY=6 StartZ=0 EndX=8 EndY=6 EndZ=0
  constraints (14):
    c: Coincident(g0,g-1)
    c: Distance(g0) = 6
    c: Vertical(g0)
    c: Coincident(g3,g0)
    c: Weight(g1) = 1
    c: Equal(g1,g2)
    c: InternalAlignment(g1,g3)
    c: InternalAlignment(g2,g3)
    c: InternalAlignment(g4,g3)
    c: InternalAlignment(g5,g3)
    c: Block(g3)
    c: Coincident(g6,g0)
    c: Coincident(g6,g3)
    c: Horizontal(g6)
FEATURE [Sketcher::SketchObject] Sketch042
  FullyConstrained = true
  sketch-geometry (7):
    g0: LineSegment StartX=0 StartY=0 StartZ=0 EndX=0 EndY=6 EndZ=0
    g1: Circle CenterX=0 CenterY=0 CenterZ=0 NormalX=0 NormalY=0 NormalZ=1 AngleXU=0 Radius=1
    g2: Circle CenterX=8 CenterY=6 CenterZ=0 NormalX=0 NormalY=0 NormalZ=1 AngleXU=0 Radius=1
    g3: BSplineCurve PolesCount=3 KnotsCount=2 Degree=2 IsPeriodic=0
    g4: GeomPoint X=0 Y=0 Z=0
    g5: GeomPoint X=8 Y=6 Z=0
    g6: LineSegment StartX=0 StartY=6 StartZ=0 EndX=8 EndY=6 EndZ=0
  constraints (14):
    c: Coincident(g0,g-1)
    c: Distance(g0) = 6
    c: Vertical(g0)
    c: Coincident(g3,g0)
    c: Weight(g1) = 1
    c: Equal(g1,g2)
    c: InternalAlignment(g1,g3)
    c: InternalAlignment(g2,g3)
    c: InternalAlignment(g4,g3)
    c: InternalAlignment(g5,g3)
    c: Block(g3)
    c: Coincident(g6,g0)
    c: Coincident(g6,g3)
    c: Horizontal(g6)
FEATURE [Part::Extrusion] Extrude030  label="caseScrewPillarBracket008"
  Base = -> Sketch039
  Dir = (0,0,1)
  DirMode = 2
  FaceMakerClass = Part::FaceMakerBullseye
  LengthFwd = 2.4
  LengthRev = 0
  Placement = pos=(15.76,29,8.8) rot=(0,1,0;0rad)
  Solid = true
  Symmetric = false
FEATURE [Part::Extrusion] Extrude031  label="caseScrewPillarBracket009"
  Base = -> Sketch040
  Dir = (0,0,1)
  DirMode = 2
  FaceMakerClass = Part::FaceMakerBullseye
  LengthFwd = 2.4
  LengthRev = 0
  Placement = pos=(15.76,29,60.8) rot=(0,0,1;0rad)
  Solid = true
  Symmetric = false
FEATURE [Part::Extrusion] Extrude032  label="caseScrewPillarBracket010"
  Base = -> Sketch041
  Dir = (0,0,1)
  DirMode = 2
  FaceMakerClass = Part::FaceMakerBullseye
  LengthFwd = 2.4
  LengthRev = 0
  Placement = pos=(13.7,29,13.26) rot=(0,-1,0;1.5708rad)
  Solid = true
  Symmetric = false
FEATURE [Part::Extrusion] Extrude033  label="caseScrewPillarBracket011"
  Base = -> Sketch042
  Dir = (0,0,1)
  DirMode = 2
  FaceMakerClass = Part::FaceMakerBullseye
  LengthFwd = 2.4
  LengthRev = 0
  Placement = pos=(11.3,29,58.74) rot=(0,1,0;1.5708rad)
  Solid = true
  Symmetric = false
FEATURE [Sketcher::SketchObject] Sketch043
  FullyConstrained = true
  sketch-geometry (7):
    g0: LineSegment StartX=0 StartY=0 StartZ=0 EndX=0 EndY=6 EndZ=0
    g1: Circle CenterX=0 CenterY=0 CenterZ=0 NormalX=0 NormalY=0 NormalZ=1 AngleXU=0 Radius=1
    g2: Circle CenterX=8 CenterY=6 CenterZ=0 NormalX=0 NormalY=0 NormalZ=1 AngleXU=0 Radius=1
    g3: BSplineCurve PolesCount=3 KnotsCount=2 Degree=2 IsPeriodic=0
    g4: GeomPoint X=0 Y=0 Z=0
    g5: GeomPoint X=8 Y=6 Z=0
    g6: LineSegment StartX=0 StartY=6 StartZ=0 EndX=8 EndY=6 EndZ=0
  constraints (14):
    c: Coincident(g0,g-1)
    c: Distance(g0) = 6
    c: Vertical(g0)
    c: Coincident(g3,g0)
    c: Weight(g1) = 1
    c: Equal(g1,g2)
    c: InternalAlignment(g1,g3)
    c: InternalAlignment(g2,g3)
    c: InternalAlignment(g4,g3)
    c: InternalAlignment(g5,g3)
    c: Block(g3)
    c: Coincident(g6,g0)
    c: Coincident(g6,g3)
    c: Horizontal(g6)
FEATURE [Part::Extrusion] Extrude034  label="caseScrewPillarBracket012"
  Base = -> Sketch043
  Dir = (0,0,1)
  DirMode = 2
  FaceMakerClass = Part::FaceMakerBullseye
  LengthFwd = 2.4
  LengthRev = 0
  Placement = pos=(88.3,29,65.23) rot=(0,1,0;1.5708rad)
  Solid = true
  Symmetric = false
FEATURE [Sketcher::SketchObject] Sketch044
  FullyConstrained = true
  sketch-geometry (7):
    g0: LineSegment StartX=0 StartY=0 StartZ=0 EndX=0 EndY=6 EndZ=0
    g1: Circle CenterX=0 CenterY=0 CenterZ=0 NormalX=0 NormalY=0 NormalZ=1 AngleXU=0 Radius=1
    g2: Circle CenterX=8 CenterY=6 CenterZ=0 NormalX=0 NormalY=0 NormalZ=1 AngleXU=0 Radius=1
    g3: BSplineCurve PolesCount=3 KnotsCount=2 Degree=2 IsPeriodic=0
    g4: GeomPoint X=0 Y=0 Z=0
    g5: GeomPoint X=8 Y=6 Z=0
    g6: LineSegment StartX=0 StartY=6 StartZ=0 EndX=8 EndY=6 EndZ=0
  constraints (14):
    c: Coincident(g0,g-1)
    c: Distance(g0) = 6
    c: Vertical(g0)
    c: Coincident(g3,g0)
    c: Weight(g1) = 1
    c: Equal(g1,g2)
    c: InternalAlignment(g1,g3)
    c: InternalAlignment(g2,g3)
    c: InternalAlignment(g4,g3)
    c: InternalAlignment(g5,g3)
    c: Block(g3)
    c: Coincident(g6,g0)
    c: Coincident(g6,g3)
    c: Horizontal(g6)
FEATURE [Part::Extrusion] Extrude035  label="caseScrewPillarBracket013"
  Base = -> Sketch044
  Dir = (0,0,1)
  DirMode = 2
  FaceMakerClass = Part::FaceMakerBullseye
  LengthFwd = 2.4
  LengthRev = 0
  Placement = pos=(90.7,29,6.77) rot=(0,-1,0;1.5708rad)
  Solid = true
  Symmetric = false
FEATURE [Sketcher::SketchObject] Sketch045
  FullyConstrained = true
  sketch-geometry (7):
    g0: LineSegment StartX=0 StartY=0 StartZ=0 EndX=0 EndY=6 EndZ=0
    g1: Circle CenterX=0 CenterY=0 CenterZ=0 NormalX=0 NormalY=0 NormalZ=1 AngleXU=0 Radius=1
    g2: Circle CenterX=8 CenterY=6 CenterZ=0 NormalX=0 NormalY=0 NormalZ=1 AngleXU=0 Radius=1
    g3: BSplineCurve PolesCount=3 KnotsCount=2 Degree=2 IsPeriodic=0
    g4: GeomPoint X=0 Y=0 Z=0
    g5: GeomPoint X=8 Y=6 Z=0
    g6: LineSegment StartX=0 StartY=6 StartZ=0 EndX=8 EndY=6 EndZ=0
  constraints (14):
    c: Coincident(g0,g-1)
    c: Distance(g0) = 6
    c: Vertical(g0)
    c: Coincident(g3,g0)
    c: Weight(g1) = 1
    c: Equal(g1,g2)
    c: InternalAlignment(g1,g3)
    c: InternalAlignment(g2,g3)
    c: InternalAlignment(g4,g3)
    c: InternalAlignment(g5,g3)
    c: Block(g3)
    c: Coincident(g6,g0)
    c: Coincident(g6,g3)
    c: Horizontal(g6)
FEATURE [Sketcher::SketchObject] Sketch046
  FullyConstrained = true
  sketch-geometry (7):
    g0: LineSegment StartX=0 StartY=0 StartZ=0 EndX=0 EndY=6 EndZ=0
    g1: Circle CenterX=0 CenterY=0 CenterZ=0 NormalX=0 NormalY=0 NormalZ=1 AngleXU=0 Radius=1
    g2: Circle CenterX=8 CenterY=6 CenterZ=0 NormalX=0 NormalY=0 NormalZ=1 AngleXU=0 Radius=1
    g3: BSplineCurve PolesCount=3 KnotsCount=2 Degree=2 IsPeriodic=0
    g4: GeomPoint X=0 Y=0 Z=0
    g5: GeomPoint X=8 Y=6 Z=0
    g6: LineSegment StartX=0 StartY=6 StartZ=0 EndX=8 EndY=6 EndZ=0
  constraints (14):
    c: Coincident(g0,g-1)
    c: Distance(g0) = 6
    c: Vertical(g0)
    c: Coincident(g3,g0)
    c: Weight(g1) = 1
    c: Equal(g1,g2)
    c: InternalAlignment(g1,g3)
    c: InternalAlignment(g2,g3)
    c: InternalAlignment(g4,g3)
    c: InternalAlignment(g5,g3)
    c: Block(g3)
    c: Coincident(g6,g0)
    c: Coincident(g6,g3)
    c: Horizontal(g6)
FEATURE [Part::Extrusion] Extrude036  label="caseScrewPillarBracket014"
  Base = -> Sketch045
  Dir = (0,0,1)
  DirMode = 2
  FaceMakerClass = Part::FaceMakerBullseye
  LengthFwd = 2.4
  LengthRev = 0
  Placement = pos=(110.7,29,6.77) rot=(0,-1,0;1.5708rad)
  Solid = true
  Symmetric = false
FEATURE [Part::Extrusion] Extrude037  label="caseScrewPillarBracket015"
  Base = -> Sketch046
  Dir = (0,0,1)
  DirMode = 2
  FaceMakerClass = Part::FaceMakerBullseye
  LengthFwd = 2.4
  LengthRev = 0
  Placement = pos=(108.3,29,65.23) rot=(0,1,0;1.5708rad)
  Solid = true
  Symmetric = false
FEATURE [Part::Box] Box013  label="frontCaseScrewPillarBracket002"
  AttacherType = Attacher::AttachEngine3D
  Height = 2.4
  Length = 22
  Placement = pos=(87,28,2.3) rot=(0,0,1;0rad)
  Width = 7
FEATURE [Part::Box] Box014  label="frontCaseScrewPillarBracket003"
  AttacherType = Attacher::AttachEngine3D
  Height = 2.4
  Length = 22
  Placement = pos=(87,28,67.3) rot=(0,0,1;0rad)
  Width = 7
FEATURE [Part::Feature] Face087
  shape: bbox 4.8 x 30.2 x 2e-07 mm, 1 faces, 0 solids (baked)
FEATURE [Part::Revolution] Revolve091  label="frontCaseScrewPost004"
  Angle = 360
  Axis = (0,1,0)
  Base = (0,0,0)
  FaceMakerClass = Part::FaceMakerBullseye
  Placement = pos=(89.5,4.5,3.5) rot=(0,0,1;0rad)
  Solid = false
  Source = -> Face087
  Symmetric = false
FEATURE [Part::Feature] Face088
  shape: bbox 4.8 x 30.2 x 2e-07 mm, 1 faces, 0 solids (baked)
FEATURE [Part::Revolution] Revolve092  label="frontCaseScrewPost005"
  Angle = 360
  Axis = (0,1,0)
  Base = (0,0,0)
  FaceMakerClass = Part::FaceMakerBullseye
  Placement = pos=(89.5,4.5,68.5) rot=(0,0,1;0rad)
  Solid = false
  Source = -> Face088
  Symmetric = false
FEATURE [Part::Feature] Face089
  shape: bbox 3.5 x 30.2 x 2e-07 mm, 1 faces, 0 solids (baked)
FEATURE [Part::Revolution] Revolve093  label="backCaseScrewPost002"
  Angle = 360
  Axis = (0,1,0)
  Base = (0,0,0)
  FaceMakerClass = Part::FaceMakerBullseye
  Placement = pos=(12.5,4.5,10) rot=(0,0,1;0rad)
  Solid = false
  Source = -> Face089
  Symmetric = false
FEATURE [Part::Feature] Face090
  shape: bbox 3.5 x 30.2 x 2e-07 mm, 1 faces, 0 solids (baked)
FEATURE [Part::Revolution] Revolve094  label="backCaseScrewPost003"
  Angle = 360
  Axis = (0,1,0)
  Base = (0,0,0)
  FaceMakerClass = Part::FaceMakerBullseye
  Placement = pos=(12.5,4.5,62) rot=(0,0,1;0rad)
  Solid = false
  Source = -> Face090
  Symmetric = false
FEATURE [Part::Box] Box015  label="Cube011"
  AttacherType = Attacher::AttachEngine3D
  Height = 28.8
  Length = 3
  Placement = pos=(107.3,28,21.6) rot=(0,0,1;0rad)
  Width = 7
FEATURE [Part::Box] Box016  label="Cube012"
  AttacherType = Attacher::AttachEngine3D
  Height = 3
  Length = 7.4
  Placement = pos=(107.3,28,18.6) rot=(0,0,1;0rad)
  Width = 7
FEATURE [Part::Box] Box017  label="Cube013"
  AttacherType = Attacher::AttachEngine3D
  Height = 3
  Length = 7.4
  Placement = pos=(107.3,28,50.4) rot=(0,0,1;0rad)
  Width = 7
FEATURE [Part::Cylinder] Cylinder024
  Angle = 360
  AttacherType = Attacher::AttachEngine3D
  Height = 20
  Placement = pos=(0,0,36.15) rot=(0,0,1;0rad)
  Radius = 14.3
FEATURE [Part::Cylinder] Cylinder025
  Angle = 360
  AttacherType = Attacher::AttachEngine3D
  Height = 10
  Placement = pos=(0,0,36.15) rot=(0,0,1;0rad)
  Radius = 4
FEATURE [Part::MultiFuse] Fusion066  label="removeToCreteHoleForPlugHousing009"
  Placement = pos=(70,19,36) rot=(0,1,0;1.5708rad)
  Shapes = -> [Cylinder024,Cylinder025]
FEATURE [Part::MultiFuse] Fusion065  label="plugHousingBracketHolder002"
  Shapes = -> [Box017,Box015,Box016]
FEATURE [Part::Cut] Cut025  label="plugHousingBracketHolder003"
  Base = -> Fusion065
  Placement = pos=(7,0,0) rot=(0,0,1;0rad)
  Tool = -> Fusion066
FEATURE [Sketcher::SketchObject] Sketch047
  FullyConstrained = false
  Placement = pos=(0,0,0) rot=(1,0,0;1.5708rad)
  sketch-geometry (24):
    g0: ArcOfCircle CenterX=-4 CenterY=-10.5 CenterZ=0 NormalX=0 NormalY=0 NormalZ=1 AngleXU=0 Radius=1.5 StartAngle=6e-16 EndAngle=3.14159
    g1: ArcOfCircle CenterX=-34.2 CenterY=-10.5 CenterZ=0 NormalX=0 NormalY=0 NormalZ=1 AngleXU=0 Radius=1.5 StartAngle=0 EndAngle=3.14159
    g2: ArcOfCircle CenterX=-34.2 CenterY=-27.7 CenterZ=0 NormalX=0 NormalY=0 NormalZ=1 AngleXU=0 Radius=1.5 StartAngle=3.14159 EndAngle=6.28319
    g3: ArcOfCircle CenterX=-4 CenterY=-27.7 CenterZ=0 NormalX=0 NormalY=0 NormalZ=1 AngleXU=0 Radius=1.5 StartAngle=3.1416 EndAngle=6.28319
    g4: ArcOfCircle CenterX=-10 CenterY=-4.3 CenterZ=0 NormalX=0 NormalY=0 NormalZ=1 AngleXU=0 Radius=1.5 StartAngle=2e-16 EndAngle=3.14159
    g5: ArcOfCircle CenterX=-16.1 CenterY=-1.8 CenterZ=0 NormalX=0 NormalY=0 NormalZ=1 AngleXU=0 Radius=1.5 StartAngle=5e-16 EndAngle=3.14159
    g6: ArcOfCircle CenterX=-22.1 CenterY=-1.8 CenterZ=0 NormalX=0 NormalY=0 NormalZ=1 AngleXU=0 Radius=1.5 StartAngle=5e-16 EndAngle=3.14159
    g7: ArcOfCircle CenterX=-28.2 CenterY=-4.3 CenterZ=0 NormalX=0 NormalY=0 NormalZ=1 AngleXU=0 Radius=1.5 StartAngle=2e-16 EndAngle=3.14159
    g8: ArcOfCircle CenterX=-10 CenterY=-33.9 CenterZ=0 NormalX=0 NormalY=0 NormalZ=1 AngleXU=0 Radius=1.5 StartAngle=3.14159 EndAngle=6.28319
    g9: ArcOfCircle CenterX=-16.1 CenterY=-36.4 CenterZ=0 NormalX=0 NormalY=0 NormalZ=1 AngleXU=0 Radius=1.5 StartAngle=3.14159 EndAngle=6.28319
    g10: ArcOfCircle CenterX=-22.1 CenterY=-36.4 CenterZ=0 NormalX=0 NormalY=0 NormalZ=1 AngleXU=0 Radius=1.5 StartAngle=3.14159 EndAngle=6.28319
    g11: ArcOfCircle CenterX=-28.2 CenterY=-33.9 CenterZ=0 NormalX=0 NormalY=0 NormalZ=1 AngleXU=0 Radius=1.5 StartAngle=3.14159 EndAngle=6.28319
    g12: LineSegment StartX=-35.7 StartY=-10.5 StartZ=0 EndX=-35.7 EndY=-27.7 EndZ=0
    g13: LineSegment StartX=-32.7 StartY=-10.5 StartZ=0 EndX=-32.7 EndY=-27.7 EndZ=0
    g14: LineSegment StartX=-29.7 StartY=-33.9 StartZ=0 EndX=-29.7 EndY=-4.3 EndZ=0
    g15: LineSegment StartX=-26.7 StartY=-33.9 StartZ=0 EndX=-26.7 EndY=-4.3 EndZ=0
    g16: LineSegment StartX=-2.5 StartY=-10.5 StartZ=0 EndX=-2.5 EndY=-27.7 EndZ=0
    g17: LineSegment StartX=-8.5 StartY=-4.3 StartZ=0 EndX=-8.5 EndY=-33.9 EndZ=0
    g18: LineSegment StartX=-5.5 StartY=-10.5 StartZ=0 EndX=-5.5 EndY=-27.7 EndZ=0
    g19: LineSegment StartX=-11.5 StartY=-4.3 StartZ=0 EndX=-11.5 EndY=-33.9 EndZ=0
    g20: LineSegment StartX=-14.6 StartY=-1.8 StartZ=0 EndX=-14.6 EndY=-36.4 EndZ=0
    g21: LineSegment StartX=-17.6 StartY=-1.8 StartZ=0 EndX=-17.6 EndY=-36.4 EndZ=0
    g22: LineSegment StartX=-20.6 StartY=-36.4 StartZ=0 EndX=-20.6 EndY=-1.8 EndZ=0
    g23: LineSegment StartX=-23.6 StartY=-1.8 StartZ=0 EndX=-23.6 EndY=-36.4 EndZ=0
  constraints (48):
    c: Block(g0)
    c: Block(g1)
    c: Block(g2)
    c: Block(g3)
    c: Block(g4)
    c: Block(g5)
    c: Block(g6)
    c: Block(g7)
    c: Block(g8)
    c: Block(g9)
    c: Block(g10)
    c: Block(g11)
    c: Coincident(g12,g1)
    c: Coincident(g12,g2)
    c: Vertical(g12)
    c: Coincident(g13,g1)
    c: Coincident(g13,g2)
    c: Vertical(g13)
    c: Coincident(g14,g11)
    c: Coincident(g14,g7)
    c: Vertical(g14)
    c: Coincident(g15,g11)
    c: Coincident(g15,g7)
    c: Vertical(g15)
    c: Coincident(g16,g0)
    c: Coincident(g16,g3)
    c: Vertical(g16)
    c: Coincident(g17,g4)
    c: Coincident(g17,g8)
    c: Vertical(g17)
    c: Coincident(g18,g0)
    c: Coincident(g18,g3)
    c: Vertical(g18)
    c: Coincident(g19,g4)
    c: Coincident(g19,g8)
    c: Vertical(g19)
    c: Coincident(g20,g5)
    c: Coincident(g20,g9)
    c: Vertical(g20)
    c: Coincident(g21,g5)
    c: Coincident(g21,g9)
    c: Vertical(g21)
    c: Coincident(g22,g10)
    c: Coincident(g22,g6)
    c: Vertical(g22)
    c: Coincident(g23,g6)
    c: Coincident(g23,g10)
    c: Vertical(g23)
FEATURE [Part::Extrusion] Extrude038  label="removeToCreateFanGrillHoles001"
  Base = -> Sketch047
  Dir = (0,-1,6e-16)
  DirMode = 2
  FaceMakerClass = Part::FaceMakerBullseye
  LengthFwd = 10
  LengthRev = 0
  Placement = pos=(65.4,44,54.82) rot=(0,0,1;0rad)
  Solid = true
  Symmetric = false
FEATURE [Part::Feature] Wire004
  shape: bbox 11 x 5.2 x 2e-07 mm, 0 faces, 0 solids (baked)
FEATURE [Part::Revolution] Revolve095
  Angle = 360
  Axis = (0,1,0)
  Base = (0,0,0)
  FaceMakerClass = Part::FaceMakerBullseye
  Placement = pos=(30.3,38,19.7) rot=(0,0,1;0rad)
  Solid = true
  Source = -> Wire004
  Symmetric = false
FEATURE [Part::Feature] Wire005
  shape: bbox 11 x 5.2 x 2e-07 mm, 0 faces, 0 solids (baked)
FEATURE [Part::Revolution] Revolve096
  Angle = 360
  Axis = (0,1,0)
  Base = (0,0,0)
  FaceMakerClass = Part::FaceMakerBullseye
  Placement = pos=(30.3,38,51.7) rot=(0,0,1;0rad)
  Solid = true
  Source = -> Wire005
  Symmetric = false
FEATURE [Part::Feature] Wire006
  shape: bbox 11 x 5.2 x 2e-07 mm, 0 faces, 0 solids (baked)
FEATURE [Part::Revolution] Revolve097
  Angle = 360
  Axis = (0,1,0)
  Base = (0,0,0)
  FaceMakerClass = Part::FaceMakerBullseye
  Placement = pos=(62.3,38,51.7) rot=(0,0,1;0rad)
  Solid = true
  Source = -> Wire006
  Symmetric = false
FEATURE [Part::Feature] Wire007
  shape: bbox 11 x 5.2 x 2e-07 mm, 0 faces, 0 solids (baked)
FEATURE [Part::Revolution] Revolve098
  Angle = 360
  Axis = (0,1,0)
  Base = (0,0,0)
  FaceMakerClass = Part::FaceMakerBullseye
  Placement = pos=(62.3,38,19.7) rot=(0,0,1;0rad)
  Solid = true
  Source = -> Wire007
  Symmetric = false
FEATURE [Part::MultiFuse] Fusion067  label="fanScrewHousing002"
  Shapes = -> [Revolve098,Revolve097,Revolve096,Revolve095]
FEATURE [Part::Feature] Face091 .. Face094  x4 (patterned run collapsed; names and placements below)
  shape: bbox 3.5 x 17.8 x 2e-07 mm, 1 faces, 0 solids (baked)
FEATURE [Part::Revolution] Revolve099  label="removeToCreateScrewAndThreadedInsertHole026"
  Angle = 360
  Axis = (0,1,0)
  Base = (0,0,0)
  FaceMakerClass = Part::FaceMakerBullseye
  Placement = pos=(62.3,30.3,19.7) rot=(0,0,1;0rad)
  Solid = false
  Source = -> Face091
  Symmetric = false
FEATURE [Part::Revolution] Revolve100  label="removeToCreateScrewAndThreadedInsertHole027"
  Angle = 360
  Axis = (0,1,0)
  Base = (0,0,0)
  FaceMakerClass = Part::FaceMakerBullseye
  Placement = pos=(62.3,30.3,51.7) rot=(0,0,1;0rad)
  Solid = false
  Source = -> Face092
  Symmetric = false
FEATURE [Part::Revolution] Revolve101  label="removeToCreateScrewAndThreadedInsertHole028"
  Angle = 360
  Axis = (0,1,0)
  Base = (0,0,0)
  FaceMakerClass = Part::FaceMakerBullseye
  Placement = pos=(30.3,30.3,19.7) rot=(0,0,1;0rad)
  Solid = false
  Source = -> Face093
  Symmetric = false
FEATURE [Part::Revolution] Revolve102  label="removeToCreateScrewAndThreadedInsertHole029"
  Angle = 360
  Axis = (0,1,0)
  Base = (0,0,0)
  FaceMakerClass = Part::FaceMakerBullseye
  Placement = pos=(30.3,30.3,51.7) rot=(0,0,1;0rad)
  Solid = false
  Source = -> Face094
  Symmetric = false
FEATURE [Part::MultiFuse] Fusion068  label="createThreadedInsertHolesForFan002"
  Shapes = -> [Revolve099,Revolve100,Revolve101,Revolve102]
FEATURE [Part::Cut] Cut026  label="fanScrewHousing003"
  Base = -> Fusion067
  Tool = -> Fusion068
FEATURE [Sketcher::SketchObject] Sketch048
  FullyConstrained = false
  Placement = pos=(0,0,0) rot=(1,0,0;1.5708rad)
  sketch-geometry (24):
    g0: ArcOfCircle CenterX=-4 CenterY=-10.5 CenterZ=0 NormalX=0 NormalY=0 NormalZ=1 AngleXU=0 Radius=1.5 StartAngle=6e-16 EndAngle=3.14159
    g1: ArcOfCircle CenterX=-34.2 CenterY=-10.5 CenterZ=0 NormalX=0 NormalY=0 NormalZ=1 AngleXU=0 Radius=1.5 StartAngle=0 EndAngle=3.14159
    g2: ArcOfCircle CenterX=-34.2 CenterY=-27.7 CenterZ=0 NormalX=0 NormalY=0 NormalZ=1 AngleXU=0 Radius=1.5 StartAngle=3.14159 EndAngle=6.28319
    g3: ArcOfCircle CenterX=-4 CenterY=-27.7 CenterZ=0 NormalX=0 NormalY=0 NormalZ=1 AngleXU=0 Radius=1.5 StartAngle=3.1416 EndAngle=6.28319
    g4: ArcOfCircle CenterX=-10 CenterY=-4.3 CenterZ=0 NormalX=0 NormalY=0 NormalZ=1 AngleXU=0 Radius=1.5 StartAngle=2e-16 EndAngle=3.14159
    g5: ArcOfCircle CenterX=-16.1 CenterY=-1.8 CenterZ=0 NormalX=0 NormalY=0 NormalZ=1 AngleXU=0 Radius=1.5 StartAngle=5e-16 EndAngle=3.14159
    g6: ArcOfCircle CenterX=-22.1 CenterY=-1.8 CenterZ=0 NormalX=0 NormalY=0 NormalZ=1 AngleXU=0 Radius=1.5 StartAngle=5e-16 EndAngle=3.14159
    g7: ArcOfCircle CenterX=-28.2 CenterY=-4.3 CenterZ=0 NormalX=0 NormalY=0 NormalZ=1 AngleXU=0 Radius=1.5 StartAngle=2e-16 EndAngle=3.14159
    g8: ArcOfCircle CenterX=-10 CenterY=-33.9 CenterZ=0 NormalX=0 NormalY=0 NormalZ=1 AngleXU=0 Radius=1.5 StartAngle=3.14159 EndAngle=6.28319
    g9: ArcOfCircle CenterX=-16.1 CenterY=-36.4 CenterZ=0 NormalX=0 NormalY=0 NormalZ=1 AngleXU=0 Radius=1.5 StartAngle=3.14159 EndAngle=6.28319
    g10: ArcOfCircle CenterX=-22.1 CenterY=-36.4 CenterZ=0 NormalX=0 NormalY=0 NormalZ=1 AngleXU=0 Radius=1.5 StartAngle=3.14159 EndAngle=6.28319
    g11: ArcOfCircle CenterX=-28.2 CenterY=-33.9 CenterZ=0 NormalX=0 NormalY=0 NormalZ=1 AngleXU=0 Radius=1.5 StartAngle=3.14159 EndAngle=6.28319
    g12: LineSegment StartX=-35.7 StartY=-10.5 StartZ=0 EndX=-35.7 EndY=-27.7 EndZ=0
    g13: LineSegment StartX=-32.7 StartY=-10.5 StartZ=0 EndX=-32.7 EndY=-27.7 EndZ=0
    g14: LineSegment StartX=-29.7 StartY=-33.9 StartZ=0 EndX=-29.7 EndY=-4.3 EndZ=0
    g15: LineSegment StartX=-26.7 StartY=-33.9 StartZ=0 EndX=-26.7 EndY=-4.3 EndZ=0
    g16: LineSegment StartX=-2.5 StartY=-10.5 StartZ=0 EndX=-2.5 EndY=-27.7 EndZ=0
    g17: LineSegment StartX=-8.5 StartY=-4.3 StartZ=0 EndX=-8.5 EndY=-33.9 EndZ=0
    g18: LineSegment StartX=-5.5 StartY=-10.5 StartZ=0 EndX=-5.5 EndY=-27.7 EndZ=0
    g19: LineSegment StartX=-11.5 StartY=-4.3 StartZ=0 EndX=-11.5 EndY=-33.9 EndZ=0
    g20: LineSegment StartX=-14.6 StartY=-1.8 StartZ=0 EndX=-14.6 EndY=-36.4 EndZ=0
    g21: LineSegment StartX=-17.6 StartY=-1.8 StartZ=0 EndX=-17.6 EndY=-36.4 EndZ=0
    g22: LineSegment StartX=-20.6 StartY=-36.4 StartZ=0 EndX=-20.6 EndY=-1.8 EndZ=0
    g23: LineSegment StartX=-23.6 StartY=-1.8 StartZ=0 EndX=-23.6 EndY=-36.4 EndZ=0
  constraints (48):
    c: Block(g0)
    c: Block(g1)
    c: Block(g2)
    c: Block(g3)
    c: Block(g4)
    c: Block(g5)
    c: Block(g6)
    c: Block(g7)
    c: Block(g8)
    c: Block(g9)
    c: Block(g10)
    c: Block(g11)
    c: Coincident(g12,g1)
    c: Coincident(g12,g2)
    c: Vertical(g12)
    c: Coincident(g13,g1)
    c: Coincident(g13,g2)
    c: Vertical(g13)
    c: Coincident(g14,g11)
    c: Coincident(g14,g7)
    c: Vertical(g14)
    c: Coincident(g15,g11)
    c: Coincident(g15,g7)
    c: Vertical(g15)
    c: Coincident(g16,g0)
    c: Coincident(g16,g3)
    c: Vertical(g16)
    c: Coincident(g17,g4)
    c: Coincident(g17,g8)
    c: Vertical(g17)
    c: Coincident(g18,g0)
    c: Coincident(g18,g3)
    c: Vertical(g18)
    c: Coincident(g19,g4)
    c: Coincident(g19,g8)
    c: Vertical(g19)
    c: Coincident(g20,g5)
    c: Coincident(g20,g9)
    c: Vertical(g20)
    c: Coincident(g21,g5)
    c: Coincident(g21,g9)
    c: Vertical(g21)
    c: Coincident(g22,g10)
    c: Coincident(g22,g6)
    c: Vertical(g22)
    c: Coincident(g23,g6)
    c: Coincident(g23,g10)
    c: Vertical(g23)
FEATURE [Part::Extrusion] Extrude039  label="removeToCreateFanGrillHoles002"
  Base = -> Sketch048
  Dir = (0,-1,6e-16)
  DirMode = 2
  FaceMakerClass = Part::FaceMakerBullseye
  LengthFwd = 10
  LengthRev = 0
  Placement = pos=(65.4,44,54.82) rot=(0,0,1;0rad)
  Solid = true
  Symmetric = false
FEATURE [Part::Cut] Cut027  label="fanScrewHousing004"
  Base = -> Cut026
  Tool = -> Extrude038
FEATURE [Part::Cut] Cut028  label="top014"
  Base = -> Fillet026
  Tool = -> Extrude039
FEATURE [Part::Feature] Face095 .. Face098  x4 (patterned run collapsed; names and placements below)
  shape: bbox 3.5 x 17.8 x 2e-07 mm, 1 faces, 0 solids (baked)
FEATURE [Part::Revolution] Revolve103  label="removeToCreateScrewAndThreadedInsertHole030"
  Angle = 360
  Axis = (0,1,0)
  Base = (0,0,0)
  FaceMakerClass = Part::FaceMakerBullseye
  Placement = pos=(62.3,30.3,19.7) rot=(0,0,1;0rad)
  Solid = false
  Source = -> Face095
  Symmetric = false
FEATURE [Part::Revolution] Revolve104  label="removeToCreateScrewAndThreadedInsertHole031"
  Angle = 360
  Axis = (0,1,0)
  Base = (0,0,0)
  FaceMakerClass = Part::FaceMakerBullseye
  Placement = pos=(62.3,30.3,51.7) rot=(0,0,1;0rad)
  Solid = false
  Source = -> Face096
  Symmetric = false
FEATURE [Part::Revolution] Revolve105  label="removeToCreateScrewAndThreadedInsertHole032"
  Angle = 360
  Axis = (0,1,0)
  Base = (0,0,0)
  FaceMakerClass = Part::FaceMakerBullseye
  Placement = pos=(30.3,30.3,19.7) rot=(0,0,1;0rad)
  Solid = false
  Source = -> Face097
  Symmetric = false
FEATURE [Part::Revolution] Revolve106  label="removeToCreateScrewAndThreadedInsertHole033"
  Angle = 360
  Axis = (0,1,0)
  Base = (0,0,0)
  FaceMakerClass = Part::FaceMakerBullseye
  Placement = pos=(30.3,30.3,51.7) rot=(0,0,1;0rad)
  Solid = false
  Source = -> Face098
  Symmetric = false
FEATURE [Part::MultiFuse] Fusion069  label="createThreadedInsertHolesForFan003"
  Shapes = -> [Revolve103,Revolve104,Revolve105,Revolve106]
FEATURE [Part::Cut] Cut029  label="top015"
  Base = -> Cut028
  Tool = -> Fusion054
FEATURE [Part::Cut] Cut030  label="fanScrewHousing005"
  Base = -> Cut027
  Tool = -> Fusion069
FEATURE [Part::Cylinder] Cylinder026  label="removeToCreteHoleForPlugHousing010"
  Angle = 360
  AttacherType = Attacher::AttachEngine3D
  Height = 20
  Placement = pos=(-2,19,36) rot=(0,1,0;1.5708rad)
  Radius = 14.3
FEATURE [Part::Box] Box018  label="removeToCreteHoleForPlugHousing011"
  AttacherType = Attacher::AttachEngine3D
  Height = 28.6
  Length = 10
  Placement = pos=(-2,0,21.7) rot=(0,0,1;0rad)
  Width = 19
FEATURE [Part::Box] Box019  label="wireHolderBottomCaseBit"
  AttacherType = Attacher::AttachEngine3D
  Height = 28
  Length = 3
  Placement = pos=(0,0,22) rot=(0,0,1;0rad)
  Width = 21
FEATURE [Part::Cylinder] Cylinder027  label="removeToCreteHoleForPlugHousing012"
  Angle = 360
  AttacherType = Attacher::AttachEngine3D
  Height = 20
  Placement = pos=(-2,19,36) rot=(0,1,0;1.5708rad)
  Radius = 14.3
FEATURE [Part::Cut] Cut031  label="wireHolderBottomCaseBit001"
  Base = -> Box019
  Tool = -> Cylinder027
FEATURE [Part::MultiFuse] Fusion070  label="removeToCreteHoleForPlugHousing013"
  Shapes = -> [Box018,Cylinder026]
FEATURE [Part::Cut] Cut032  label="top016"
  Base = -> Cut029
  Tool = -> Fusion070
FEATURE [Part::Cylinder] Cylinder028
  Angle = 360
  AttacherType = Attacher::AttachEngine3D
  Height = 20
  Placement = pos=(0,0,36.15) rot=(0,0,1;0rad)
  Radius = 14.3
FEATURE [Part::Cylinder] Cylinder029
  Angle = 360
  AttacherType = Attacher::AttachEngine3D
  Height = 10
  Placement = pos=(0,0,36.15) rot=(0,0,1;0rad)
  Radius = 4
FEATURE [Part::MultiFuse] Fusion071  label="removeToCreteHoleForPlugHousing014"
  Placement = pos=(70,19,36) rot=(0,1,0;1.5708rad)
  Shapes = -> [Cylinder028,Cylinder029]
FEATURE [Sketcher::SketchObject] Sketch049  label="topSketch011"
  FullyConstrained = true
  sketch-geometry (4):
    g0: ArcOfCircle CenterX=105 CenterY=19 CenterZ=0 NormalX=0 NormalY=0 NormalZ=1 AngleXU=0 Radius=20.6155 StartAngle=5.54125 EndAngle=6.28319
    g1: ArcOfCircle CenterX=105 CenterY=19 CenterZ=0 NormalX=0 NormalY=0 NormalZ=1 AngleXU=0 Radius=13 StartAngle=5.54125 EndAngle=6.28319
    g2: LineSegment StartX=118 StartY=19 StartZ=0 EndX=125.616 EndY=19 EndZ=0
    g3: LineSegment StartX=114.583 StartY=10.2157 StartZ=0 EndX=120.197 EndY=5.06982 EndZ=0
  constraints (7):
    c: Block(g0)
    c: Block(g1)
    c: Coincident(g2,g1)
    c: Coincident(g2,g0)
    c: Horizontal(g2)
    c: Coincident(g3,g1)
    c: Coincident(g3,g0)
FEATURE [Part::Box] Box020  label="removeToCreteHoleForPlugHousing015"
  AttacherType = Attacher::AttachEngine3D
  Height = 28.6
  Length = 20
  Placement = pos=(106.15,0,21.7) rot=(0,0,1;0rad)
  Width = 19
FEATURE [Part::MultiFuse] Fusion072  label="removeToCreteHoleForPlugHousing016"
  Shapes = -> [Box020,Fusion071]
FEATURE [Part::Cut] Cut033  label="removeToCreteHoleForPlugHousing017"
  Base = -> Cut032
  Tool = -> Fusion072
FEATURE [Part::Cylinder] Cylinder030
  Angle = 360
  AttacherType = Attacher::AttachEngine3D
  Height = 20
  Placement = pos=(0,0,36.15) rot=(0,0,1;0rad)
  Radius = 14.3
FEATURE [Part::Cylinder] Cylinder031
  Angle = 360
  AttacherType = Attacher::AttachEngine3D
  Height = 10
  Placement = pos=(0,0,36.15) rot=(0,0,1;0rad)
  Radius = 4
FEATURE [Part::Box] Box021  label="removeToCreteHoleForPlugHousing019"
  AttacherType = Attacher::AttachEngine3D
  Height = 28.6
  Length = 20
  Placement = pos=(106.15,0,21.7) rot=(0,0,1;0rad)
  Width = 19
FEATURE [Part::MultiFuse] Fusion074  label="removeToCreteHoleForPlugHousing020"
  Placement = pos=(70,19,36) rot=(0,1,0;1.5708rad)
  Shapes = -> [Cylinder030,Cylinder031]
FEATURE [Part::MultiFuse] Fusion073  label="removeToCreteHoleForPlugHousing018"
  Placement = pos=(0,0,28.3) rot=(0,0,1;0rad)
  Shapes = -> [Box021,Fusion074]
FEATURE [Part::Cylinder] Cylinder032
  Angle = 360
  AttacherType = Attacher::AttachEngine3D
  Height = 20
  Placement = pos=(0,0,36.15) rot=(0,0,1;0rad)
  Radius = 14.3
FEATURE [Part::Cylinder] Cylinder033
  Angle = 360
  AttacherType = Attacher::AttachEngine3D
  Height = 10
  Placement = pos=(0,0,36.15) rot=(0,0,1;0rad)
  Radius = 4
FEATURE [Part::Box] Box022  label="removeToCreteHoleForPlugHousing021"
  AttacherType = Attacher::AttachEngine3D
  Height = 28.6
  Length = 20
  Placement = pos=(106.15,0,21.7) rot=(0,0,1;0rad)
  Width = 19
FEATURE [Part::MultiFuse] Fusion076  label="removeToCreteHoleForPlugHousing023"
  Placement = pos=(70,19,36) rot=(0,1,0;1.5708rad)
  Shapes = -> [Cylinder032,Cylinder033]
FEATURE [Part::MultiFuse] Fusion075  label="removeToCreteHoleForPlugHousing022"
  Placement = pos=(0,0,-28.3) rot=(0,0,1;0rad)
  Shapes = -> [Box022,Fusion076]
FEATURE [Part::MultiFuse] Fusion077  label="removeToCreatePlugHousingBottomBit"
  Shapes = -> [Fusion075,Fusion073]
FEATURE [Part::Cylinder] Cylinder034
  Angle = 360
  AttacherType = Attacher::AttachEngine3D
  Height = 20
  Placement = pos=(0,0,36.15) rot=(0,0,1;0rad)
  Radius = 14
FEATURE [Part::Cylinder] Cylinder035
  Angle = 360
  AttacherType = Attacher::AttachEngine3D
  Height = 10
  Placement = pos=(0,0,36.15) rot=(0,0,1;0rad)
  Radius = 4
FEATURE [Part::MultiFuse] Fusion078  label="removeToCreteHoleForPlugHousing024"
  Placement = pos=(70,19,36) rot=(0,1,0;1.5708rad)
  Shapes = -> [Cylinder034,Cylinder035]
FEATURE [Part::MultiFuse] Fusion079  label="removeToCreatePlugHousingBottomBit001"
  Shapes = -> [Fusion078,Fusion077]
FEATURE [Part::Extrusion] Extrude040  label="bottomPlugHousingBit"
  Base = -> Sketch049
  Dir = (0,0,1)
  DirMode = 2
  FaceMakerClass = Part::FaceMakerBullseye
  LengthFwd = 72
  LengthRev = 0
  Solid = true
  Symmetric = false
FEATURE [Part::Cut] Cut034  label="bottomPlugHousingBit001"
  Base = -> Extrude040
  Placement = pos=(-0.09,0,0) rot=(0,0,1;0rad)
  Tool = -> Fusion079
FEATURE [Part::Box] Box023  label="Cube014"
  AttacherType = Attacher::AttachEngine3D
  Height = 16
  Length = 8
  Placement = pos=(12.7,31.52,28) rot=(0,0,1;0rad)
  Width = 4
FEATURE [Part::Cylinder] Cylinder036
  Angle = 360
  AttacherType = Attacher::AttachEngine3D
  Height = 10
  Placement = pos=(0,0,36.15) rot=(0,0,1;0rad)
  Radius = 4
FEATURE [Part::Cylinder] Cylinder037
  Angle = 360
  AttacherType = Attacher::AttachEngine3D
  Height = 20
  Placement = pos=(0,0,36.15) rot=(0,0,1;0rad)
  Radius = 8.2
FEATURE [Part::MultiFuse] Fusion080  label="removeToCreteHoleForPlugHousing025"
  Placement = pos=(-42,19,36) rot=(0,1,0;1.5708rad)
  Shapes = -> [Cylinder037,Cylinder036]
FEATURE [Sketcher::SketchObject] Sketch050  label="topSketch012"
  FullyConstrained = true
  sketch-geometry (4):
    g0: LineSegment StartX=16.8446 StartY=31.512 StartZ=0 EndX=16.3251 EndY=34.4666 EndZ=0
    g1: ArcOfCircle CenterX=19 CenterY=19.2524 CenterZ=0 NormalX=0 NormalY=0 NormalZ=1 AngleXU=0 Radius=15.4476 StartAngle=1.74483 EndAngle=2.72717
    g2: ArcOfCircle CenterX=19 CenterY=19.2524 CenterZ=0 NormalX=0 NormalY=0 NormalZ=1 AngleXU=0 Radius=12.4476 StartAngle=1.74483 EndAngle=2.73189
    g3: LineSegment StartX=4.86004 StartY=25.4725 StartZ=0 EndX=7.58253 EndY=24.2107 EndZ=0
  constraints (7):
    c: Block(g0)
    c: Coincident(g1,g0)
    c: Coincident(g2,g0)
    c: Coincident(g3,g1)
    c: Coincident(g3,g2)
    c: Block(g1)
    c: Block(g2)
FEATURE [Part::Extrusion] Extrude041
  Base = -> Sketch050
  Dir = (0,0,1)
  DirMode = 2
  FaceMakerClass = Part::FaceMakerBullseye
  LengthFwd = 10.6
  LengthRev = 0
  Placement = pos=(0,0,31) rot=(0,0,1;0rad)
  Solid = true
  Symmetric = false
FEATURE [Part::Cut] Cut035
  Base = -> Extrude041
  Placement = pos=(0,0,-0.3) rot=(0,0,1;0rad)
  Tool = -> Fusion080
FEATURE [Part::Cut] Cut036
  Base = -> Box023
  Tool = -> Cut035
FEATURE [Part::Fillet] Fillet027
  Base = -> Cut036
  Edges = 1 edges r=0.7: [Edge13]
FEATURE [Part::Fillet] Fillet028
  Base = -> Fillet027
  Edges = 1 edges r=0.7: [Edge13]
FEATURE [Part::Fillet] Fillet029
  Base = -> Fillet028
  Edges = 1 edges r=0.7: [Edge16]
FEATURE [Part::Fillet] Fillet030
  Base = -> Fillet029
  Edges = 1 edges r=0.7: [Edge11]
FEATURE [Part::Fillet] Fillet031
  Base = -> Fillet030
  Edges = 1 edges r=0.7: [Edge10]
FEATURE [Part::Fillet] Fillet032
  Base = -> Fillet031
  Edges = 1 edges r=1.2: [Edge5]
FEATURE [Part::Fillet] Fillet033
  Base = -> Fillet032
  Edges = 1 edges r=1.2: [Edge12]
FEATURE [Part::Fillet] Fillet034  label="wireHousingRetainer"
  Base = -> Fillet033
  Edges = 1 edges r=2: [Edge1]
  Placement = pos=(0.3,0,0) rot=(0,0,1;0rad)
FEATURE [Part::Feature] Face099
  shape: bbox 3.5 x 17.8 x 2e-07 mm, 1 faces, 0 solids (baked)
FEATURE [Part::Revolution] Revolve107  label="removeToCreateScrewAndThreadedInsertHole034"
  Angle = 360
  Axis = (0,1,0)
  Base = (0,0,0)
  FaceMakerClass = Part::FaceMakerBullseye
  Placement = pos=(12.5,0,10) rot=(0,0,1;0rad)
  Solid = false
  Source = -> Face099
  Symmetric = false
FEATURE [Part::Feature] Face100
  shape: bbox 3.5 x 17.8 x 2e-07 mm, 1 faces, 0 solids (baked)
FEATURE [Part::Revolution] Revolve108  label="removeToCreateScrewAndThreadedInsertHole035"
  Angle = 360
  Axis = (0,1,0)
  Base = (0,0,0)
  FaceMakerClass = Part::FaceMakerBullseye
  Placement = pos=(12.5,0,62) rot=(0,0,1;0rad)
  Solid = false
  Source = -> Face100
  Symmetric = false
FEATURE [Part::Feature] Face101
  shape: bbox 3.5 x 17.8 x 2e-07 mm, 1 faces, 0 solids (baked)
FEATURE [Part::Revolution] Revolve109  label="removeToCreateScrewAndThreadedInsertHole036"
  Angle = 360
  Axis = (0,1,0)
  Base = (0,0,0)
  FaceMakerClass = Part::FaceMakerBullseye
  Placement = pos=(89.5,0,68.5) rot=(0,0,1;0rad)
  Solid = false
  Source = -> Face101
  Symmetric = false
FEATURE [Part::Feature] Face102
  shape: bbox 3.5 x 17.8 x 2e-07 mm, 1 faces, 0 solids (baked)
FEATURE [Part::Revolution] Revolve110  label="removeToCreateScrewAndThreadedInsertHole037"
  Angle = 360
  Axis = (0,1,0)
  Base = (0,0,0)
  FaceMakerClass = Part::FaceMakerBullseye
  Placement = pos=(89.5,0,3.5) rot=(0,0,1;0rad)
  Solid = false
  Source = -> Face102
  Symmetric = false
FEATURE [Part::Feature] Face103
  shape: bbox 3.5 x 17.8 x 2e-07 mm, 1 faces, 0 solids (baked)
FEATURE [Part::Revolution] Revolve111  label="removeToCreateScrewAndThreadedInsertHole038"
  Angle = 360
  Axis = (0,1,0)
  Base = (0,0,0)
  FaceMakerClass = Part::FaceMakerBullseye
  Placement = pos=(109.5,4.7,3.5) rot=(0,0,1;0rad)
  Solid = false
  Source = -> Face103
  Symmetric = false
FEATURE [Part::Feature] Face104
  shape: bbox 3.5 x 17.8 x 2e-07 mm, 1 faces, 0 solids (baked)
FEATURE [Part::Revolution] Revolve112  label="removeToCreateScrewAndThreadedInsertHole039"
  Angle = 360
  Axis = (0,1,0)
  Base = (0,0,0)
  FaceMakerClass = Part::FaceMakerBullseye
  Placement = pos=(109.5,4.7,68.5) rot=(0,0,1;0rad)
  Solid = false
  Source = -> Face104
  Symmetric = false
FEATURE [Part::MultiFuse] Fusion081  label="removeToCreateScrewAndThreadedInsertHole040"
  Shapes = -> [Revolve107,Revolve108,Revolve109,Revolve110,Revolve111,Revolve112]
FEATURE [Part::MultiFuse] Fusion082  label="casePillars002"
  Shapes = -> [Revolve094,Revolve092,Revolve090,Revolve089,Revolve091,Revolve093]
FEATURE [Part::Cut] Cut037  label="casePillars003"
  Base = -> Fusion082
  Tool = -> Fusion081
FEATURE [Sketcher::SketchObject] Sketch051
  FullyConstrained = true
  Placement = pos=(117,19,0) rot=(0.57735,0.57735,0.57735;2.0944rad)
  sketch-geometry (48):
    g0: LineSegment StartX=-49.19 StartY=69.25 StartZ=0 EndX=-49.19 EndY=66.25 EndZ=0
    g1: LineSegment StartX=-49.19 StartY=63.5 StartZ=0 EndX=-49.19 EndY=60.5 EndZ=0
    g2: LineSegment StartX=-49.19 StartY=57.75 StartZ=0 EndX=-49.19 EndY=54.75 EndZ=0
    g3: LineSegment StartX=-49.19 StartY=52 StartZ=0 EndX=-49.19 EndY=49 EndZ=0
    g4: LineSegment StartX=-49.19 StartY=46.25 StartZ=0 EndX=-49.19 EndY=43.25 EndZ=0
    g5: LineSegment StartX=-49.19 StartY=40.5 StartZ=0 EndX=-49.19 EndY=37.5 EndZ=0
    g6: LineSegment StartX=-49.19 StartY=34.5 StartZ=0 EndX=-49.19 EndY=31.5 EndZ=0
    g7: LineSegment StartX=-49.19 StartY=28.75 StartZ=0 EndX=-49.19 EndY=25.75 EndZ=0
    g8: LineSegment StartX=-49.19 StartY=23 StartZ=0 EndX=-49.19 EndY=20 EndZ=0
    g9: LineSegment StartX=-49.19 StartY=17.25 StartZ=0 EndX=-49.19 EndY=14.25 EndZ=0
    g10: LineSegment StartX=-49.19 StartY=11.5 StartZ=0 EndX=-49.19 EndY=8.5 EndZ=0
    g11: LineSegment StartX=-49.19 StartY=5.75 StartZ=0 EndX=-49.19 EndY=2.75 EndZ=0
    g12: ArcOfCircle CenterX=-1.5 CenterY=67.75 CenterZ=0 NormalX=0 NormalY=0 NormalZ=1 AngleXU=0 Radius=1.5 StartAngle=4.71239 EndAngle=7.85398
    g13: ArcOfCircle CenterX=-1.5 CenterY=62 CenterZ=0 NormalX=0 NormalY=0 NormalZ=1 AngleXU=0 Radius=1.5 StartAngle=4.71239 EndAngle=7.85398
    g14: ArcOfCircle CenterX=-1.5 CenterY=56.25 CenterZ=0 NormalX=0 NormalY=0 NormalZ=1 AngleXU=0 Radius=1.5 StartAngle=4.71239 EndAngle=7.85398
    g15: ArcOfCircle CenterX=-11.49 CenterY=50.5 CenterZ=0 NormalX=0 NormalY=0 NormalZ=1 AngleXU=0 Radius=1.5 StartAngle=4.71239 EndAngle=7.85398
    g16: ArcOfCircle CenterX=-16.28 CenterY=44.75 CenterZ=0 NormalX=0 NormalY=0 NormalZ=1 AngleXU=0 Radius=1.5 StartAngle=4.71239 EndAngle=7.85398
    g17: ArcOfCircle CenterX=-18.2337 CenterY=39 CenterZ=0 NormalX=0 NormalY=0 NormalZ=1 AngleXU=0 Radius=1.5 StartAngle=4.71485 EndAngle=7.85398
    g18: ArcOfCircle CenterX=-16.2837 CenterY=27.25 CenterZ=0 NormalX=0 NormalY=0 NormalZ=1 AngleXU=0 Radius=1.5 StartAngle=4.71485 EndAngle=7.85398
    g19: ArcOfCircle CenterX=-18.2337 CenterY=33 CenterZ=0 NormalX=0 NormalY=0 NormalZ=1 AngleXU=0 Radius=1.5 StartAngle=4.71485 EndAngle=7.85398
    g20: ArcOfCircle CenterX=-11.49 CenterY=21.5 CenterZ=0 NormalX=0 NormalY=0 NormalZ=1 AngleXU=0 Radius=1.5 StartAngle=4.71239 EndAngle=7.85398
    g21: ArcOfCircle CenterX=-1.5 CenterY=4.25 CenterZ=0 NormalX=0 NormalY=0 NormalZ=1 AngleXU=0 Radius=1.5 StartAngle=4.71239 EndAngle=7.85398
    g22: ArcOfCircle CenterX=-1.5 CenterY=10 CenterZ=0 NormalX=0 NormalY=0 NormalZ=1 AngleXU=0 Radius=1.5 StartAngle=4.71239 EndAngle=7.85398
    g23: ArcOfCircle CenterX=-1.5 CenterY=15.75 CenterZ=0 NormalX=0 NormalY=0 NormalZ=1 AngleXU=0 Radius=1.5 StartAngle=4.71239 EndAngle=7.85398
    g24: LineSegment StartX=-49.19 StartY=69.25 StartZ=0 EndX=-1.5 EndY=69.25 EndZ=0
    g25: LineSegment StartX=-49.19 StartY=66.25 StartZ=0 EndX=-1.5 EndY=66.25 EndZ=0
    g26: LineSegment StartX=-49.19 StartY=63.5 StartZ=0 EndX=-1.5 EndY=63.5 EndZ=0
    g27: LineSegment StartX=-49.19 StartY=60.5 StartZ=0 EndX=-1.5 EndY=60.5 EndZ=0
    g28: LineSegment StartX=-49.19 StartY=57.75 StartZ=0 EndX=-1.5 EndY=57.75 EndZ=0
    g29: LineSegment StartX=-49.19 StartY=54.75 StartZ=0 EndX=-1.5 EndY=54.75 EndZ=0
    g30: LineSegment StartX=-49.19 StartY=52 StartZ=0 EndX=-11.49 EndY=52 EndZ=0
    g31: LineSegment StartX=-49.19 StartY=49 StartZ=0 EndX=-11.49 EndY=49 EndZ=0
    g32: LineSegment StartX=-49.19 StartY=46.25 StartZ=0 EndX=-16.28 EndY=46.25 EndZ=0
    g33: LineSegment StartX=-49.19 StartY=43.25 StartZ=0 EndX=-16.28 EndY=43.25 EndZ=0
    g34: LineSegment StartX=-49.19 StartY=40.5 StartZ=0 EndX=-18.2337 EndY=40.5 EndZ=0
    g35: LineSegment StartX=-49.19 StartY=37.5 StartZ=0 EndX=-18.23 EndY=37.5 EndZ=0
    g36: LineSegment StartX=-49.19 StartY=34.5 StartZ=0 EndX=-18.2337 EndY=34.5 EndZ=0
    g37: LineSegment StartX=-49.19 StartY=31.5 StartZ=0 EndX=-18.23 EndY=31.5 EndZ=0
    g38: LineSegment StartX=-49.19 StartY=28.75 StartZ=0 EndX=-16.2837 EndY=28.75 EndZ=0
    g39: LineSegment StartX=-49.19 StartY=25.75 StartZ=0 EndX=-16.28 EndY=25.75 EndZ=0
    g40: LineSegment StartX=-49.19 StartY=23 StartZ=0 EndX=-11.49 EndY=23 EndZ=0
    g41: LineSegment StartX=-49.19 StartY=20 StartZ=0 EndX=-11.49 EndY=20 EndZ=0
    g42: LineSegment StartX=-49.19 StartY=17.25 StartZ=0 EndX=-1.5 EndY=17.25 EndZ=0
    g43: LineSegment StartX=-49.19 StartY=14.25 StartZ=0 EndX=-1.5 EndY=14.25 EndZ=0
    g44: LineSegment StartX=-49.19 StartY=11.5 StartZ=0 EndX=-1.5 EndY=11.5 EndZ=0
    g45: LineSegment StartX=-49.19 StartY=8.5 StartZ=0 EndX=-1.5 EndY=8.5 EndZ=0
    g46: LineSegment StartX=-49.19 StartY=5.75 StartZ=0 EndX=-1.5 EndY=5.75 EndZ=0
    g47: LineSegment StartX=-49.19 StartY=2.75 StartZ=0 EndX=-1.5 EndY=2.75 EndZ=0
  constraints (120):
    c: Vertical(g0)
    c: Distance(g0) = 3
    c: Block(g0)
    c: Vertical(g1)
    c: Distance(g1) = 3
    c: Vertical(g2)
    c: Equal(g0,g2) = 3
    c: Block(g2)
    c: Vertical(g3)
    c: Equal(g1,g3) = 3
    c: Vertical(g4)
    c: Equal(g0,g4) = 3
    c: Block(g4)
    c: Vertical(g5)
    c: Equal(g1,g5) = 3
    c: Vertical(g6)
    c: Equal(g0,g6) = 3
    c: Block(g6)
    c: Vertical(g7)
    c: Equal(g1,g7) = 3
    c: Vertical(g8)
    c: Equal(g0,g8) = 3
    c: Block(g8)
    c: Vertical(g9)
    c: Equal(g1,g9) = 3
    c: Vertical(g10)
    c: Equal(g0,g10) = 3
    c: Block(g10)
    c: Vertical(g11)
    c: Equal(g1,g11) = 3
    c: Block(g12)
    c: Block(g13)
    c: Block(g14)
    c: Block(g15)
    c: Block(g16)
    c: Block(g17)
    c: Block(g18)
    c: Block(g19)
    c: Block(g20)
    c: Block(g21)
    c: Block(g22)
    c: Block(g23)
    c: Block(g11)
    c: Block(g9)
    c: Block(g7)
    c: Block(g5)
    c: Block(g3)
    c: Block(g1)
    c: Coincident(g24,g0)
    c: Coincident(g24,g12)
    c: Horizontal(g24)
    c: Coincident(g25,g0)
    c: Coincident(g25,g12)
    c: Horizontal(g25)
    c: Coincident(g26,g1)
    c: Coincident(g26,g13)
    c: Horizontal(g26)
    c: Coincident(g27,g1)
    c: Coincident(g27,g13)
    c: Horizontal(g27)
    c: Coincident(g28,g2)
    c: Coincident(g28,g14)
    c: Horizontal(g28)
    c: Coincident(g29,g2)
    c: Coincident(g29,g14)
    c: Horizontal(g29)
    c: Coincident(g30,g3)
    c: Coincident(g30,g15)
    c: Horizontal(g30)
    c: Coincident(g31,g3)
    c: Coincident(g31,g15)
    c: Horizontal(g31)
    c: Coincident(g32,g4)
    c: Coincident(g32,g16)
    c: Horizontal(g32)
    c: Coincident(g33,g4)
    c: Coincident(g33,g16)
    c: Horizontal(g33)
    c: Coincident(g34,g5)
    c: Coincident(g34,g17)
    c: Horizontal(g34)
    c: Coincident(g35,g5)
    c: Coincident(g35,g17)
    c: Horizontal(g35)
    c: Coincident(g36,g6)
    c: Coincident(g36,g19)
    c: Horizontal(g36)
    c: Coincident(g37,g6)
    c: Coincident(g37,g19)
    c: Horizontal(g37)
    c: Coincident(g38,g7)
    c: Coincident(g38,g18)
    c: Horizontal(g38)
    c: Coincident(g39,g7)
    c: Coincident(g39,g18)
    c: Horizontal(g39)
    c: Coincident(g40,g8)
    c: Coincident(g40,g20)
    c: Horizontal(g40)
    c: Coincident(g41,g8)
    c: Coincident(g41,g20)
    c: Horizontal(g41)
    c: Coincident(g42,g9)
    c: Coincident(g42,g23)
    c: Horizontal(g42)
    c: Coincident(g43,g9)
    c: Coincident(g43,g23)
    c: Horizontal(g43)
    c: Coincident(g44,g10)
    c: Coincident(g44,g22)
    c: Horizontal(g44)
    c: Coincident(g45,g10)
    c: Coincident(g45,g22)
    c: Horizontal(g45)
    c: Coincident(g46,g11)
    c: Coincident(g46,g21)
    c: Horizontal(g46)
    c: Coincident(g47,g11)
    c: Coincident(g47,g21)
    c: Horizontal(g47)
FEATURE [Part::Extrusion] Extrude042
  Base = -> Sketch051
  Dir = (1,-2e-16,2e-16)
  DirMode = 2
  FaceMakerClass = Part::FaceMakerBullseye
  LengthFwd = 19
  LengthRev = 0
  Placement = pos=(-19,0,0) rot=(0,0,1;0rad)
  Solid = true
  Symmetric = false
FEATURE [Part::Fillet] Fillet035  label="removeToCreateVentalationHoles"
  Base = -> Extrude042
  Edges = <same value as first occurrence — deduplicated (x4 in doc)>
  Placement = pos=(7,0,0) rot=(0,0,1;0rad)
FEATURE [Part::Cut] Cut038  label="top017"
  Base = -> Cut033
  Tool = -> Fillet035
FEATURE [Sketcher::SketchObject] Sketch052  label="bottomSketch001"
  FullyConstrained = true
  sketch-geometry (45):
    g0: LineSegment StartX=6.29999 StartY=8 StartZ=0 EndX=3.29999 EndY=8 EndZ=0
    g1: LineSegment StartX=3.29999 StartY=8 StartZ=0 EndX=3.29999 EndY=-6.03275e-07 EndZ=0
    g2: ArcOfCircle CenterX=8.29999 CenterY=5 CenterZ=0 NormalX=0 NormalY=0 NormalZ=1 AngleXU=0 Radius=2 StartAngle=3.14159 EndAngle=4.71239
    g3: LineSegment StartX=6.29999 StartY=8 StartZ=0 EndX=6.29999 EndY=5 EndZ=0
    g4: ArcOfCircle CenterX=105 CenterY=19 CenterZ=0 NormalX=0 NormalY=0 NormalZ=1 AngleXU=0 Radius=12.7 StartAngle=4.71239 EndAngle=5.94289
    g5-g11: Circle x7 (B-spline internal-alignment scaffolding for g12; pole/knot coordinates omitted)
    g12: BSplineCurve PolesCount=7 KnotsCount=5 Degree=3 IsPeriodic=0
    g13-g17: GeomPoint x5 (B-spline internal-alignment scaffolding for g12; pole/knot coordinates omitted)
    g18: ArcOfCircle CenterX=105 CenterY=19 CenterZ=0 NormalX=0 NormalY=0 NormalZ=1 AngleXU=0 Radius=15.7 StartAngle=5.81226 EndAngle=6.28319
    g19: BSplineCurve PolesCount=5 KnotsCount=3 Degree=3 IsPeriodic=0
    g20: LineSegment StartX=8.29999 StartY=3 StartZ=0 EndX=101.7 EndY=3 EndZ=0
    g21: LineSegment StartX=3.29999 StartY=-6.03275e-07 StartZ=0 EndX=105 EndY=-6.03275e-07 EndZ=0
    g22: LineSegment StartX=120.974 StartY=8.71251 StartZ=0 EndX=122.332 EndY=7.83778 EndZ=0
    g23: LineSegment StartX=105 StartY=-6.03274e-07 StartZ=0 EndX=113 EndY=-6.03274e-07 EndZ=0
    g24: ArcOfCircle CenterX=105 CenterY=19 CenterZ=0 NormalX=0 NormalY=0 NormalZ=1 AngleXU=0 Radius=20.6155 StartAngle=5.11091 EndAngle=5.71103
    g25: ArcOfCircle CenterX=117.7 CenterY=19 CenterZ=0 NormalX=0 NormalY=0 NormalZ=1 AngleXU=0 Radius=3 StartAngle=1.2e-15 EndAngle=2.10468
    g26: Circle CenterX=116.345 CenterY=16.3232 CenterZ=0 NormalX=0 NormalY=0 NormalZ=1 AngleXU=0 Radius=1
    g27: Circle CenterX=117.24 CenterY=15.7584 CenterZ=0 NormalX=0 NormalY=0 NormalZ=1 AngleXU=0 Radius=1
    g28: Circle CenterX=116.972 CenterY=14.7612 CenterZ=0 NormalX=0 NormalY=0 NormalZ=1 AngleXU=0 Radius=1
    g29: BSplineCurve PolesCount=3 KnotsCount=2 Degree=2 IsPeriodic=0
    g30: GeomPoint X=116.345 Y=16.3232 Z=0
    g31: GeomPoint X=116.972 Y=14.7612 Z=0
    g32: Circle CenterX=115.828 CenterY=17.157 CenterZ=0 NormalX=0 NormalY=0 NormalZ=1 AngleXU=0 Radius=1
    g33: Circle CenterX=115.841 CenterY=16.639 CenterZ=0 NormalX=0 NormalY=0 NormalZ=1 AngleXU=0 Radius=1
    g34: Circle CenterX=116.345 CenterY=16.3232 CenterZ=0 NormalX=0 NormalY=0 NormalZ=1 AngleXU=0 Radius=1
    g35: BSplineCurve PolesCount=3 KnotsCount=2 Degree=2 IsPeriodic=0
    g36: GeomPoint X=115.828 Y=17.157 Z=0
    g37: GeomPoint X=116.345 Y=16.3232 Z=0
    g38: LineSegment StartX=115.828 StartY=17.157 StartZ=0 EndX=115.828 EndY=20.8307 EndZ=0
    g39: Circle CenterX=115.828 CenterY=20.8307 CenterZ=0 NormalX=0 NormalY=0 NormalZ=1 AngleXU=0 Radius=1
    g40: Circle CenterX=115.831 CenterY=21.3396 CenterZ=0 NormalX=0 NormalY=0 NormalZ=1 AngleXU=0 Radius=1
    g41: Circle CenterX=116.173 CenterY=21.5825 CenterZ=0 NormalX=0 NormalY=0 NormalZ=1 AngleXU=0 Radius=1
    g42: BSplineCurve PolesCount=3 KnotsCount=2 Degree=2 IsPeriodic=0
    g43: GeomPoint X=115.828 Y=20.8307 Z=0
    g44: GeomPoint X=116.173 Y=21.5825 Z=0
  constraints (70):
    c: Horizontal(g0)
    c: Distance(g0) = 3
    c: Coincident(g1,g0)
    c: Vertical(g1)
    c: Block(g2)
    c: Block(g0)
    c: Coincident(g3,g0)
    c: Coincident(g3,g2)
    c: Vertical(g3)
    c: Block(g1)
    c: Block(g4)
    c: Coincident(g19,g4)
    c: Block(g19)
    c: Equal(g5, g6-g11) x6
    c: InternalAlignment(g5-g11 -> g12) x7
    c: InternalAlignment(g13-g17 -> g12) x5
    c: Block(g12)
    c: Coincident(g18,g12)
    c: Block(g18)
    c: Coincident(g20,g2)
    c: Coincident(g20,g19)
    c: Horizontal(g20)
    c: Distance(g20) = 93.4
    c: Coincident(g21,g1)
    c: Horizontal(g21)
    c: Distance(g21) = 101.7
    c: Horizontal(g23)
    c: Distance(g23) = 8
    c: Coincident(g24,g23)
    c: Block(g23)
    c: Coincident(g22,g24)
    c: Block(g24)
    c: Block(g22)
    c: Distance(g22) = 1.61553
    c: Coincident(g25,g18)
    c: Block(g25)
    c: Weight(g26) = 1
    c: Equal(g26,g27)
    c: Equal(g26,g28)
    c: Coincident(g29,g4)
    c: InternalAlignment(g26,g29)
    c: InternalAlignment(g27,g29)
    c: InternalAlignment(g28,g29)
    c: InternalAlignment(g30,g29)
    c: InternalAlignment(g31,g29)
    c: Block(g29)
    c: Weight(g32) = 1
    c: Equal(g32,g33)
    c: Equal(g32,g34)
    c: Coincident(g35,g29)
    c: InternalAlignment(g32,g35)
    c: InternalAlignment(g33,g35)
    c: InternalAlignment(g34,g35)
    c: InternalAlignment(g36,g35)
    c: InternalAlignment(g37,g35)
    c: Block(g35)
    c: Coincident(g38,g35)
    c: Vertical(g38)
    c: Block(g38)
    c: Coincident(g42,g38)
    c: Weight(g39) = 1
    c: Equal(g39,g40)
    c: Equal(g39,g41)
    c: Coincident(g42,g25)
    c: InternalAlignment(g39,g42)
    c: InternalAlignment(g40,g42)
    c: InternalAlignment(g41,g42)
    c: InternalAlignment(g43,g42)
    c: InternalAlignment(g44,g42)
    c: Block(g42)
FEATURE [Part::Extrusion] Extrude043  label="bottom010"
  Base = -> Sketch052
  Dir = (0,0,1)
  DirMode = 2
  FaceMakerClass = Part::FaceMakerBullseye
  LengthFwd = 71.4
  LengthRev = 0
  Placement = pos=(0,0,0.3) rot=(0,0,1;0rad)
  Solid = true
  Symmetric = false
FEATURE [Sketcher::SketchObject] Sketch053  label="topSketch013"
  FullyConstrained = true
  sketch-geometry (22):
    g0: LineSegment StartX=5.21097e-06 StartY=3 StartZ=0 EndX=5.21097e-06 EndY=19 EndZ=0
    g1: ArcOfCircle CenterX=19 CenterY=19 CenterZ=0 NormalX=0 NormalY=0 NormalZ=1 AngleXU=0 Radius=19 StartAngle=1.5708 EndAngle=3.14159
    g2: ArcOfCircle CenterX=19 CenterY=19 CenterZ=0 NormalX=0 NormalY=0 NormalZ=1 AngleXU=0 Radius=16 StartAngle=1.5708 EndAngle=3.14159
    g3: LineSegment StartX=114 StartY=35 StartZ=0 EndX=19 EndY=35 EndZ=0
    g4: LineSegment StartX=5.21097e-06 StartY=3 StartZ=0 EndX=5.21097e-06 EndY=0 EndZ=0
    g5: LineSegment StartX=3 StartY=0 StartZ=0 EndX=5.21097e-06 EndY=0 EndZ=0
    g6: LineSegment StartX=3 StartY=19 StartZ=0 EndX=3 EndY=0 EndZ=0
    g7: LineSegment StartX=19 StartY=38 StartZ=0 EndX=124 EndY=38 EndZ=0
    g8: Circle CenterX=119 CenterY=35 CenterZ=0 NormalX=0 NormalY=0 NormalZ=1 AngleXU=0 Radius=1
    g9: Circle CenterX=121 CenterY=35 CenterZ=0 NormalX=0 NormalY=0 NormalZ=1 AngleXU=0 Radius=1
    g10: Circle CenterX=121 CenterY=33 CenterZ=0 NormalX=0 NormalY=0 NormalZ=1 AngleXU=0 Radius=1
    g11: BSplineCurve PolesCount=3 KnotsCount=2 Degree=2 IsPeriodic=0
    g12: GeomPoint X=119 Y=35 Z=0
    g13: GeomPoint X=121 Y=33 Z=0
    g14: LineSegment StartX=119 StartY=35 StartZ=0 EndX=114 EndY=35 EndZ=0
    g15: ArcOfCircle CenterX=105 CenterY=19 CenterZ=0 NormalX=0 NormalY=0 NormalZ=1 AngleXU=0 Radius=16 StartAngle=5.60905 EndAngle=6.28319
    g16: LineSegment StartX=121 StartY=33 StartZ=0 EndX=121 EndY=19 EndZ=0
    g17: LineSegment StartX=117.5 StartY=9.01251 StartZ=0 EndX=121.163 EndY=9.0125 EndZ=0
    g18: ArcOfCircle CenterX=105 CenterY=19 CenterZ=0 NormalX=0 NormalY=0 NormalZ=1 AngleXU=0 Radius=20.6155 StartAngle=5.7297 EndAngle=6.28319
    g19: LineSegment StartX=121.163 StartY=9.0125 StartZ=0 EndX=122.538 EndY=8.16329 EndZ=0
    g20: LineSegment StartX=124 StartY=38 StartZ=0 EndX=125.616 EndY=38 EndZ=0
    g21: LineSegment StartX=125.616 StartY=19 StartZ=0 EndX=125.616 EndY=38 EndZ=0
  constraints (50):
    c: Vertical(g0)
    c: Block(g0)
    c: Coincident(g1,g0)
    c: Block(g1)
    c: Coincident(g2,g1)
    c: Block(g2)
    c: Coincident(g3,g2)
    c: Horizontal(g3)
    c: Tangent(g3,g2)
    c: Coincident(g4,g0)
    c: Distance(g4) = 3
    c: Vertical(g4)
    c: Coincident(g5,g4)
    c: Horizontal(g5)
    c: Coincident(g6,g2)
    c: Coincident(g6,g5)
    c: Vertical(g6)
    c: Horizontal(g7)
    c: Distance(g7) = 105
    c: Coincident(g7,g1)
    c: Block(g3)
    c: Weight(g8) = 1
    c: Equal(g8,g9)
    c: Equal(g8,g10)
    c: InternalAlignment(g8,g11)
    c: InternalAlignment(g9,g11)
    c: InternalAlignment(g10,g11)
    c: InternalAlignment(g12,g11)
    c: InternalAlignment(g13,g11)
    c: Block(g11)
    c: Coincident(g14,g11)
    c: Coincident(g14,g3)
    c: Horizontal(g14)
    c: Block(g15)
    c: Coincident(g16,g11)
    c: Coincident(g16,g15)
    c: Vertical(g16)
    c: Distance(g16) = 14
    c: Coincident(g17,g15)
    c: Block(g18)
    c: Coincident(g19,g18)
    c: Coincident(g20,g7)
    c: Horizontal(g20)
    c: Vertical(g21)
    c: Coincident(g20,g21)
    c: Block(g20)
    c: Block(g21)
    c: Block(g19)
    c: Block(g17)
    c: Distance(g20) = 1.61553
FEATURE [Part::Extrusion] Extrude044
  Base = -> Sketch053
  Dir = (0,0,1)
  DirMode = 2
  FaceMakerClass = Part::FaceMakerBullseye
  LengthFwd = 72
  LengthRev = 0
  Solid = true
  Symmetric = false
FEATURE [Part::Fillet] Fillet036  label="top018"
  Base = -> Extrude044
  Edges = 1 edges r=2: [Edge41]
FEATURE [Sketcher::SketchObject] Sketch054
  FullyConstrained = false
  Placement = pos=(0,0,0) rot=(1,0,0;1.5708rad)
  sketch-geometry (24):
    g0: ArcOfCircle CenterX=-4 CenterY=-10.5 CenterZ=0 NormalX=0 NormalY=0 NormalZ=1 AngleXU=0 Radius=1.5 StartAngle=6e-16 EndAngle=3.14159
    g1: ArcOfCircle CenterX=-34.2 CenterY=-10.5 CenterZ=0 NormalX=0 NormalY=0 NormalZ=1 AngleXU=0 Radius=1.5 StartAngle=0 EndAngle=3.14159
    g2: ArcOfCircle CenterX=-34.2 CenterY=-27.7 CenterZ=0 NormalX=0 NormalY=0 NormalZ=1 AngleXU=0 Radius=1.5 StartAngle=3.14159 EndAngle=6.28319
    g3: ArcOfCircle CenterX=-4 CenterY=-27.7 CenterZ=0 NormalX=0 NormalY=0 NormalZ=1 AngleXU=0 Radius=1.5 StartAngle=3.1416 EndAngle=6.28319
    g4: ArcOfCircle CenterX=-10 CenterY=-4.3 CenterZ=0 NormalX=0 NormalY=0 NormalZ=1 AngleXU=0 Radius=1.5 StartAngle=2e-16 EndAngle=3.14159
    g5: ArcOfCircle CenterX=-16.1 CenterY=-1.8 CenterZ=0 NormalX=0 NormalY=0 NormalZ=1 AngleXU=0 Radius=1.5 StartAngle=5e-16 EndAngle=3.14159
    g6: ArcOfCircle CenterX=-22.1 CenterY=-1.8 CenterZ=0 NormalX=0 NormalY=0 NormalZ=1 AngleXU=0 Radius=1.5 StartAngle=5e-16 EndAngle=3.14159
    g7: ArcOfCircle CenterX=-28.2 CenterY=-4.3 CenterZ=0 NormalX=0 NormalY=0 NormalZ=1 AngleXU=0 Radius=1.5 StartAngle=2e-16 EndAngle=3.14159
    g8: ArcOfCircle CenterX=-10 CenterY=-33.9 CenterZ=0 NormalX=0 NormalY=0 NormalZ=1 AngleXU=0 Radius=1.5 StartAngle=3.14159 EndAngle=6.28319
    g9: ArcOfCircle CenterX=-16.1 CenterY=-36.4 CenterZ=0 NormalX=0 NormalY=0 NormalZ=1 AngleXU=0 Radius=1.5 StartAngle=3.14159 EndAngle=6.28319
    g10: ArcOfCircle CenterX=-22.1 CenterY=-36.4 CenterZ=0 NormalX=0 NormalY=0 NormalZ=1 AngleXU=0 Radius=1.5 StartAngle=3.14159 EndAngle=6.28319
    g11: ArcOfCircle CenterX=-28.2 CenterY=-33.9 CenterZ=0 NormalX=0 NormalY=0 NormalZ=1 AngleXU=0 Radius=1.5 StartAngle=3.14159 EndAngle=6.28319
    g12: LineSegment StartX=-35.7 StartY=-10.5 StartZ=0 EndX=-35.7 EndY=-27.7 EndZ=0
    g13: LineSegment StartX=-32.7 StartY=-10.5 StartZ=0 EndX=-32.7 EndY=-27.7 EndZ=0
    g14: LineSegment StartX=-29.7 StartY=-33.9 StartZ=0 EndX=-29.7 EndY=-4.3 EndZ=0
    g15: LineSegment StartX=-26.7 StartY=-33.9 StartZ=0 EndX=-26.7 EndY=-4.3 EndZ=0
    g16: LineSegment StartX=-2.5 StartY=-10.5 StartZ=0 EndX=-2.5 EndY=-27.7 EndZ=0
    g17: LineSegment StartX=-8.5 StartY=-4.3 StartZ=0 EndX=-8.5 EndY=-33.9 EndZ=0
    g18: LineSegment StartX=-5.5 StartY=-10.5 StartZ=0 EndX=-5.5 EndY=-27.7 EndZ=0
    g19: LineSegment StartX=-11.5 StartY=-4.3 StartZ=0 EndX=-11.5 EndY=-33.9 EndZ=0
    g20: LineSegment StartX=-14.6 StartY=-1.8 StartZ=0 EndX=-14.6 EndY=-36.4 EndZ=0
    g21: LineSegment StartX=-17.6 StartY=-1.8 StartZ=0 EndX=-17.6 EndY=-36.4 EndZ=0
    g22: LineSegment StartX=-20.6 StartY=-36.4 StartZ=0 EndX=-20.6 EndY=-1.8 EndZ=0
    g23: LineSegment StartX=-23.6 StartY=-1.8 StartZ=0 EndX=-23.6 EndY=-36.4 EndZ=0
  constraints (48):
    c: Block(g0)
    c: Block(g1)
    c: Block(g2)
    c: Block(g3)
    c: Block(g4)
    c: Block(g5)
    c: Block(g6)
    c: Block(g7)
    c: Block(g8)
    c: Block(g9)
    c: Block(g10)
    c: Block(g11)
    c: Coincident(g12,g1)
    c: Coincident(g12,g2)
    c: Vertical(g12)
    c: Coincident(g13,g1)
    c: Coincident(g13,g2)
    c: Vertical(g13)
    c: Coincident(g14,g11)
    c: Coincident(g14,g7)
    c: Vertical(g14)
    c: Coincident(g15,g11)
    c: Coincident(g15,g7)
    c: Vertical(g15)
    c: Coincident(g16,g0)
    c: Coincident(g16,g3)
    c: Vertical(g16)
    c: Coincident(g17,g4)
    c: Coincident(g17,g8)
    c: Vertical(g17)
    c: Coincident(g18,g0)
    c: Coincident(g18,g3)
    c: Vertical(g18)
    c: Coincident(g19,g4)
    c: Coincident(g19,g8)
    c: Vertical(g19)
    c: Coincident(g20,g5)
    c: Coincident(g20,g9)
    c: Vertical(g20)
    c: Coincident(g21,g5)
    c: Coincident(g21,g9)
    c: Vertical(g21)
    c: Coincident(g22,g10)
    c: Coincident(g22,g6)
    c: Vertical(g22)
    c: Coincident(g23,g6)
    c: Coincident(g23,g10)
    c: Vertical(g23)
FEATURE [Part::Extrusion] Extrude045  label="removeToCreateFanGrillHoles003"
  Base = -> Sketch054
  Dir = (0,-1,6e-16)
  DirMode = 2
  FaceMakerClass = Part::FaceMakerBullseye
  LengthFwd = 10
  LengthRev = 0
  Placement = pos=(65.4,44,54.82) rot=(0,0,1;0rad)
  Solid = true
  Symmetric = false
FEATURE [Part::Feature] Face105 .. Face108  x4 (patterned run collapsed; names and placements below)
  shape: bbox 3.5 x 17.8 x 2e-07 mm, 1 faces, 0 solids (baked)
FEATURE [Part::Revolution] Revolve113  label="removeToCreateScrewAndThreadedInsertHole041"
  Angle = 360
  Axis = (0,1,0)
  Base = (0,0,0)
  FaceMakerClass = Part::FaceMakerBullseye
  Placement = pos=(62.3,30.3,19.7) rot=(0,0,1;0rad)
  Solid = false
  Source = -> Face105
  Symmetric = false
FEATURE [Part::Revolution] Revolve114  label="removeToCreateScrewAndThreadedInsertHole042"
  Angle = 360
  Axis = (0,1,0)
  Base = (0,0,0)
  FaceMakerClass = Part::FaceMakerBullseye
  Placement = pos=(62.3,30.3,51.7) rot=(0,0,1;0rad)
  Solid = false
  Source = -> Face106
  Symmetric = false
FEATURE [Part::Revolution] Revolve115  label="removeToCreateScrewAndThreadedInsertHole043"
  Angle = 360
  Axis = (0,1,0)
  Base = (0,0,0)
  FaceMakerClass = Part::FaceMakerBullseye
  Placement = pos=(30.3,30.3,19.7) rot=(0,0,1;0rad)
  Solid = false
  Source = -> Face107
  Symmetric = false
FEATURE [Part::Revolution] Revolve116  label="removeToCreateScrewAndThreadedInsertHole044"
  Angle = 360
  Axis = (0,1,0)
  Base = (0,0,0)
  FaceMakerClass = Part::FaceMakerBullseye
  Placement = pos=(30.3,30.3,51.7) rot=(0,0,1;0rad)
  Solid = false
  Source = -> Face108
  Symmetric = false
FEATURE [Part::MultiFuse] Fusion083  label="createThreadedInsertHolesForFan004"
  Shapes = -> [Revolve113,Revolve114,Revolve115,Revolve116]
FEATURE [Part::Box] Box024  label="removeToCreteHoleForPlugHousing026"
  AttacherType = Attacher::AttachEngine3D
  Height = 28.6
  Length = 10
  Placement = pos=(-2,0,21.7) rot=(0,0,1;0rad)
  Width = 19
FEATURE [Part::Cylinder] Cylinder038  label="removeToCreteHoleForPlugHousing027"
  Angle = 360
  AttacherType = Attacher::AttachEngine3D
  Height = 20
  Placement = pos=(-2,19,36) rot=(0,1,0;1.5708rad)
  Radius = 14.3
FEATURE [Part::MultiFuse] Fusion084  label="removeToCreteHoleForPlugHousing028"
  Shapes = -> [Box024,Cylinder038]
FEATURE [Part::Cylinder] Cylinder039
  Angle = 360
  AttacherType = Attacher::AttachEngine3D
  Height = 20
  Placement = pos=(0,0,36.15) rot=(0,0,1;0rad)
  Radius = 14.3
FEATURE [Part::Cylinder] Cylinder040
  Angle = 360
  AttacherType = Attacher::AttachEngine3D
  Height = 10
  Placement = pos=(0,0,36.15) rot=(0,0,1;0rad)
  Radius = 4
FEATURE [Part::Box] Box025  label="removeToCreteHoleForPlugHousing030"
  AttacherType = Attacher::AttachEngine3D
  Height = 28.6
  Length = 20
  Placement = pos=(106.15,0,21.7) rot=(0,0,1;0rad)
  Width = 19
FEATURE [Part::MultiFuse] Fusion086  label="removeToCreteHoleForPlugHousing031"
  Placement = pos=(70,19,36) rot=(0,1,0;1.5708rad)
  Shapes = -> [Cylinder039,Cylinder040]
FEATURE [Part::MultiFuse] Fusion085  label="removeToCreteHoleForPlugHousing029"
  Shapes = -> [Box025,Fusion086]
FEATURE [Sketcher::SketchObject] Sketch055
  FullyConstrained = true
  Placement = pos=(117,19,0) rot=(0.57735,0.57735,0.57735;2.0944rad)
  sketch-geometry (48):
    g0: LineSegment StartX=-49.19 StartY=69.25 StartZ=0 EndX=-49.19 EndY=66.25 EndZ=0
    g1: LineSegment StartX=-49.19 StartY=63.5 StartZ=0 EndX=-49.19 EndY=60.5 EndZ=0
    g2: LineSegment StartX=-49.19 StartY=57.75 StartZ=0 EndX=-49.19 EndY=54.75 EndZ=0
    g3: LineSegment StartX=-49.19 StartY=52 StartZ=0 EndX=-49.19 EndY=49 EndZ=0
    g4: LineSegment StartX=-49.19 StartY=46.25 StartZ=0 EndX=-49.19 EndY=43.25 EndZ=0
    g5: LineSegment StartX=-49.19 StartY=40.5 StartZ=0 EndX=-49.19 EndY=37.5 EndZ=0
    g6: LineSegment StartX=-49.19 StartY=34.5 StartZ=0 EndX=-49.19 EndY=31.5 EndZ=0
    g7: LineSegment StartX=-49.19 StartY=28.75 StartZ=0 EndX=-49.19 EndY=25.75 EndZ=0
    g8: LineSegment StartX=-49.19 StartY=23 StartZ=0 EndX=-49.19 EndY=20 EndZ=0
    g9: LineSegment StartX=-49.19 StartY=17.25 StartZ=0 EndX=-49.19 EndY=14.25 EndZ=0
    g10: LineSegment StartX=-49.19 StartY=11.5 StartZ=0 EndX=-49.19 EndY=8.5 EndZ=0
    g11: LineSegment StartX=-49.19 StartY=5.75 StartZ=0 EndX=-49.19 EndY=2.75 EndZ=0
    g12: ArcOfCircle CenterX=-1.5 CenterY=67.75 CenterZ=0 NormalX=0 NormalY=0 NormalZ=1 AngleXU=0 Radius=1.5 StartAngle=4.71239 EndAngle=7.85398
    g13: ArcOfCircle CenterX=-1.5 CenterY=62 CenterZ=0 NormalX=0 NormalY=0 NormalZ=1 AngleXU=0 Radius=1.5 StartAngle=4.71239 EndAngle=7.85398
    g14: ArcOfCircle CenterX=-1.5 CenterY=56.25 CenterZ=0 NormalX=0 NormalY=0 NormalZ=1 AngleXU=0 Radius=1.5 StartAngle=4.71239 EndAngle=7.85398
    g15: ArcOfCircle CenterX=-11.49 CenterY=50.5 CenterZ=0 NormalX=0 NormalY=0 NormalZ=1 AngleXU=0 Radius=1.5 StartAngle=4.71239 EndAngle=7.85398
    g16: ArcOfCircle CenterX=-16.28 CenterY=44.75 CenterZ=0 NormalX=0 NormalY=0 NormalZ=1 AngleXU=0 Radius=1.5 StartAngle=4.71239 EndAngle=7.85398
    g17: ArcOfCircle CenterX=-18.2337 CenterY=39 CenterZ=0 NormalX=0 NormalY=0 NormalZ=1 AngleXU=0 Radius=1.5 StartAngle=4.71485 EndAngle=7.85398
    g18: ArcOfCircle CenterX=-16.2837 CenterY=27.25 CenterZ=0 NormalX=0 NormalY=0 NormalZ=1 AngleXU=0 Radius=1.5 StartAngle=4.71485 EndAngle=7.85398
    g19: ArcOfCircle CenterX=-18.2337 CenterY=33 CenterZ=0 NormalX=0 NormalY=0 NormalZ=1 AngleXU=0 Radius=1.5 StartAngle=4.71485 EndAngle=7.85398
    g20: ArcOfCircle CenterX=-11.49 CenterY=21.5 CenterZ=0 NormalX=0 NormalY=0 NormalZ=1 AngleXU=0 Radius=1.5 StartAngle=4.71239 EndAngle=7.85398
    g21: ArcOfCircle CenterX=-1.5 CenterY=4.25 CenterZ=0 NormalX=0 NormalY=0 NormalZ=1 AngleXU=0 Radius=1.5 StartAngle=4.71239 EndAngle=7.85398
    g22: ArcOfCircle CenterX=-1.5 CenterY=10 CenterZ=0 NormalX=0 NormalY=0 NormalZ=1 AngleXU=0 Radius=1.5 StartAngle=4.71239 EndAngle=7.85398
    g23: ArcOfCircle CenterX=-1.5 CenterY=15.75 CenterZ=0 NormalX=0 NormalY=0 NormalZ=1 AngleXU=0 Radius=1.5 StartAngle=4.71239 EndAngle=7.85398
    g24: LineSegment StartX=-49.19 StartY=69.25 StartZ=0 EndX=-1.5 EndY=69.25 EndZ=0
    g25: LineSegment StartX=-49.19 StartY=66.25 StartZ=0 EndX=-1.5 EndY=66.25 EndZ=0
    g26: LineSegment StartX=-49.19 StartY=63.5 StartZ=0 EndX=-1.5 EndY=63.5 EndZ=0
    g27: LineSegment StartX=-49.19 StartY=60.5 StartZ=0 EndX=-1.5 EndY=60.5 EndZ=0
    g28: LineSegment StartX=-49.19 StartY=57.75 StartZ=0 EndX=-1.5 EndY=57.75 EndZ=0
    g29: LineSegment StartX=-49.19 StartY=54.75 StartZ=0 EndX=-1.5 EndY=54.75 EndZ=0
    g30: LineSegment StartX=-49.19 StartY=52 StartZ=0 EndX=-11.49 EndY=52 EndZ=0
    g31: LineSegment StartX=-49.19 StartY=49 StartZ=0 EndX=-11.49 EndY=49 EndZ=0
    g32: LineSegment StartX=-49.19 StartY=46.25 StartZ=0 EndX=-16.28 EndY=46.25 EndZ=0
    g33: LineSegment StartX=-49.19 StartY=43.25 StartZ=0 EndX=-16.28 EndY=43.25 EndZ=0
    g34: LineSegment StartX=-49.19 StartY=40.5 StartZ=0 EndX=-18.2337 EndY=40.5 EndZ=0
    g35: LineSegment StartX=-49.19 StartY=37.5 StartZ=0 EndX=-18.23 EndY=37.5 EndZ=0
    g36: LineSegment StartX=-49.19 StartY=34.5 StartZ=0 EndX=-18.2337 EndY=34.5 EndZ=0
    g37: LineSegment StartX=-49.19 StartY=31.5 StartZ=0 EndX=-18.23 EndY=31.5 EndZ=0
    g38: LineSegment StartX=-49.19 StartY=28.75 StartZ=0 EndX=-16.2837 EndY=28.75 EndZ=0
    g39: LineSegment StartX=-49.19 StartY=25.75 StartZ=0 EndX=-16.28 EndY=25.75 EndZ=0
    g40: LineSegment StartX=-49.19 StartY=23 StartZ=0 EndX=-11.49 EndY=23 EndZ=0
    g41: LineSegment StartX=-49.19 StartY=20 StartZ=0 EndX=-11.49 EndY=20 EndZ=0
    g42: LineSegment StartX=-49.19 StartY=17.25 StartZ=0 EndX=-1.5 EndY=17.25 EndZ=0
    g43: LineSegment StartX=-49.19 StartY=14.25 StartZ=0 EndX=-1.5 EndY=14.25 EndZ=0
    g44: LineSegment StartX=-49.19 StartY=11.5 StartZ=0 EndX=-1.5 EndY=11.5 EndZ=0
    g45: LineSegment StartX=-49.19 StartY=8.5 StartZ=0 EndX=-1.5 EndY=8.5 EndZ=0
    g46: LineSegment StartX=-49.19 StartY=5.75 StartZ=0 EndX=-1.5 EndY=5.75 EndZ=0
    g47: LineSegment StartX=-49.19 StartY=2.75 StartZ=0 EndX=-1.5 EndY=2.75 EndZ=0
  constraints (120):
    c: Vertical(g0)
    c: Distance(g0) = 3
    c: Block(g0)
    c: Vertical(g1)
    c: Distance(g1) = 3
    c: Vertical(g2)
    c: Equal(g0,g2) = 3
    c: Block(g2)
    c: Vertical(g3)
    c: Equal(g1,g3) = 3
    c: Vertical(g4)
    c: Equal(g0,g4) = 3
    c: Block(g4)
    c: Vertical(g5)
    c: Equal(g1,g5) = 3
    c: Vertical(g6)
    c: Equal(g0,g6) = 3
    c: Block(g6)
    c: Vertical(g7)
    c: Equal(g1,g7) = 3
    c: Vertical(g8)
    c: Equal(g0,g8) = 3
    c: Block(g8)
    c: Vertical(g9)
    c: Equal(g1,g9) = 3
    c: Vertical(g10)
    c: Equal(g0,g10) = 3
    c: Block(g10)
    c: Vertical(g11)
    c: Equal(g1,g11) = 3
    c: Block(g12)
    c: Block(g13)
    c: Block(g14)
    c: Block(g15)
    c: Block(g16)
    c: Block(g17)
    c: Block(g18)
    c: Block(g19)
    c: Block(g20)
    c: Block(g21)
    c: Block(g22)
    c: Block(g23)
    c: Block(g11)
    c: Block(g9)
    c: Block(g7)
    c: Block(g5)
    c: Block(g3)
    c: Block(g1)
    c: Coincident(g24,g0)
    c: Coincident(g24,g12)
    c: Horizontal(g24)
    c: Coincident(g25,g0)
    c: Coincident(g25,g12)
    c: Horizontal(g25)
    c: Coincident(g26,g1)
    c: Coincident(g26,g13)
    c: Horizontal(g26)
    c: Coincident(g27,g1)
    c: Coincident(g27,g13)
    c: Horizontal(g27)
    c: Coincident(g28,g2)
    c: Coincident(g28,g14)
    c: Horizontal(g28)
    c: Coincident(g29,g2)
    c: Coincident(g29,g14)
    c: Horizontal(g29)
    c: Coincident(g30,g3)
    c: Coincident(g30,g15)
    c: Horizontal(g30)
    c: Coincident(g31,g3)
    c: Coincident(g31,g15)
    c: Horizontal(g31)
    c: Coincident(g32,g4)
    c: Coincident(g32,g16)
    c: Horizontal(g32)
    c: Coincident(g33,g4)
    c: Coincident(g33,g16)
    c: Horizontal(g33)
    c: Coincident(g34,g5)
    c: Coincident(g34,g17)
    c: Horizontal(g34)
    c: Coincident(g35,g5)
    c: Coincident(g35,g17)
    c: Horizontal(g35)
    c: Coincident(g36,g6)
    c: Coincident(g36,g19)
    c: Horizontal(g36)
    c: Coincident(g37,g6)
    c: Coincident(g37,g19)
    c: Horizontal(g37)
    c: Coincident(g38,g7)
    c: Coincident(g38,g18)
    c: Horizontal(g38)
    c: Coincident(g39,g7)
    c: Coincident(g39,g18)
    c: Horizontal(g39)
    c: Coincident(g40,g8)
    c: Coincident(g40,g20)
    c: Horizontal(g40)
    c: Coincident(g41,g8)
    c: Coincident(g41,g20)
    c: Horizontal(g41)
    c: Coincident(g42,g9)
    c: Coincident(g42,g23)
    c: Horizontal(g42)
    c: Coincident(g43,g9)
    c: Coincident(g43,g23)
    c: Horizontal(g43)
    c: Coincident(g44,g10)
    c: Coincident(g44,g22)
    c: Horizontal(g44)
    c: Coincident(g45,g10)
    c: Coincident(g45,g22)
    c: Horizontal(g45)
    c: Coincident(g46,g11)
    c: Coincident(g46,g21)
    c: Horizontal(g46)
    c: Coincident(g47,g11)
    c: Coincident(g47,g21)
    c: Horizontal(g47)
FEATURE [Part::Extrusion] Extrude046
  Base = -> Sketch055
  Dir = (1,0,0)
  DirMode = 2
  FaceMakerClass = Part::FaceMakerBullseye
  LengthFwd = 23
  LengthRev = 0
  Placement = pos=(-19,0,0) rot=(0,0,1;0rad)
  Solid = true
  Symmetric = false
FEATURE [Part::Fillet] Fillet038  label="removeToCreateVentalationHoles001"
  Base = -> Extrude046
  Edges = <same value as first occurrence — deduplicated (x4 in doc)>
  Placement = pos=(7,0,0) rot=(0,0,1;0rad)
FEATURE [Sketcher::SketchObject] Sketch056  label="topSketch014"
  FullyConstrained = true
  sketch-geometry (22):
    g0: LineSegment StartX=5.21097e-06 StartY=3 StartZ=0 EndX=5.21097e-06 EndY=19 EndZ=0
    g1: ArcOfCircle CenterX=19 CenterY=19 CenterZ=0 NormalX=0 NormalY=0 NormalZ=1 AngleXU=0 Radius=19 StartAngle=1.5708 EndAngle=3.14159
    g2: ArcOfCircle CenterX=19 CenterY=19 CenterZ=0 NormalX=0 NormalY=0 NormalZ=1 AngleXU=0 Radius=16 StartAngle=1.5708 EndAngle=3.14159
    g3: LineSegment StartX=114 StartY=35 StartZ=0 EndX=19 EndY=35 EndZ=0
    g4: LineSegment StartX=5.21097e-06 StartY=3 StartZ=0 EndX=5.21097e-06 EndY=0 EndZ=0
    g5: LineSegment StartX=3 StartY=0 StartZ=0 EndX=5.21097e-06 EndY=0 EndZ=0
    g6: LineSegment StartX=3 StartY=19 StartZ=0 EndX=3 EndY=0 EndZ=0
    g7: LineSegment StartX=19 StartY=38 StartZ=0 EndX=124 EndY=38 EndZ=0
    g8: Circle CenterX=119 CenterY=35 CenterZ=0 NormalX=0 NormalY=0 NormalZ=1 AngleXU=0 Radius=1
    g9: Circle CenterX=121 CenterY=35 CenterZ=0 NormalX=0 NormalY=0 NormalZ=1 AngleXU=0 Radius=1
    g10: Circle CenterX=121 CenterY=33 CenterZ=0 NormalX=0 NormalY=0 NormalZ=1 AngleXU=0 Radius=1
    g11: BSplineCurve PolesCount=3 KnotsCount=2 Degree=2 IsPeriodic=0
    g12: GeomPoint X=119 Y=35 Z=0
    g13: GeomPoint X=121 Y=33 Z=0
    g14: LineSegment StartX=119 StartY=35 StartZ=0 EndX=114 EndY=35 EndZ=0
    g15: ArcOfCircle CenterX=105 CenterY=19 CenterZ=0 NormalX=0 NormalY=0 NormalZ=1 AngleXU=0 Radius=16 StartAngle=5.60905 EndAngle=6.28319
    g16: LineSegment StartX=121 StartY=33 StartZ=0 EndX=121 EndY=19 EndZ=0
    g17: LineSegment StartX=117.5 StartY=9.01251 StartZ=0 EndX=121.163 EndY=9.0125 EndZ=0
    g18: ArcOfCircle CenterX=105 CenterY=19 CenterZ=0 NormalX=0 NormalY=0 NormalZ=1 AngleXU=0 Radius=20.6155 StartAngle=5.7297 EndAngle=6.28319
    g19: LineSegment StartX=121.163 StartY=9.0125 StartZ=0 EndX=122.538 EndY=8.16329 EndZ=0
    g20: LineSegment StartX=124 StartY=38 StartZ=0 EndX=125.616 EndY=38 EndZ=0
    g21: LineSegment StartX=125.616 StartY=19 StartZ=0 EndX=125.616 EndY=38 EndZ=0
  constraints (49):
    c: Vertical(g0)
    c: Block(g0)
    c: Coincident(g1,g0)
    c: Block(g1)
    c: Coincident(g2,g1)
    c: Block(g2)
    c: Coincident(g3,g2)
    c: Horizontal(g3)
    c: Tangent(g3,g2)
    c: Coincident(g4,g0)
    c: Distance(g4) = 3
    c: Vertical(g4)
    c: Coincident(g5,g4)
    c: Horizontal(g5)
    c: Coincident(g6,g2)
    c: Coincident(g6,g5)
    c: Vertical(g6)
    c: Horizontal(g7)
    c: Distance(g7) = 105
    c: Coincident(g7,g1)
    c: Block(g3)
    c: Weight(g8) = 1
    c: Equal(g8,g9)
    c: Equal(g8,g10)
    c: InternalAlignment(g8,g11)
    c: InternalAlignment(g9,g11)
    c: InternalAlignment(g10,g11)
    c: InternalAlignment(g12,g11)
    c: InternalAlignment(g13,g11)
    c: Block(g11)
    c: Coincident(g14,g11)
    c: Coincident(g14,g3)
    c: Horizontal(g14)
    c: Block(g15)
    c: Coincident(g16,g11)
    c: Coincident(g16,g15)
    c: Vertical(g16)
    c: Distance(g16) = 14
    c: Coincident(g17,g15)
    c: Block(g18)
    c: Coincident(g19,g18)
    c: Coincident(g20,g7)
    c: Horizontal(g20)
    c: Vertical(g21)
    c: Coincident(g20,g21)
    c: Block(g20)
    c: Block(g21)
    c: Block(g19)
    c: Block(g17)
FEATURE [Part::Box] Box026  label="removeToCreteHoleForPlugHousing032"
  AttacherType = Attacher::AttachEngine3D
  Height = 28.6
  Length = 10
  Placement = pos=(-2,0,21.7) rot=(0,0,1;0rad)
  Width = 19
FEATURE [Part::Feature] Face109 .. Face112  x4 (patterned run collapsed; names and placements below)
  shape: bbox 3.5 x 17.8 x 2e-07 mm, 1 faces, 0 solids (baked)
FEATURE [Part::Revolution] Revolve117  label="removeToCreateScrewAndThreadedInsertHole045"
  Angle = 360
  Axis = (0,1,0)
  Base = (0,0,0)
  FaceMakerClass = Part::FaceMakerBullseye
  Placement = pos=(62.3,30.3,19.7) rot=(0,0,1;0rad)
  Solid = false
  Source = -> Face109
  Symmetric = false
FEATURE [Part::Revolution] Revolve118  label="removeToCreateScrewAndThreadedInsertHole046"
  Angle = 360
  Axis = (0,1,0)
  Base = (0,0,0)
  FaceMakerClass = Part::FaceMakerBullseye
  Placement = pos=(62.3,30.3,51.7) rot=(0,0,1;0rad)
  Solid = false
  Source = -> Face110
  Symmetric = false
FEATURE [Part::Revolution] Revolve119  label="removeToCreateScrewAndThreadedInsertHole047"
  Angle = 360
  Axis = (0,1,0)
  Base = (0,0,0)
  FaceMakerClass = Part::FaceMakerBullseye
  Placement = pos=(30.3,30.3,19.7) rot=(0,0,1;0rad)
  Solid = false
  Source = -> Face111
  Symmetric = false
FEATURE [Part::Revolution] Revolve120  label="removeToCreateScrewAndThreadedInsertHole048"
  Angle = 360
  Axis = (0,1,0)
  Base = (0,0,0)
  FaceMakerClass = Part::FaceMakerBullseye
  Placement = pos=(30.3,30.3,51.7) rot=(0,0,1;0rad)
  Solid = false
  Source = -> Face112
  Symmetric = false
FEATURE [Part::MultiFuse] Fusion087  label="createThreadedInsertHolesForFan005"
  Shapes = -> [Revolve117,Revolve118,Revolve119,Revolve120]
FEATURE [Part::Extrusion] Extrude047
  Base = -> Sketch056
  Dir = (0,0,1)
  DirMode = 2
  FaceMakerClass = Part::FaceMakerBullseye
  LengthFwd = 72
  LengthRev = 0
  Solid = true
  Symmetric = false
FEATURE [Part::Fillet] Fillet039  label="top019"
  Base = -> Extrude047
  Edges = 1 edges r=2: [Edge35]
FEATURE [Sketcher::SketchObject] Sketch057
  FullyConstrained = false
  Placement = pos=(0,0,0) rot=(1,0,0;1.5708rad)
  sketch-geometry (24):
    g0: ArcOfCircle CenterX=-4 CenterY=-10.5 CenterZ=0 NormalX=0 NormalY=0 NormalZ=1 AngleXU=0 Radius=1.5 StartAngle=6e-16 EndAngle=3.14159
    g1: ArcOfCircle CenterX=-34.2 CenterY=-10.5 CenterZ=0 NormalX=0 NormalY=0 NormalZ=1 AngleXU=0 Radius=1.5 StartAngle=0 EndAngle=3.14159
    g2: ArcOfCircle CenterX=-34.2 CenterY=-27.7 CenterZ=0 NormalX=0 NormalY=0 NormalZ=1 AngleXU=0 Radius=1.5 StartAngle=3.14159 EndAngle=6.28319
    g3: ArcOfCircle CenterX=-4 CenterY=-27.7 CenterZ=0 NormalX=0 NormalY=0 NormalZ=1 AngleXU=0 Radius=1.5 StartAngle=3.1416 EndAngle=6.28319
    g4: ArcOfCircle CenterX=-10 CenterY=-4.3 CenterZ=0 NormalX=0 NormalY=0 NormalZ=1 AngleXU=0 Radius=1.5 StartAngle=2e-16 EndAngle=3.14159
    g5: ArcOfCircle CenterX=-16.1 CenterY=-1.8 CenterZ=0 NormalX=0 NormalY=0 NormalZ=1 AngleXU=0 Radius=1.5 StartAngle=5e-16 EndAngle=3.14159
    g6: ArcOfCircle CenterX=-22.1 CenterY=-1.8 CenterZ=0 NormalX=0 NormalY=0 NormalZ=1 AngleXU=0 Radius=1.5 StartAngle=5e-16 EndAngle=3.14159
    g7: ArcOfCircle CenterX=-28.2 CenterY=-4.3 CenterZ=0 NormalX=0 NormalY=0 NormalZ=1 AngleXU=0 Radius=1.5 StartAngle=2e-16 EndAngle=3.14159
    g8: ArcOfCircle CenterX=-10 CenterY=-33.9 CenterZ=0 NormalX=0 NormalY=0 NormalZ=1 AngleXU=0 Radius=1.5 StartAngle=3.14159 EndAngle=6.28319
    g9: ArcOfCircle CenterX=-16.1 CenterY=-36.4 CenterZ=0 NormalX=0 NormalY=0 NormalZ=1 AngleXU=0 Radius=1.5 StartAngle=3.14159 EndAngle=6.28319
    g10: ArcOfCircle CenterX=-22.1 CenterY=-36.4 CenterZ=0 NormalX=0 NormalY=0 NormalZ=1 AngleXU=0 Radius=1.5 StartAngle=3.14159 EndAngle=6.28319
    g11: ArcOfCircle CenterX=-28.2 CenterY=-33.9 CenterZ=0 NormalX=0 NormalY=0 NormalZ=1 AngleXU=0 Radius=1.5 StartAngle=3.14159 EndAngle=6.28319
    g12: LineSegment StartX=-35.7 StartY=-10.5 StartZ=0 EndX=-35.7 EndY=-27.7 EndZ=0
    g13: LineSegment StartX=-32.7 StartY=-10.5 StartZ=0 EndX=-32.7 EndY=-27.7 EndZ=0
    g14: LineSegment StartX=-29.7 StartY=-33.9 StartZ=0 EndX=-29.7 EndY=-4.3 EndZ=0
    g15: LineSegment StartX=-26.7 StartY=-33.9 StartZ=0 EndX=-26.7 EndY=-4.3 EndZ=0
    g16: LineSegment StartX=-2.5 StartY=-10.5 StartZ=0 EndX=-2.5 EndY=-27.7 EndZ=0
    g17: LineSegment StartX=-8.5 StartY=-4.3 StartZ=0 EndX=-8.5 EndY=-33.9 EndZ=0
    g18: LineSegment StartX=-5.5 StartY=-10.5 StartZ=0 EndX=-5.5 EndY=-27.7 EndZ=0
    g19: LineSegment StartX=-11.5 StartY=-4.3 StartZ=0 EndX=-11.5 EndY=-33.9 EndZ=0
    g20: LineSegment StartX=-14.6 StartY=-1.8 StartZ=0 EndX=-14.6 EndY=-36.4 EndZ=0
    g21: LineSegment StartX=-17.6 StartY=-1.8 StartZ=0 EndX=-17.6 EndY=-36.4 EndZ=0
    g22: LineSegment StartX=-20.6 StartY=-36.4 StartZ=0 EndX=-20.6 EndY=-1.8 EndZ=0
    g23: LineSegment StartX=-23.6 StartY=-1.8 StartZ=0 EndX=-23.6 EndY=-36.4 EndZ=0
  constraints (48):
    c: Block(g0)
    c: Block(g1)
    c: Block(g2)
    c: Block(g3)
    c: Block(g4)
    c: Block(g5)
    c: Block(g6)
    c: Block(g7)
    c: Block(g8)
    c: Block(g9)
    c: Block(g10)
    c: Block(g11)
    c: Coincident(g12,g1)
    c: Coincident(g12,g2)
    c: Vertical(g12)
    c: Coincident(g13,g1)
    c: Coincident(g13,g2)
    c: Vertical(g13)
    c: Coincident(g14,g11)
    c: Coincident(g14,g7)
    c: Vertical(g14)
    c: Coincident(g15,g11)
    c: Coincident(g15,g7)
    c: Vertical(g15)
    c: Coincident(g16,g0)
    c: Coincident(g16,g3)
    c: Vertical(g16)
    c: Coincident(g17,g4)
    c: Coincident(g17,g8)
    c: Vertical(g17)
    c: Coincident(g18,g0)
    c: Coincident(g18,g3)
    c: Vertical(g18)
    c: Coincident(g19,g4)
    c: Coincident(g19,g8)
    c: Vertical(g19)
    c: Coincident(g20,g5)
    c: Coincident(g20,g9)
    c: Vertical(g20)
    c: Coincident(g21,g5)
    c: Coincident(g21,g9)
    c: Vertical(g21)
    c: Coincident(g22,g10)
    c: Coincident(g22,g6)
    c: Vertical(g22)
    c: Coincident(g23,g6)
    c: Coincident(g23,g10)
    c: Vertical(g23)
FEATURE [Part::Extrusion] Extrude048  label="removeToCreateFanGrillHoles004"
  Base = -> Sketch057
  Dir = (0,-1,6e-16)
  DirMode = 2
  FaceMakerClass = Part::FaceMakerBullseye
  LengthFwd = 10
  LengthRev = 0
  Placement = pos=(65.4,44,54.82) rot=(0,0,1;0rad)
  Solid = true
  Symmetric = false
FEATURE [Part::Cut] Cut040  label="top021"
  Base = -> Fillet039
  Tool = -> Extrude048
FEATURE [Part::Cylinder] Cylinder041  label="removeToCreteHoleForPlugHousing034"
  Angle = 360
  AttacherType = Attacher::AttachEngine3D
  Height = 20
  Placement = pos=(-2,19,36) rot=(0,1,0;1.5708rad)
  Radius = 14.3
FEATURE [Part::MultiFuse] Fusion089  label="removeToCreteHoleForPlugHousing035"
  Shapes = -> [Box026,Cylinder041]
FEATURE [Part::Cylinder] Cylinder042
  Angle = 360
  AttacherType = Attacher::AttachEngine3D
  Height = 20
  Placement = pos=(0,0,36.15) rot=(0,0,1;0rad)
  Radius = 14.3
FEATURE [Part::Cylinder] Cylinder043
  Angle = 360
  AttacherType = Attacher::AttachEngine3D
  Height = 10
  Placement = pos=(0,0,36.15) rot=(0,0,1;0rad)
  Radius = 4
FEATURE [Part::Box] Box027  label="removeToCreteHoleForPlugHousing036"
  AttacherType = Attacher::AttachEngine3D
  Height = 28.6
  Length = 20
  Placement = pos=(106.15,0,21.7) rot=(0,0,1;0rad)
  Width = 19
FEATURE [Part::Cut] Cut041  label="top022"
  Base = -> Cut040
  Tool = -> Fusion087
FEATURE [Part::Cut] Cut039  label="top020"
  Base = -> Cut041
  Tool = -> Fusion089
FEATURE [Part::MultiFuse] Fusion090  label="removeToCreteHoleForPlugHousing037"
  Placement = pos=(70,19,36) rot=(0,1,0;1.5708rad)
  Shapes = -> [Cylinder042,Cylinder043]
FEATURE [Part::MultiFuse] Fusion088  label="removeToCreteHoleForPlugHousing033"
  Shapes = -> [Box027,Fusion090]
FEATURE [Part::Cut] Cut042  label="removeToCreteHoleForPlugHousing038"
  Base = -> Cut039
  Tool = -> Fusion088
FEATURE [Part::MultiFuse] Fusion091  label="removeFromTop"
  Shapes = -> [Fillet038,Fusion085,Fusion084,Fusion083,Extrude045]
FEATURE [Part::Cut] Cut043  label="REAL TOP ====="
  Base = -> Fillet036
  Tool = -> Fusion091
FEATURE [Part::MultiFuse] Fusion092  label="caseScrewPillarBracket016"
  Shapes = -> [Extrude030,Extrude031,Extrude032,Extrude033,Extrude034,Extrude035,Extrude036,Extrude037,Box013,Box014]
FEATURE [Sketcher::SketchObject] Sketch058  label="topSketch015"
  FullyConstrained = true
  sketch-geometry (20):
    g0: LineSegment StartX=5.21097e-06 StartY=3 StartZ=0 EndX=5.21097e-06 EndY=19 EndZ=0
    g1: ArcOfCircle CenterX=19 CenterY=19 CenterZ=0 NormalX=0 NormalY=0 NormalZ=1 AngleXU=0 Radius=19 StartAngle=1.5708 EndAngle=3.14159
    g2: ArcOfCircle CenterX=19 CenterY=19 CenterZ=0 NormalX=0 NormalY=0 NormalZ=1 AngleXU=0 Radius=16 StartAngle=1.5708 EndAngle=3.14159
    g3: LineSegment StartX=114 StartY=35 StartZ=0 EndX=19 EndY=35 EndZ=0
    g4: LineSegment StartX=5.21097e-06 StartY=3 StartZ=0 EndX=5.21097e-06 EndY=0 EndZ=0
    g5: LineSegment StartX=3 StartY=0 StartZ=0 EndX=5.21097e-06 EndY=0 EndZ=0
    g6: LineSegment StartX=3 StartY=19 StartZ=0 EndX=3 EndY=0 EndZ=0
    g7: LineSegment StartX=19 StartY=38 StartZ=0 EndX=124 EndY=38 EndZ=0
    g8: Circle CenterX=119 CenterY=35 CenterZ=0 NormalX=0 NormalY=0 NormalZ=1 AngleXU=0 Radius=1
    g9: Circle CenterX=121 CenterY=35 CenterZ=0 NormalX=0 NormalY=0 NormalZ=1 AngleXU=0 Radius=1
    g10: Circle CenterX=121 CenterY=33 CenterZ=0 NormalX=0 NormalY=0 NormalZ=1 AngleXU=0 Radius=1
    g11: BSplineCurve PolesCount=3 KnotsCount=2 Degree=2 IsPeriodic=0
    g12: GeomPoint X=119 Y=35 Z=0
    g13: GeomPoint X=121 Y=33 Z=0
    g14: LineSegment StartX=119 StartY=35 StartZ=0 EndX=114 EndY=35 EndZ=0
    g15: ArcOfCircle CenterX=105 CenterY=19 CenterZ=0 NormalX=0 NormalY=0 NormalZ=1 AngleXU=0 Radius=19 StartAngle=5.7297 EndAngle=6.28319
    g16: ArcOfCircle CenterX=105 CenterY=19 CenterZ=0 NormalX=0 NormalY=0 NormalZ=1 AngleXU=0 Radius=16 StartAngle=5.60905 EndAngle=6.28319
    g17: LineSegment StartX=121 StartY=33 StartZ=0 EndX=121 EndY=19 EndZ=0
    g18: LineSegment StartX=124 StartY=38 StartZ=0 EndX=124 EndY=19 EndZ=0
    g19: LineSegment StartX=117.5 StartY=9.01251 StartZ=0 EndX=121.163 EndY=9.0125 EndZ=0
  constraints (46):
    c: Vertical(g0)
    c: Block(g0)
    c: Coincident(g1,g0)
    c: Block(g1)
    c: Coincident(g2,g1)
    c: Block(g2)
    c: Coincident(g3,g2)
    c: Horizontal(g3)
    c: Tangent(g3,g2)
    c: Coincident(g4,g0)
    c: Distance(g4) = 3
    c: Vertical(g4)
    c: Coincident(g5,g4)
    c: Horizontal(g5)
    c: Coincident(g6,g2)
    c: Coincident(g6,g5)
    c: Vertical(g6)
    c: Horizontal(g7)
    c: Distance(g7) = 105
    c: Coincident(g7,g1)
    c: Block(g3)
    c: Weight(g8) = 1
    c: Equal(g8,g9)
    c: Equal(g8,g10)
    c: InternalAlignment(g8,g11)
    c: InternalAlignment(g9,g11)
    c: InternalAlignment(g10,g11)
    c: InternalAlignment(g12,g11)
    c: InternalAlignment(g13,g11)
    c: Block(g11)
    c: Coincident(g14,g11)
    c: Coincident(g14,g3)
    c: Horizontal(g14)
    c: Block(g15)
    c: Coincident(g16,g15)
    c: Block(g16)
    c: Coincident(g17,g11)
    c: Coincident(g17,g16)
    c: Vertical(g17)
    c: Distance(g17) = 14
    c: Coincident(g18,g7)
    c: Coincident(g18,g15)
    c: Vertical(g18)
    c: Distance(g18) = 19
    c: Coincident(g19,g16)
    c: Coincident(g19,g15)
FEATURE [Part::Extrusion] Extrude049  label="top023"
  Base = -> Sketch058
  Dir = (0,0,1)
  DirMode = 2
  FaceMakerClass = Part::FaceMakerBullseye
  LengthFwd = 72
  LengthRev = 0
  Solid = true
  Symmetric = false
FEATURE [Sketcher::SketchObject] Sketch059
  FullyConstrained = true
  MapMode = 3
  Placement = pos=(0,0,0) rot=(1,0,0;1.5708rad)
  Support = -> [Extrude049]
  sketch-geometry (8):
    g0: Circle CenterX=80.351 CenterY=-67.6202 CenterZ=0 NormalX=0 NormalY=0 NormalZ=1 AngleXU=0 Radius=2
    g1: Circle CenterX=80.351 CenterY=-67.6202 CenterZ=0 NormalX=0 NormalY=0 NormalZ=1 AngleXU=0 Radius=3
    g2: Circle CenterX=80.351 CenterY=-4.92017 CenterZ=0 NormalX=0 NormalY=0 NormalZ=1 AngleXU=0 Radius=2
    g3: Circle CenterX=80.351 CenterY=-4.92017 CenterZ=0 NormalX=0 NormalY=0 NormalZ=1 AngleXU=0 Radius=3
    g4: Circle CenterX=23.851 CenterY=-4.92017 CenterZ=0 NormalX=0 NormalY=0 NormalZ=1 AngleXU=0 Radius=2
    g5: Circle CenterX=23.851 CenterY=-4.92017 CenterZ=0 NormalX=0 NormalY=0 NormalZ=1 AngleXU=0 Radius=3
    g6: Circle CenterX=23.851 CenterY=-67.6202 CenterZ=0 NormalX=0 NormalY=0 NormalZ=1 AngleXU=0 Radius=2
    g7: Circle CenterX=23.851 CenterY=-67.6202 CenterZ=0 NormalX=0 NormalY=0 NormalZ=1 AngleXU=0 Radius=3
  constraints (8):
    c: Block(g3)
    c: Block(g2)
    c: Block(g1)
    c: Block(g0)
    c: Block(g6)
    c: Block(g7)
    c: Block(g4)
    c: Block(g5)
FEATURE [Sketcher::SketchObject] Sketch060
  FullyConstrained = true
  MapMode = 3
  Placement = pos=(0,0,0) rot=(1,0,0;1.5708rad)
  Support = -> [Extrude049]
  sketch-geometry (8):
    g0: Circle CenterX=80.351 CenterY=-67.6202 CenterZ=0 NormalX=0 NormalY=0 NormalZ=1 AngleXU=0 Radius=3
    g1: Circle CenterX=80.351 CenterY=-4.92017 CenterZ=0 NormalX=0 NormalY=0 NormalZ=1 AngleXU=0 Radius=3
    g2: Circle CenterX=23.851 CenterY=-4.92017 CenterZ=0 NormalX=0 NormalY=0 NormalZ=1 AngleXU=0 Radius=3
    g3: Circle CenterX=23.851 CenterY=-67.6202 CenterZ=0 NormalX=0 NormalY=0 NormalZ=1 AngleXU=0 Radius=3
    g4: Circle CenterX=23.851 CenterY=-67.6202 CenterZ=0 NormalX=0 NormalY=0 NormalZ=1 AngleXU=0 Radius=5
    g5: Circle CenterX=80.351 CenterY=-67.6202 CenterZ=0 NormalX=0 NormalY=0 NormalZ=1 AngleXU=0 Radius=5
    g6: Circle CenterX=23.851 CenterY=-4.92017 CenterZ=0 NormalX=0 NormalY=0 NormalZ=1 AngleXU=0 Radius=5
    g7: Circle CenterX=80.351 CenterY=-4.92017 CenterZ=0 NormalX=0 NormalY=0 NormalZ=1 AngleXU=0 Radius=5
  constraints (8):
    c: Block(g1)
    c: Block(g0)
    c: Block(g3)
    c: Block(g2)
    c: Block(g5)
    c: Block(g4)
    c: Block(g6)
    c: Block(g7)
FEATURE [Sketcher::SketchObject] Sketch061
  FullyConstrained = true
  MapMode = 3
  Placement = pos=(0,0,0) rot=(1,0,0;1.5708rad)
  sketch-geometry (8):
    g0: Circle CenterX=80.351 CenterY=-67.6202 CenterZ=0 NormalX=0 NormalY=0 NormalZ=1 AngleXU=0 Radius=3
    g1: Circle CenterX=80.351 CenterY=-4.92017 CenterZ=0 NormalX=0 NormalY=0 NormalZ=1 AngleXU=0 Radius=3
    g2: Circle CenterX=23.851 CenterY=-4.92017 CenterZ=0 NormalX=0 NormalY=0 NormalZ=1 AngleXU=0 Radius=3
    g3: Circle CenterX=23.851 CenterY=-67.6202 CenterZ=0 NormalX=0 NormalY=0 NormalZ=1 AngleXU=0 Radius=3
    g4: Circle CenterX=23.851 CenterY=-67.6202 CenterZ=0 NormalX=0 NormalY=0 NormalZ=1 AngleXU=0 Radius=5
    g5: Circle CenterX=80.351 CenterY=-67.6202 CenterZ=0 NormalX=0 NormalY=0 NormalZ=1 AngleXU=0 Radius=5
    g6: Circle CenterX=23.851 CenterY=-4.92017 CenterZ=0 NormalX=0 NormalY=0 NormalZ=1 AngleXU=0 Radius=5
    g7: Circle CenterX=80.351 CenterY=-4.92017 CenterZ=0 NormalX=0 NormalY=0 NormalZ=1 AngleXU=0 Radius=5
  constraints (8):
    c: Block(g1)
    c: Block(g0)
    c: Block(g3)
    c: Block(g2)
    c: Block(g5)
    c: Block(g4)
    c: Block(g6)
    c: Block(g7)
FEATURE [Sketcher::SketchObject] Sketch062  label="topSketch016"
  FullyConstrained = true
  sketch-geometry (20):
    g0: LineSegment StartX=5.21097e-06 StartY=3 StartZ=0 EndX=5.21097e-06 EndY=19 EndZ=0
    g1: ArcOfCircle CenterX=19 CenterY=19 CenterZ=0 NormalX=0 NormalY=0 NormalZ=1 AngleXU=0 Radius=19 StartAngle=1.5708 EndAngle=3.14159
    g2: ArcOfCircle CenterX=19 CenterY=19 CenterZ=0 NormalX=0 NormalY=0 NormalZ=1 AngleXU=0 Radius=16 StartAngle=1.5708 EndAngle=3.14159
    g3: LineSegment StartX=114 StartY=35 StartZ=0 EndX=19 EndY=35 EndZ=0
    g4: LineSegment StartX=5.21097e-06 StartY=3 StartZ=0 EndX=5.21097e-06 EndY=0 EndZ=0
    g5: LineSegment StartX=3 StartY=0 StartZ=0 EndX=5.21097e-06 EndY=0 EndZ=0
    g6: LineSegment StartX=3 StartY=19 StartZ=0 EndX=3 EndY=0 EndZ=0
    g7: LineSegment StartX=19 StartY=38 StartZ=0 EndX=124 EndY=38 EndZ=0
    g8: Circle CenterX=119 CenterY=35 CenterZ=0 NormalX=0 NormalY=0 NormalZ=1 AngleXU=0 Radius=1
    g9: Circle CenterX=121 CenterY=35 CenterZ=0 NormalX=0 NormalY=0 NormalZ=1 AngleXU=0 Radius=1
    g10: Circle CenterX=121 CenterY=33 CenterZ=0 NormalX=0 NormalY=0 NormalZ=1 AngleXU=0 Radius=1
    g11: BSplineCurve PolesCount=3 KnotsCount=2 Degree=2 IsPeriodic=0
    g12: GeomPoint X=119 Y=35 Z=0
    g13: GeomPoint X=121 Y=33 Z=0
    g14: LineSegment StartX=119 StartY=35 StartZ=0 EndX=114 EndY=35 EndZ=0
    g15: ArcOfCircle CenterX=105 CenterY=19 CenterZ=0 NormalX=0 NormalY=0 NormalZ=1 AngleXU=0 Radius=19 StartAngle=5.7297 EndAngle=6.28319
    g16: ArcOfCircle CenterX=105 CenterY=19 CenterZ=0 NormalX=0 NormalY=0 NormalZ=1 AngleXU=0 Radius=16 StartAngle=5.60905 EndAngle=6.28319
    g17: LineSegment StartX=121 StartY=33 StartZ=0 EndX=121 EndY=19 EndZ=0
    g18: LineSegment StartX=124 StartY=38 StartZ=0 EndX=124 EndY=19 EndZ=0
    g19: LineSegment StartX=117.5 StartY=9.01251 StartZ=0 EndX=121.163 EndY=9.0125 EndZ=0
  constraints (46):
    c: Vertical(g0)
    c: Block(g0)
    c: Coincident(g1,g0)
    c: Block(g1)
    c: Coincident(g2,g1)
    c: Block(g2)
    c: Coincident(g3,g2)
    c: Horizontal(g3)
    c: Tangent(g3,g2)
    c: Coincident(g4,g0)
    c: Distance(g4) = 3
    c: Vertical(g4)
    c: Coincident(g5,g4)
    c: Horizontal(g5)
    c: Coincident(g6,g2)
    c: Coincident(g6,g5)
    c: Vertical(g6)
    c: Horizontal(g7)
    c: Distance(g7) = 105
    c: Coincident(g7,g1)
    c: Block(g3)
    c: Weight(g8) = 1
    c: Equal(g8,g9)
    c: Equal(g8,g10)
    c: InternalAlignment(g8,g11)
    c: InternalAlignment(g9,g11)
    c: InternalAlignment(g10,g11)
    c: InternalAlignment(g12,g11)
    c: InternalAlignment(g13,g11)
    c: Block(g11)
    c: Coincident(g14,g11)
    c: Coincident(g14,g3)
    c: Horizontal(g14)
    c: Block(g15)
    c: Coincident(g16,g15)
    c: Block(g16)
    c: Coincident(g17,g11)
    c: Coincident(g17,g16)
    c: Vertical(g17)
    c: Distance(g17) = 14
    c: Coincident(g18,g7)
    c: Coincident(g18,g15)
    c: Vertical(g18)
    c: Distance(g18) = 19
    c: Coincident(g19,g16)
    c: Coincident(g19,g15)
FEATURE [Part::Extrusion] Extrude053  label="top024"
  Base = -> Sketch062
  Dir = (0,0,1)
  DirMode = 2
  FaceMakerClass = Part::FaceMakerBullseye
  LengthFwd = 72
  LengthRev = 0
  Solid = true
  Symmetric = false
FEATURE [Sketcher::SketchObject] Sketch063
  FullyConstrained = true
  MapMode = 3
  Placement = pos=(0,0,0) rot=(1,0,0;1.5708rad)
  Support = -> [Extrude053]
  sketch-geometry (8):
    g0: Circle CenterX=80.351 CenterY=-67.6202 CenterZ=0 NormalX=0 NormalY=0 NormalZ=1 AngleXU=0 Radius=2
    g1: Circle CenterX=80.351 CenterY=-67.6202 CenterZ=0 NormalX=0 NormalY=0 NormalZ=1 AngleXU=0 Radius=3
    g2: Circle CenterX=80.351 CenterY=-4.92017 CenterZ=0 NormalX=0 NormalY=0 NormalZ=1 AngleXU=0 Radius=2
    g3: Circle CenterX=80.351 CenterY=-4.92017 CenterZ=0 NormalX=0 NormalY=0 NormalZ=1 AngleXU=0 Radius=3
    g4: Circle CenterX=23.851 CenterY=-4.92017 CenterZ=0 NormalX=0 NormalY=0 NormalZ=1 AngleXU=0 Radius=2
    g5: Circle CenterX=23.851 CenterY=-4.92017 CenterZ=0 NormalX=0 NormalY=0 NormalZ=1 AngleXU=0 Radius=3
    g6: Circle CenterX=23.851 CenterY=-67.6202 CenterZ=0 NormalX=0 NormalY=0 NormalZ=1 AngleXU=0 Radius=2
    g7: Circle CenterX=23.851 CenterY=-67.6202 CenterZ=0 NormalX=0 NormalY=0 NormalZ=1 AngleXU=0 Radius=3
  constraints (8):
    c: Block(g3)
    c: Block(g2)
    c: Block(g1)
    c: Block(g0)
    c: Block(g6)
    c: Block(g7)
    c: Block(g4)
    c: Block(g5)
FEATURE [Part::Extrusion] Extrude054
  Base = -> Sketch063
  Dir = (0,-1,2e-16)
  DirMode = 2
  FaceMakerClass = Part::FaceMakerBullseye
  LengthFwd = 6
  LengthRev = 0
  Placement = pos=(0,9,0) rot=(0,0,1;0rad)
  Solid = true
  Symmetric = false
FEATURE [Sketcher::SketchObject] Sketch064  label="topSketch017"
  FullyConstrained = true
  sketch-geometry (20):
    g0: LineSegment StartX=5.21097e-06 StartY=3 StartZ=0 EndX=5.21097e-06 EndY=19 EndZ=0
    g1: ArcOfCircle CenterX=19 CenterY=19 CenterZ=0 NormalX=0 NormalY=0 NormalZ=1 AngleXU=0 Radius=19 StartAngle=1.5708 EndAngle=3.14159
    g2: ArcOfCircle CenterX=19 CenterY=19 CenterZ=0 NormalX=0 NormalY=0 NormalZ=1 AngleXU=0 Radius=16 StartAngle=1.5708 EndAngle=3.14159
    g3: LineSegment StartX=114 StartY=35 StartZ=0 EndX=19 EndY=35 EndZ=0
    g4: LineSegment StartX=5.21097e-06 StartY=3 StartZ=0 EndX=5.21097e-06 EndY=0 EndZ=0
    g5: LineSegment StartX=3 StartY=0 StartZ=0 EndX=5.21097e-06 EndY=0 EndZ=0
    g6: LineSegment StartX=3 StartY=19 StartZ=0 EndX=3 EndY=0 EndZ=0
    g7: LineSegment StartX=19 StartY=38 StartZ=0 EndX=124 EndY=38 EndZ=0
    g8: Circle CenterX=119 CenterY=35 CenterZ=0 NormalX=0 NormalY=0 NormalZ=1 AngleXU=0 Radius=1
    g9: Circle CenterX=121 CenterY=35 CenterZ=0 NormalX=0 NormalY=0 NormalZ=1 AngleXU=0 Radius=1
    g10: Circle CenterX=121 CenterY=33 CenterZ=0 NormalX=0 NormalY=0 NormalZ=1 AngleXU=0 Radius=1
    g11: BSplineCurve PolesCount=3 KnotsCount=2 Degree=2 IsPeriodic=0
    g12: GeomPoint X=119 Y=35 Z=0
    g13: GeomPoint X=121 Y=33 Z=0
    g14: LineSegment StartX=119 StartY=35 StartZ=0 EndX=114 EndY=35 EndZ=0
    g15: ArcOfCircle CenterX=105 CenterY=19 CenterZ=0 NormalX=0 NormalY=0 NormalZ=1 AngleXU=0 Radius=19 StartAngle=5.7297 EndAngle=6.28319
    g16: ArcOfCircle CenterX=105 CenterY=19 CenterZ=0 NormalX=0 NormalY=0 NormalZ=1 AngleXU=0 Radius=16 StartAngle=5.60905 EndAngle=6.28319
    g17: LineSegment StartX=121 StartY=33 StartZ=0 EndX=121 EndY=19 EndZ=0
    g18: LineSegment StartX=124 StartY=38 StartZ=0 EndX=124 EndY=19 EndZ=0
    g19: LineSegment StartX=117.5 StartY=9.01251 StartZ=0 EndX=121.163 EndY=9.0125 EndZ=0
  constraints (46):
    c: Vertical(g0)
    c: Block(g0)
    c: Coincident(g1,g0)
    c: Block(g1)
    c: Coincident(g2,g1)
    c: Block(g2)
    c: Coincident(g3,g2)
    c: Horizontal(g3)
    c: Tangent(g3,g2)
    c: Coincident(g4,g0)
    c: Distance(g4) = 3
    c: Vertical(g4)
    c: Coincident(g5,g4)
    c: Horizontal(g5)
    c: Coincident(g6,g2)
    c: Coincident(g6,g5)
    c: Vertical(g6)
    c: Horizontal(g7)
    c: Distance(g7) = 105
    c: Coincident(g7,g1)
    c: Block(g3)
    c: Weight(g8) = 1
    c: Equal(g8,g9)
    c: Equal(g8,g10)
    c: InternalAlignment(g8,g11)
    c: InternalAlignment(g9,g11)
    c: InternalAlignment(g10,g11)
    c: InternalAlignment(g12,g11)
    c: InternalAlignment(g13,g11)
    c: Block(g11)
    c: Coincident(g14,g11)
    c: Coincident(g14,g3)
    c: Horizontal(g14)
    c: Block(g15)
    c: Coincident(g16,g15)
    c: Block(g16)
    c: Coincident(g17,g11)
    c: Coincident(g17,g16)
    c: Vertical(g17)
    c: Distance(g17) = 14
    c: Coincident(g18,g7)
    c: Coincident(g18,g15)
    c: Vertical(g18)
    c: Distance(g18) = 19
    c: Coincident(g19,g16)
    c: Coincident(g19,g15)
FEATURE [Sketcher::SketchObject] Sketch065
  FullyConstrained = true
  MapMode = 3
  Placement = pos=(0,0,0) rot=(1,0,0;1.5708rad)
  sketch-geometry (8):
    g0: Circle CenterX=80.351 CenterY=-67.6202 CenterZ=0 NormalX=0 NormalY=0 NormalZ=1 AngleXU=0 Radius=3
    g1: Circle CenterX=80.351 CenterY=-4.92017 CenterZ=0 NormalX=0 NormalY=0 NormalZ=1 AngleXU=0 Radius=3
    g2: Circle CenterX=23.851 CenterY=-4.92017 CenterZ=0 NormalX=0 NormalY=0 NormalZ=1 AngleXU=0 Radius=3
    g3: Circle CenterX=23.851 CenterY=-67.6202 CenterZ=0 NormalX=0 NormalY=0 NormalZ=1 AngleXU=0 Radius=3
    g4: Circle CenterX=23.851 CenterY=-67.6202 CenterZ=0 NormalX=0 NormalY=0 NormalZ=1 AngleXU=0 Radius=5
    g5: Circle CenterX=80.351 CenterY=-67.6202 CenterZ=0 NormalX=0 NormalY=0 NormalZ=1 AngleXU=0 Radius=5
    g6: Circle CenterX=23.851 CenterY=-4.92017 CenterZ=0 NormalX=0 NormalY=0 NormalZ=1 AngleXU=0 Radius=5
    g7: Circle CenterX=80.351 CenterY=-4.92017 CenterZ=0 NormalX=0 NormalY=0 NormalZ=1 AngleXU=0 Radius=5
  constraints (8):
    c: Block(g1)
    c: Block(g0)
    c: Block(g3)
    c: Block(g2)
    c: Block(g5)
    c: Block(g4)
    c: Block(g6)
    c: Block(g7)
FEATURE [Part::Extrusion] Extrude056
  Base = -> Sketch065
  Dir = (0,-1,2e-16)
  DirMode = 2
  FaceMakerClass = Part::FaceMakerBullseye
  LengthFwd = 2
  LengthRev = 0
  Solid = true
  Symmetric = false
FEATURE [Part::Extrusion] Extrude057  label="top025"
  Base = -> Sketch064
  Dir = (0,0,1)
  DirMode = 2
  FaceMakerClass = Part::FaceMakerBullseye
  LengthFwd = 72
  LengthRev = 0
  Solid = true
  Symmetric = false
FEATURE [Sketcher::SketchObject] Sketch066
  FullyConstrained = true
  MapMode = 3
  Placement = pos=(0,0,0) rot=(1,0,0;1.5708rad)
  Support = -> [Extrude057]
  sketch-geometry (8):
    g0: Circle CenterX=80.351 CenterY=-67.6202 CenterZ=0 NormalX=0 NormalY=0 NormalZ=1 AngleXU=0 Radius=3
    g1: Circle CenterX=80.351 CenterY=-4.92017 CenterZ=0 NormalX=0 NormalY=0 NormalZ=1 AngleXU=0 Radius=3
    g2: Circle CenterX=23.851 CenterY=-4.92017 CenterZ=0 NormalX=0 NormalY=0 NormalZ=1 AngleXU=0 Radius=3
    g3: Circle CenterX=23.851 CenterY=-67.6202 CenterZ=0 NormalX=0 NormalY=0 NormalZ=1 AngleXU=0 Radius=3
    g4: Circle CenterX=23.851 CenterY=-67.6202 CenterZ=0 NormalX=0 NormalY=0 NormalZ=1 AngleXU=0 Radius=5
    g5: Circle CenterX=80.351 CenterY=-67.6202 CenterZ=0 NormalX=0 NormalY=0 NormalZ=1 AngleXU=0 Radius=5
    g6: Circle CenterX=23.851 CenterY=-4.92017 CenterZ=0 NormalX=0 NormalY=0 NormalZ=1 AngleXU=0 Radius=5
    g7: Circle CenterX=80.351 CenterY=-4.92017 CenterZ=0 NormalX=0 NormalY=0 NormalZ=1 AngleXU=0 Radius=5
  constraints (8):
    c: Block(g1)
    c: Block(g0)
    c: Block(g3)
    c: Block(g2)
    c: Block(g5)
    c: Block(g4)
    c: Block(g6)
    c: Block(g7)
FEATURE [Part::Extrusion] Extrude055
  Base = -> Sketch066
  Dir = (0,-1,2e-16)
  DirMode = 2
  FaceMakerClass = Part::FaceMakerBullseye
  LengthFwd = 2
  LengthRev = 0
  Solid = true
  Symmetric = false
FEATURE [Part::Fillet] Fillet041
  Base = -> Extrude056
  Edges = 4 edges r=1.99: [Edge6,Edge12,Edge18,Edge24]
FEATURE [Part::Cut] Cut045
  Base = -> Extrude055
  Placement = pos=(0,6,0) rot=(0,0,1;0rad)
  Tool = -> Fillet041
FEATURE [Part::MultiFuse] Fusion095  label="pcbScrewPillars"
  Placement = pos=(-3.2,-1,72.3) rot=(0,0,1;0rad)
  Shapes = -> [Cut045,Extrude054]
FEATURE [Part::Feature] Face113
  shape: bbox 3.2 x 1.5 x 2e-07 mm, 1 faces, 0 solids (baked)
FEATURE [Part::Revolution] Revolve121  label="backCaseScrewRetainer002"
  Angle = 360
  Axis = (0,1,0)
  Base = (0,0,0)
  FaceMakerClass = Part::FaceMakerBullseye
  Placement = pos=(12.5,3,62) rot=(0,0,1;0rad)
  Solid = false
  Source = -> Face113
  Symmetric = false
FEATURE [Part::Feature] Face114
  shape: bbox 3.2 x 1.5 x 2e-07 mm, 1 faces, 0 solids (baked)
FEATURE [Part::Feature] Face115
  shape: bbox 3.2 x 1.5 x 2e-07 mm, 1 faces, 0 solids (baked)
FEATURE [Part::Feature] Face116
  shape: bbox 3.2 x 1.5 x 2e-07 mm, 1 faces, 0 solids (baked)
FEATURE [Part::Revolution] Revolve122  label="frontCaseScrewRetainer004"
  Angle = 360
  Axis = (0,1,0)
  Base = (0,0,0)
  FaceMakerClass = Part::FaceMakerBullseye
  Placement = pos=(89.5,3,68.5) rot=(0,0,1;0rad)
  Solid = false
  Source = -> Face115
  Symmetric = false
FEATURE [Part::Revolution] Revolve123  label="frontCaseScrewRetainer005"
  Angle = 360
  Axis = (0,1,0)
  Base = (0,0,0)
  FaceMakerClass = Part::FaceMakerBullseye
  Placement = pos=(89.5,3,3.5) rot=(0,0,1;0rad)
  Solid = false
  Source = -> Face116
  Symmetric = false
FEATURE [Part::Revolution] Revolve124  label="backCaseScrewRetainer003"
  Angle = 360
  Axis = (0,1,0)
  Base = (0,0,0)
  FaceMakerClass = Part::FaceMakerBullseye
  Placement = pos=(12.5,3,10) rot=(0,0,1;0rad)
  Solid = false
  Source = -> Face114
  Symmetric = false
FEATURE [Part::Feature] Face117
  shape: bbox 3.6 x 3.2 x 2e-07 mm, 1 faces, 0 solids (baked)
FEATURE [Part::Revolution] Revolve125  label="moreFrontCaseScrewRetainer004"
  Angle = 360
  Axis = (0,1,0)
  Base = (0,0,0)
  FaceMakerClass = Part::FaceMakerBullseye
  Placement = pos=(109.5,4.5,68.5) rot=(0,0,1;0rad)
  Solid = false
  Source = -> Face117
  Symmetric = false
FEATURE [Part::Feature] Face118
  shape: bbox 3.6 x 3.2 x 2e-07 mm, 1 faces, 0 solids (baked)
FEATURE [Part::Revolution] Revolve126  label="moreFrontCaseScrewRetainer005"
  Angle = 360
  Axis = (0,1,0)
  Base = (0,0,0)
  FaceMakerClass = Part::FaceMakerBullseye
  Placement = pos=(109.5,4.5,3.5) rot=(0,0,1;0rad)
  Solid = false
  Source = -> Face118
  Symmetric = false
FEATURE [Part::MultiFuse] Fusion096  label="screwRetainers001"
  Shapes = -> [Revolve126,Revolve125,Revolve124,Revolve123,Revolve122,Revolve121]
FEATURE [Part::Feature] Face119
  shape: bbox 10 x 16.5 x 2e-07 mm, 1 faces, 0 solids (baked)
FEATURE [Part::Revolution] Revolve130  label="plugHousing050"
  Angle = 360
  Axis = (0,1,0)
  Base = (0,0,0)
  FaceMakerClass = Part::FaceMakerBullseye
  Placement = pos=(0,0,36.15) rot=(0,0,1;0rad)
  Solid = false
  Source = -> Face119
  Symmetric = false
FEATURE [Part::Feature] Face120
  shape: bbox 10 x 16.5 x 2e-07 mm, 1 faces, 0 solids (baked)
FEATURE [Part::Feature] Face121
  shape: bbox 10 x 16.5 x 2e-07 mm, 1 faces, 0 solids (baked)
FEATURE [Part::Revolution] Revolve127  label="plugHousing047"
  Angle = 360
  Axis = (0,1,0)
  Base = (0,0,0)
  FaceMakerClass = Part::FaceMakerBullseye
  Placement = pos=(0,0,36.15) rot=(0,0,1;0rad)
  Solid = false
  Source = -> Face121
  Symmetric = false
FEATURE [Part::Feature] Face122
  shape: bbox 10 x 16.5 x 2e-07 mm, 1 faces, 0 solids (baked)
FEATURE [Part::Feature] Face123
  shape: bbox 10 x 16.5 x 2e-07 mm, 1 faces, 0 solids (baked)
FEATURE [Part::Revolution] Revolve128  label="plugHousing048"
  Angle = 360
  Axis = (0,1,0)
  Base = (0,0,0)
  FaceMakerClass = Part::FaceMakerBullseye
  Placement = pos=(0,0,36.15) rot=(0,0,1;0rad)
  Solid = false
  Source = -> Face123
  Symmetric = false
FEATURE [Part::MultiFuse] Fusion100  label="plugHousing054"
  Placement = pos=(0,0,0) rot=(0,0,1;1.5708rad)
  Shapes = -> [Revolve130,Revolve128]
FEATURE [Part::Feature] Face124
  shape: bbox 10 x 16.5 x 2e-07 mm, 1 faces, 0 solids (baked)
FEATURE [Part::Feature] Face125
  shape: bbox 10 x 16.5 x 2e-07 mm, 1 faces, 0 solids (baked)
FEATURE [Part::Revolution] Revolve129  label="plugHousing049"
  Angle = 360
  Axis = (0,1,0)
  Base = (0,0,0)
  FaceMakerClass = Part::FaceMakerBullseye
  Placement = pos=(0,0,36.15) rot=(0,0,1;0rad)
  Solid = false
  Source = -> Face125
  Symmetric = false
FEATURE [Part::Feature] Face126
  shape: bbox 10 x 16.5 x 2e-07 mm, 1 faces, 0 solids (baked)
FEATURE [Part::Revolution] Revolve131  label="plugHousing058"
  Angle = 360
  Axis = (0,1,0)
  Base = (0,0,0)
  FaceMakerClass = Part::FaceMakerBullseye
  Placement = pos=(0,0,36.15) rot=(0,0,1;0rad)
  Solid = false
  Source = -> Face120
  Symmetric = false
FEATURE [Part::MultiFuse] Fusion099  label="plugHousing053"
  Placement = pos=(0,0,0) rot=(0,0,1;1.5708rad)
  Shapes = -> [Revolve127,Revolve131]
FEATURE [Part::MultiFuse] Fusion102  label="plugHousing056"
  Placement = pos=(0,19,0) rot=(0,0,1;3.14159rad)
  Shapes = -> [Fusion100,Fusion099]
FEATURE [Part::Revolution] Revolve132  label="plugHousing059"
  Angle = 360
  Axis = (0,1,0)
  Base = (0,0,0)
  FaceMakerClass = Part::FaceMakerBullseye
  Placement = pos=(0,0,36.15) rot=(0,0,1;0rad)
  Solid = false
  Source = -> Face126
  Symmetric = false
FEATURE [Part::Revolution] Revolve133  label="plugHousing060"
  Angle = 360
  Axis = (0,1,0)
  Base = (0,0,0)
  FaceMakerClass = Part::FaceMakerBullseye
  Placement = pos=(0,0,36.15) rot=(0,0,1;0rad)
  Solid = false
  Source = -> Face122
  Symmetric = false
FEATURE [Part::MultiFuse] Fusion097  label="plugHousing051"
  Placement = pos=(0,0,0) rot=(0,0,1;1.5708rad)
  Shapes = -> [Revolve133,Revolve132]
FEATURE [Part::Revolution] Revolve134  label="plugHousing061"
  Angle = 360
  Axis = (0,1,0)
  Base = (0,0,0)
  FaceMakerClass = Part::FaceMakerBullseye
  Placement = pos=(0,0,36.15) rot=(0,0,1;0rad)
  Solid = false
  Source = -> Face124
  Symmetric = false
FEATURE [Part::MultiFuse] Fusion101  label="plugHousing055"
  Placement = pos=(0,0,0) rot=(0,0,1;1.5708rad)
  Shapes = -> [Revolve129,Revolve134]
FEATURE [Part::MultiFuse] Fusion098  label="plugHousing052"
  Placement = pos=(0,19,0) rot=(0,0,1;3.14159rad)
  Shapes = -> [Fusion097,Fusion101]
FEATURE [Part::MultiFuse] Fusion103  label="plugHousing057"
  Placement = pos=(122.621,0,-0.15) rot=(0,0,1;0rad)
  Shapes = -> [Fusion102,Fusion098]
FEATURE [Part::Box] Box028  label="Cube015"
  AttacherType = Attacher::AttachEngine3D
  Height = 28
  Length = 3
  Placement = pos=(110.7,19,22) rot=(0,0,1;0rad)
  Width = 15.7
FEATURE [Part::Cylinder] Cylinder044
  Angle = 360
  AttacherType = Attacher::AttachEngine3D
  Height = 20
  Placement = pos=(0,0,36.15) rot=(0,0,1;0rad)
  Radius = 10.3
FEATURE [Part::Cylinder] Cylinder045
  Angle = 360
  AttacherType = Attacher::AttachEngine3D
  Height = 10
  Placement = pos=(0,0,36.15) rot=(0,0,1;0rad)
  Radius = 4
FEATURE [Part::MultiFuse] Fusion104  label="removeToCreteHoleForPlugHousing040"
  Placement = pos=(70,19,36) rot=(0,1,0;1.5708rad)
  Shapes = -> [Cylinder044,Cylinder045]
FEATURE [Part::Cut] Cut046  label="plugHousingTab003"
  Base = -> Box028
  Tool = -> Fusion104
FEATURE [Part::MultiFuse] Fusion105  label="plugHousing062"
  Shapes = -> [Fusion103,Cut046]
FEATURE [Part::Fillet] Fillet042
  Base = -> Fusion105
  Edges = 1 edges r=2: [Edge25]
FEATURE [Part::Fillet] Fillet043  label="plugHousing063"
  Base = -> Fillet042
  Edges = 1 edges r=2: [Edge8]
  Placement = pos=(7,0,0) rot=(0,0,1;0rad)
FEATURE [Part::Feature] Face127
  shape: bbox 10 x 16.5 x 2e-07 mm, 1 faces, 0 solids (baked)
FEATURE [Part::Feature] Face128
  shape: bbox 10 x 16.5 x 2e-07 mm, 1 faces, 0 solids (baked)
FEATURE [Part::Revolution] Revolve137  label="plugHousing070"
  Angle = 360
  Axis = (0,1,0)
  Base = (0,0,0)
  FaceMakerClass = Part::FaceMakerBullseye
  Placement = pos=(0,0,36.15) rot=(0,0,1;0rad)
  Solid = false
  Source = -> Face127
  Symmetric = false
FEATURE [Part::Revolution] Revolve140  label="plugHousing073"
  Angle = 360
  Axis = (0,1,0)
  Base = (0,0,0)
  FaceMakerClass = Part::FaceMakerBullseye
  Placement = pos=(0,0,36.15) rot=(0,0,1;0rad)
  Solid = false
  Source = -> Face128
  Symmetric = false
FEATURE [Part::Feature] Face129
  shape: bbox 10 x 16.5 x 2e-07 mm, 1 faces, 0 solids (baked)
FEATURE [Part::Revolution] Revolve138  label="plugHousing071"
  Angle = 360
  Axis = (0,1,0)
  Base = (0,0,0)
  FaceMakerClass = Part::FaceMakerBullseye
  Placement = pos=(0,0,36.15) rot=(0,0,1;0rad)
  Solid = false
  Source = -> Face129
  Symmetric = false
FEATURE [Part::Feature] Face130
  shape: bbox 10 x 16.5 x 2e-07 mm, 1 faces, 0 solids (baked)
FEATURE [Part::Revolution] Revolve139  label="plugHousing072"
  Angle = 360
  Axis = (0,1,0)
  Base = (0,0,0)
  FaceMakerClass = Part::FaceMakerBullseye
  Placement = pos=(0,0,36.15) rot=(0,0,1;0rad)
  Solid = false
  Source = -> Face130
  Symmetric = false
FEATURE [Part::Feature] Face131
  shape: bbox 10 x 16.5 x 2e-07 mm, 1 faces, 0 solids (baked)
FEATURE [Part::Revolution] Revolve135  label="plugHousing068"
  Angle = 360
  Axis = (0,1,0)
  Base = (0,0,0)
  FaceMakerClass = Part::FaceMakerBullseye
  Placement = pos=(0,0,36.15) rot=(0,0,1;0rad)
  Solid = false
  Source = -> Face131
  Symmetric = false
FEATURE [Part::MultiFuse] Fusion112  label="plugHousing078"
  Placement = pos=(0,0,0) rot=(0,0,1;1.5708rad)
  Shapes = -> [Revolve135,Revolve139]
FEATURE [Part::Feature] Face132
  shape: bbox 10 x 16.5 x 2e-07 mm, 1 faces, 0 solids (baked)
FEATURE [Part::Revolution] Revolve141  label="plugHousing074"
  Angle = 360
  Axis = (0,1,0)
  Base = (0,0,0)
  FaceMakerClass = Part::FaceMakerBullseye
  Placement = pos=(0,0,36.15) rot=(0,0,1;0rad)
  Solid = false
  Source = -> Face132
  Symmetric = false
FEATURE [Part::MultiFuse] Fusion110  label="plugHousing076"
  Placement = pos=(0,0,0) rot=(0,0,1;1.5708rad)
  Shapes = -> [Revolve141,Revolve140]
FEATURE [Part::Feature] Face133
  shape: bbox 10 x 16.5 x 2e-07 mm, 1 faces, 0 solids (baked)
FEATURE [Part::Revolution] Revolve136  label="plugHousing069"
  Angle = 360
  Axis = (0,1,0)
  Base = (0,0,0)
  FaceMakerClass = Part::FaceMakerBullseye
  Placement = pos=(0,0,36.15) rot=(0,0,1;0rad)
  Solid = false
  Source = -> Face133
  Symmetric = false
FEATURE [Part::MultiFuse] Fusion106  label="plugHousing064"
  Placement = pos=(0,0,0) rot=(0,0,1;1.5708rad)
  Shapes = -> [Revolve138,Revolve136]
FEATURE [Part::MultiFuse] Fusion108  label="plugHousing066"
  Placement = pos=(0,19,0) rot=(0,0,1;3.14159rad)
  Shapes = -> [Fusion106,Fusion112]
FEATURE [Part::Feature] Face134
  shape: bbox 10 x 16.5 x 2e-07 mm, 1 faces, 0 solids (baked)
FEATURE [Part::Revolution] Revolve142  label="plugHousing075"
  Angle = 360
  Axis = (0,1,0)
  Base = (0,0,0)
  FaceMakerClass = Part::FaceMakerBullseye
  Placement = pos=(0,0,36.15) rot=(0,0,1;0rad)
  Solid = false
  Source = -> Face134
  Symmetric = false
FEATURE [Part::MultiFuse] Fusion107  label="plugHousing065"
  Placement = pos=(0,0,0) rot=(0,0,1;1.5708rad)
  Shapes = -> [Revolve137,Revolve142]
FEATURE [Part::MultiFuse] Fusion111  label="plugHousing077"
  Placement = pos=(0,19,0) rot=(0,0,1;3.14159rad)
  Shapes = -> [Fusion110,Fusion107]
FEATURE [Part::MultiFuse] Fusion109  label="plugHousing067"
  Placement = pos=(131.236,0,-0.15) rot=(0,0,1;0rad)
  Shapes = -> [Fusion108,Fusion111]
FEATURE [Part::MultiFuse] Fusion113  label="plugHousing079"
  Shapes = -> [Fillet043,Fusion109]
FEATURE [Part::Feature] Face135
  shape: bbox 3.5 x 17.8 x 2e-07 mm, 1 faces, 0 solids (baked)
FEATURE [Part::Revolution] Revolve143  label="removeToCreateScrewAndThreadedInsertHole049"
  Angle = 360
  Axis = (0,1,0)
  Base = (0,0,0)
  FaceMakerClass = Part::FaceMakerBullseye
  Placement = pos=(12.5,0,10) rot=(0,0,1;0rad)
  Solid = false
  Source = -> Face135
  Symmetric = false
FEATURE [Part::Feature] Face136
  shape: bbox 3.5 x 17.8 x 2e-07 mm, 1 faces, 0 solids (baked)
FEATURE [Part::Revolution] Revolve144  label="removeToCreateScrewAndThreadedInsertHole050"
  Angle = 360
  Axis = (0,1,0)
  Base = (0,0,0)
  FaceMakerClass = Part::FaceMakerBullseye
  Placement = pos=(12.5,0,62) rot=(0,0,1;0rad)
  Solid = false
  Source = -> Face136
  Symmetric = false
FEATURE [Part::Feature] Face137
  shape: bbox 3.5 x 17.8 x 2e-07 mm, 1 faces, 0 solids (baked)
FEATURE [Part::Revolution] Revolve145  label="removeToCreateScrewAndThreadedInsertHole051"
  Angle = 360
  Axis = (0,1,0)
  Base = (0,0,0)
  FaceMakerClass = Part::FaceMakerBullseye
  Placement = pos=(89.5,0,68.5) rot=(0,0,1;0rad)
  Solid = false
  Source = -> Face137
  Symmetric = false
FEATURE [Part::Feature] Face138
  shape: bbox 3.5 x 17.8 x 2e-07 mm, 1 faces, 0 solids (baked)
FEATURE [Part::Revolution] Revolve146  label="removeToCreateScrewAndThreadedInsertHole052"
  Angle = 360
  Axis = (0,1,0)
  Base = (0,0,0)
  FaceMakerClass = Part::FaceMakerBullseye
  Placement = pos=(89.5,0,3.5) rot=(0,0,1;0rad)
  Solid = false
  Source = -> Face138
  Symmetric = false
FEATURE [Part::Feature] Face139
  shape: bbox 3.5 x 17.8 x 2e-07 mm, 1 faces, 0 solids (baked)
FEATURE [Part::Revolution] Revolve147  label="removeToCreateScrewAndThreadedInsertHole053"
  Angle = 360
  Axis = (0,1,0)
  Base = (0,0,0)
  FaceMakerClass = Part::FaceMakerBullseye
  Placement = pos=(109.5,4.7,3.5) rot=(0,0,1;0rad)
  Solid = false
  Source = -> Face139
  Symmetric = false
FEATURE [Part::Feature] Face140
  shape: bbox 3.5 x 17.8 x 2e-07 mm, 1 faces, 0 solids (baked)
FEATURE [Part::Revolution] Revolve148  label="removeToCreateScrewAndThreadedInsertHole054"
  Angle = 360
  Axis = (0,1,0)
  Base = (0,0,0)
  FaceMakerClass = Part::FaceMakerBullseye
  Placement = pos=(109.5,4.7,68.5) rot=(0,0,1;0rad)
  Solid = false
  Source = -> Face140
  Symmetric = false
FEATURE [Part::MultiFuse] Fusion114  label="removeToCreateScrewAndThreadedInsertHole055"
  Shapes = -> [Revolve148,Revolve147,Revolve146,Revolve145,Revolve144,Revolve143]
FEATURE [Part::Cut] Cut047  label="casePillars004"
  Base = -> Cut037
  Tool = -> Fusion114
FEATURE [Part::Feature] Face141
  shape: bbox 3.5 x 17.8 x 2e-07 mm, 1 faces, 0 solids (baked)
FEATURE [Part::Feature] Face142
  shape: bbox 3.5 x 17.8 x 2e-07 mm, 1 faces, 0 solids (baked)
FEATURE [Part::Feature] Face143
  shape: bbox 3.5 x 17.8 x 2e-07 mm, 1 faces, 0 solids (baked)
FEATURE [Part::Revolution] Revolve149  label="removeToCreateScrewAndThreadedInsertHole057"
  Angle = 360
  Axis = (0,1,0)
  Base = (0,0,0)
  FaceMakerClass = Part::FaceMakerBullseye
  Placement = pos=(12.5,0,10) rot=(0,0,1;0rad)
  Solid = false
  Source = -> Face141
  Symmetric = false
FEATURE [Part::Feature] Face144
  shape: bbox 3.5 x 17.8 x 2e-07 mm, 1 faces, 0 solids (baked)
FEATURE [Part::Feature] Face145
  shape: bbox 3.5 x 17.8 x 2e-07 mm, 1 faces, 0 solids (baked)
FEATURE [Part::Feature] Face146
  shape: bbox 3.5 x 17.8 x 2e-07 mm, 1 faces, 0 solids (baked)
FEATURE [Part::Revolution] Revolve150  label="removeToCreateScrewAndThreadedInsertHole058"
  Angle = 360
  Axis = (0,1,0)
  Base = (0,0,0)
  FaceMakerClass = Part::FaceMakerBullseye
  Placement = pos=(12.5,0,62) rot=(0,0,1;0rad)
  Solid = false
  Source = -> Face146
  Symmetric = false
FEATURE [Part::Revolution] Revolve151  label="removeToCreateScrewAndThreadedInsertHole059"
  Angle = 360
  Axis = (0,1,0)
  Base = (0,0,0)
  FaceMakerClass = Part::FaceMakerBullseye
  Placement = pos=(89.5,0,68.5) rot=(0,0,1;0rad)
  Solid = false
  Source = -> Face143
  Symmetric = false
FEATURE [Part::Revolution] Revolve152  label="removeToCreateScrewAndThreadedInsertHole060"
  Angle = 360
  Axis = (0,1,0)
  Base = (0,0,0)
  FaceMakerClass = Part::FaceMakerBullseye
  Placement = pos=(89.5,0,3.5) rot=(0,0,1;0rad)
  Solid = false
  Source = -> Face142
  Symmetric = false
FEATURE [Part::Revolution] Revolve153  label="removeToCreateScrewAndThreadedInsertHole061"
  Angle = 360
  Axis = (0,1,0)
  Base = (0,0,0)
  FaceMakerClass = Part::FaceMakerBullseye
  Placement = pos=(109.5,4.7,3.5) rot=(0,0,1;0rad)
  Solid = false
  Source = -> Face145
  Symmetric = false
FEATURE [Part::Revolution] Revolve154  label="removeToCreateScrewAndThreadedInsertHole062"
  Angle = 360
  Axis = (0,1,0)
  Base = (0,0,0)
  FaceMakerClass = Part::FaceMakerBullseye
  Placement = pos=(109.5,4.7,68.5) rot=(0,0,1;0rad)
  Solid = false
  Source = -> Face144
  Symmetric = false
FEATURE [Part::MultiFuse] Fusion115  label="removeToCreateScrewAndThreadedInsertHole056"
  Shapes = -> [Revolve154,Revolve153,Revolve152,Revolve151,Revolve150,Revolve149]
FEATURE [Part::Feature] Face147
  shape: bbox 9.8 x 26.5 x 2e-07 mm, 1 faces, 0 solids (baked)
FEATURE [Part::Revolution] Revolve155
  Angle = 360
  Axis = (0,1,0)
  Base = (0,0,0)
  FaceMakerClass = Part::FaceMakerBullseye
  Placement = pos=(0,0,0) rot=(0,0,1;1.5708rad)
  Solid = false
  Source = -> Face147
  Symmetric = false
FEATURE [Part::Feature] Face148
  shape: bbox 9.8 x 26.5 x 2e-07 mm, 1 faces, 0 solids (baked)
FEATURE [Part::Revolution] Revolve156
  Angle = 360
  Axis = (0,1,0)
  Base = (0,0,0)
  FaceMakerClass = Part::FaceMakerBullseye
  Placement = pos=(0,0,0) rot=(0,0,1;1.5708rad)
  Solid = false
  Source = -> Face148
  Symmetric = false
FEATURE [Part::MultiFuse] Fusion116
  Placement = pos=(-18,19,36) rot=(0,0,1;0rad)
  Shapes = -> [Revolve156,Revolve155]
FEATURE [Part::Box] Box029  label="Cube016"
  AttacherType = Attacher::AttachEngine3D
  Height = 28
  Length = 3
  Placement = pos=(110.7,19,22) rot=(0,0,1;0rad)
  Width = 15.7
FEATURE [Part::Cylinder] Cylinder046
  Angle = 360
  AttacherType = Attacher::AttachEngine3D
  Height = 10
  Placement = pos=(0,0,36.15) rot=(0,0,1;0rad)
  Radius = 4
FEATURE [Part::Cylinder] Cylinder047
  Angle = 360
  AttacherType = Attacher::AttachEngine3D
  Height = 20
  Placement = pos=(0,0,36.15) rot=(0,0,1;0rad)
  Radius = 10.3
FEATURE [Part::MultiFuse] Fusion117  label="removeToCreteHoleForPlugHousing041"
  Placement = pos=(70,19,36) rot=(0,1,0;1.5708rad)
  Shapes = -> [Cylinder047,Cylinder046]
FEATURE [Part::Cut] Cut049  label="plugHousingTab004"
  Base = -> Box029
  Placement = pos=(-107.4,-14,0) rot=(0,0,1;0rad)
  Tool = -> Fusion117
FEATURE [Part::Box] Box030  label="Cube017"
  AttacherType = Attacher::AttachEngine3D
  Height = 28
  Length = 3
  Placement = pos=(110.7,19,22) rot=(0,0,1;0rad)
  Width = 15.7
FEATURE [Part::Cylinder] Cylinder048
  Angle = 360
  AttacherType = Attacher::AttachEngine3D
  Height = 10
  Placement = pos=(0,0,36.15) rot=(0,0,1;0rad)
  Radius = 4
FEATURE [Part::Cylinder] Cylinder049
  Angle = 360
  AttacherType = Attacher::AttachEngine3D
  Height = 20
  Placement = pos=(0,0,36.15) rot=(0,0,1;0rad)
  Radius = 10.3
FEATURE [Part::MultiFuse] Fusion118  label="removeToCreteHoleForPlugHousing042"
  Placement = pos=(70,19,36) rot=(0,1,0;1.5708rad)
  Shapes = -> [Cylinder049,Cylinder048]
FEATURE [Part::Cut] Cut050  label="plugHousingTab005"
  Base = -> Box030
  Placement = pos=(-107.4,-14,0) rot=(0,0,1;0rad)
  Tool = -> Fusion118
FEATURE [Part::MultiFuse] Fusion119
  Placement = pos=(9.6,23,0) rot=(0,0,1;3.14159rad)
  Shapes = -> [Cut049,Cut050]
FEATURE [Part::Box] Box031  label="Cube018"
  AttacherType = Attacher::AttachEngine3D
  Height = 10
  Length = 3
  Placement = pos=(3.3,4,12) rot=(0,0,1;0rad)
  Width = 10
FEATURE [Part::Fillet] Fillet044
  Base = -> Box031
  Edges = 1 edges r=2: [Edge11]
FEATURE [Part::Box] Box032  label="Cube019"
  AttacherType = Attacher::AttachEngine3D
  Height = 10
  Length = 3
  Placement = pos=(3.3,4,50) rot=(0,0,1;0rad)
  Width = 10
FEATURE [Part::Fillet] Fillet045
  Base = -> Box032
  Edges = 1 edges r=2: [Edge12]
FEATURE [Part::Box] Box033  label="Cube020"
  AttacherType = Attacher::AttachEngine3D
  Height = 28
  Length = 4
  Placement = pos=(5,0,22) rot=(0,0,1;0rad)
  Width = 10
FEATURE [Part::Fillet] Fillet046
  Base = -> Box033
  Edges = 1 edges r=1: [Edge7]
FEATURE [Part::Fillet] Fillet047
  Base = -> Fillet046
  Edges = 1 edges r=2: [Edge5]
FEATURE [Part::Fillet] Fillet048
  Base = -> Fillet047
  Edges = 1 edges r=2: [Edge2]
FEATURE [Part::Cylinder] Cylinder050
  Angle = 360
  AttacherType = Attacher::AttachEngine3D
  Height = 20
  Placement = pos=(0,0,36.15) rot=(0,0,1;0rad)
  Radius = 8.2
FEATURE [Part::Cylinder] Cylinder051
  Angle = 360
  AttacherType = Attacher::AttachEngine3D
  Height = 10
  Placement = pos=(0,0,36.15) rot=(0,0,1;0rad)
  Radius = 4
FEATURE [Part::MultiFuse] Fusion120  label="removeToCreteHoleForPlugHousing043"
  Placement = pos=(-42,19,36) rot=(0,1,0;1.5708rad)
  Shapes = -> [Cylinder050,Cylinder051]
FEATURE [Sketcher::SketchObject] Sketch067  label="topSketch018"
  FullyConstrained = true
  sketch-geometry (4):
    g0: LineSegment StartX=16.8446 StartY=31.512 StartZ=0 EndX=16.3251 EndY=34.4666 EndZ=0
    g1: ArcOfCircle CenterX=19 CenterY=19.2524 CenterZ=0 NormalX=0 NormalY=0 NormalZ=1 AngleXU=0 Radius=15.4476 StartAngle=1.74483 EndAngle=2.72717
    g2: ArcOfCircle CenterX=19 CenterY=19.2524 CenterZ=0 NormalX=0 NormalY=0 NormalZ=1 AngleXU=0 Radius=12.4476 StartAngle=1.74483 EndAngle=2.73189
    g3: LineSegment StartX=4.86004 StartY=25.4725 StartZ=0 EndX=7.58253 EndY=24.2107 EndZ=0
  constraints (7):
    c: Block(g0)
    c: Coincident(g1,g0)
    c: Coincident(g2,g0)
    c: Coincident(g3,g1)
    c: Coincident(g3,g2)
    c: Block(g1)
    c: Block(g2)
FEATURE [Part::Extrusion] Extrude058
  Base = -> Sketch067
  Dir = (0,0,1)
  DirMode = 2
  FaceMakerClass = Part::FaceMakerBullseye
  LengthFwd = 10
  LengthRev = 0
  Placement = pos=(0,0,31) rot=(0,0,1;0rad)
  Solid = true
  Symmetric = false
FEATURE [Part::Cut] Cut051
  Base = -> Extrude058
  Tool = -> Fusion120
FEATURE [Part::Fillet] Fillet049
  Base = -> Cut051
  Edges = 1 edges r=2: [Edge1]
FEATURE [Part::Fillet] Fillet050
  Base = -> Fillet049
  Edges = 1 edges r=2.5: [Edge1]
FEATURE [Part::Fillet] Fillet051
  Base = -> Fillet050
  Edges = 1 edges r=2.5: [Edge2]
FEATURE [Part::MultiFuse] Fusion121  label="wireHolder003"
  Shapes = -> [Fusion116,Fillet051]
FEATURE [Part::MultiFuse] Fusion122
  Shapes = -> [Fillet045,Fusion121]
FEATURE [Part::MultiFuse] Fusion123  label="wireHolder004"
  Shapes = -> [Fusion122,Fillet048]
FEATURE [Part::MultiFuse] Fusion124  label="wireHolder005"
  Shapes = -> [Fillet044,Fusion119,Fusion123]
FEATURE [Part::MultiFuse] Fusion126  label="casePillars005"
  Shapes = -> [Fusion092,Cut047]
FEATURE [Sketcher::SketchObject] Sketch068  label="topSketch019"
  FullyConstrained = true
  sketch-geometry (6):
    g0: LineSegment StartX=19 StartY=38 StartZ=0 EndX=117 EndY=38 EndZ=0
    g1: ArcOfCircle CenterX=19 CenterY=19 CenterZ=0 NormalX=0 NormalY=0 NormalZ=1 AngleXU=0 Radius=19 StartAngle=1.5708 EndAngle=3.14159
    g2: LineSegment StartX=117 StartY=38 StartZ=0 EndX=117 EndY=19 EndZ=0
    g3: LineSegment StartX=98 StartY=1.0161e-12 StartZ=0 EndX=5.22862e-06 EndY=1.0161e-12 EndZ=0
    g4: LineSegment StartX=5.22862e-06 StartY=19 StartZ=0 EndX=5.22862e-06 EndY=1.0161e-12 EndZ=0
    g5: ArcOfCircle CenterX=98 CenterY=19 CenterZ=0 NormalX=0 NormalY=0 NormalZ=1 AngleXU=0 Radius=19 StartAngle=4.71239 EndAngle=6.28319
  constraints (16):
    c: Horizontal(g0)
    c: Distance(g0) = 98
    c: Coincident(g1,g0)
    c: Block(g1)
    c: Coincident(g2,g0)
    c: Vertical(g2)
    c: Distance(g2) = 19
    c: Horizontal(g3)
    c: Coincident(g4,g1)
    c: Vertical(g4)
    c: Coincident(g3,g4)
    c: Block(g3)
    c: Coincident(g5,g2)
    c: Coincident(g5,g3)
    c: Block(g0)
    c: Block(g5)
FEATURE [Part::Extrusion] Extrude059  label="sideA002"
  Base = -> Sketch068
  Dir = (0,0,1)
  DirMode = 2
  FaceMakerClass = Part::FaceMakerBullseye
  LengthFwd = 3
  LengthRev = 0
  Placement = pos=(0,0,-2.7) rot=(0,0,1;0rad)
  Solid = true
  Symmetric = false
FEATURE [Sketcher::SketchObject] Sketch069  label="topSketch020"
  FullyConstrained = true
  sketch-geometry (6):
    g0: LineSegment StartX=19 StartY=38 StartZ=0 EndX=117 EndY=38 EndZ=0
    g1: ArcOfCircle CenterX=19 CenterY=19 CenterZ=0 NormalX=0 NormalY=0 NormalZ=1 AngleXU=0 Radius=19 StartAngle=1.5708 EndAngle=3.14159
    g2: LineSegment StartX=117 StartY=38 StartZ=0 EndX=117 EndY=19 EndZ=0
    g3: LineSegment StartX=98 StartY=1.0161e-12 StartZ=0 EndX=5.22862e-06 EndY=1.0161e-12 EndZ=0
    g4: LineSegment StartX=5.22862e-06 StartY=19 StartZ=0 EndX=5.22862e-06 EndY=1.0161e-12 EndZ=0
    g5: ArcOfCircle CenterX=98 CenterY=19 CenterZ=0 NormalX=0 NormalY=0 NormalZ=1 AngleXU=0 Radius=19 StartAngle=4.71239 EndAngle=6.28319
  constraints (16):
    c: Horizontal(g0)
    c: Distance(g0) = 98
    c: Coincident(g1,g0)
    c: Block(g1)
    c: Coincident(g2,g0)
    c: Vertical(g2)
    c: Distance(g2) = 19
    c: Horizontal(g3)
    c: Coincident(g4,g1)
    c: Vertical(g4)
    c: Coincident(g3,g4)
    c: Block(g3)
    c: Coincident(g5,g2)
    c: Coincident(g5,g3)
    c: Block(g0)
    c: Block(g5)
FEATURE [Part::Extrusion] Extrude060  label="sideB002"
  Base = -> Sketch069
  Dir = (0,0,1)
  DirMode = 2
  FaceMakerClass = Part::FaceMakerBullseye
  LengthFwd = 3
  LengthRev = 0
  Placement = pos=(0,0,71.7) rot=(0,0,1;0rad)
  Solid = true
  Symmetric = false
FEATURE [Part::MultiFuse] Fusion127  label="removeFromBottom001"
  Placement = pos=(2,0,0) rot=(0,0,1;0rad)
  Shapes = -> [Extrude059,Extrude060]
FEATURE [Part::Cylinder] Cylinder052
  Angle = 360
  AttacherType = Attacher::AttachEngine3D
  Height = 20
  Placement = pos=(0,0,36.15) rot=(0,0,1;0rad)
  Radius = 14
FEATURE [Part::Cylinder] Cylinder053
  Angle = 360
  AttacherType = Attacher::AttachEngine3D
  Height = 10
  Placement = pos=(0,0,36.15) rot=(0,0,1;0rad)
  Radius = 4
FEATURE [Part::MultiFuse] Fusion128  label="removeToCreteHoleForPlugHousing044"
  Placement = pos=(70,19,36) rot=(0,1,0;1.5708rad)
  Shapes = -> [Cylinder052,Cylinder053]
FEATURE [Part::Cut] Cut052  label="bottom011"
  Base = -> Extrude043
  Tool = -> Fusion128
FEATURE [Part::MultiFuse] Fusion129  label="screwRetainersAndInsertHolders"
  Shapes = -> [Fusion095,Fusion096]
FEATURE [Part::Cut] Cut053  label="screwRetainersAndInsertHolders001"
  Base = -> Fusion129
  Tool = -> Fusion127
FEATURE [Part::Cut] Cut054
  Base = -> Cut052
  Tool = -> Fusion115
